FCSTD DOCUMENT  (FreeCAD 0.21R33771 (Git))
Label: pillarAssy3
License: All rights reserved
objects: Sketcher::SketchObject×109, Part::FeaturePython×100, Part::Extrusion×84, App::Part×44, Part::Cut×39, Part::Compound×35, Part::Mirroring×34, App::FeaturePython×19, Part::Revolution×18, Part::Feature×15, Spreadsheet::Sheet×13, Part::MultiFuse×12, Part::Cylinder×9, Part::Sweep×8, PartDesign::Pad×2, PartDesign::Body×1, Part::Chamfer×1, Part::Loft×1, Part::Thickness×1
note: 442 computed .brp shape members not serialized (recipe doc carries the construction recipe); baked Part::Feature solids carry a one-line shape summary decoded from their .brp

FEATURE [Sketcher::SketchObject] Sketch
  FullyConstrained = false
  Placement = pos=(0,0,0) rot=(1,0,0;1.5708rad)
  sketch-geometry (12):
    g0: LineSegment StartX=0 StartY=4910 StartZ=0 EndX=0 EndY=850 EndZ=0
    g1: LineSegment StartX=0 StartY=850 StartZ=0 EndX=550 EndY=850 EndZ=0
    g2: LineSegment StartX=950 StartY=0 StartZ=0 EndX=1450 EndY=0 EndZ=0
    g3: LineSegment StartX=1450 StartY=0 StartZ=0 EndX=1650 EndY=800 EndZ=0
    g4: LineSegment StartX=1650 StartY=800 StartZ=0 EndX=7750 EndY=1410 EndZ=0
    g5: LineSegment StartX=7750 StartY=1410 StartZ=0 EndX=7750 EndY=4260 EndZ=0
    g6: LineSegment StartX=7750 StartY=4260 StartZ=0 EndX=7300 EndY=4260 EndZ=0
    g7: LineSegment StartX=7300 StartY=4260 StartZ=0 EndX=7300 EndY=4910 EndZ=0
    g8: LineSegment StartX=7300 StartY=4910 StartZ=0 EndX=0 EndY=4910 EndZ=0
    g9: LineSegment StartX=550 StartY=850 StartZ=0 EndX=550 EndY=800 EndZ=0
    g10: LineSegment StartX=550 StartY=800 StartZ=0 EndX=750 EndY=800 EndZ=0
    g11: LineSegment StartX=750 StartY=800 StartZ=0 EndX=950 EndY=0 EndZ=0
  constraints (21):
    c: Vertical(g0)
    c: Coincident(g0,g1)
    c: Horizontal(g1)
    c: Coincident(g2,g3)
    c: Coincident(g3,g4)
    c: Coincident(g4,g5)
    c: Coincident(g5,g6)
    c: Coincident(g6,g7)
    c: Vertical(g7)
    c: Coincident(g7,g8)
    c: Coincident(g8,g0)
    c: Horizontal(g8)
    c: PointOnObject(g0,g-2)
    c: DistanceX(g1,g1) = 550
    c: Coincident(g1,g9)
    c: Vertical(g9)
    c: Coincident(g9,g10)
    c: Horizontal(g10)
    c: DistanceY(g9,g9) = 50
    c: Coincident(g10,g11)
    c: Coincident(g2,g11)
FEATURE [Part::Revolution] Revolve  label="water_level"
  Angle = 180
  Axis = (0,0,1)
  Base = (0,0,0)
  FaceMakerClass = Part::FaceMakerBullseye
  Solid = true
  Source = -> Sketch
  Symmetric = false
FEATURE [Sketcher::SketchObject] Sketch001
  FullyConstrained = true
  Placement = pos=(0,0,0) rot=(1,0,0;1.5708rad)
  expr: Constraints[22] = Spreadsheet.l2
  sketch-geometry (8):
    g0: LineSegment StartX=550 StartY=0 StartZ=0 EndX=550 EndY=30 EndZ=0
    g1: LineSegment StartX=550 StartY=30 StartZ=0 EndX=406 EndY=30 EndZ=0
    g2: LineSegment StartX=396 StartY=0 StartZ=0 EndX=396 EndY=2995 EndZ=0
    g3: LineSegment StartX=396 StartY=2995 StartZ=0 EndX=550 EndY=2995 EndZ=0
    g4: LineSegment StartX=550 StartY=2995 StartZ=0 EndX=550 EndY=2965 EndZ=0
    g5: LineSegment StartX=550 StartY=2965 StartZ=0 EndX=406 EndY=2965 EndZ=0
    g6: LineSegment StartX=406 StartY=2965 StartZ=0 EndX=406 EndY=30 EndZ=0
    g7: LineSegment StartX=550 StartY=0 StartZ=0 EndX=396 EndY=0 EndZ=0
  constraints (24):
    c: Vertical(g0)
    c: Coincident(g0,g1)
    c: Horizontal(g1)
    c: Vertical(g2)
    c: Coincident(g2,g3)
    c: Horizontal(g3)
    c: Coincident(g3,g4)
    c: Vertical(g4)
    c: Coincident(g4,g5)
    c: Horizontal(g5)
    c: Coincident(g5,g6)
    c: Vertical(g6)
    c: Coincident(g0,g7)
    c: Horizontal(g7)
    c: Coincident(g1,g6)
    c: DistanceX(g-1,g0) = 550
    c: DistanceY(g0,g0) = 30
    c: PointOnObject(g0,g-1)
    c: Coincident(g2,g7)
    c: DistanceX(g2,g1) = 10
    c: DistanceX(g-1,g1) = 406
    c: DistanceX(g-2,g3) = 550
    c: DistanceY(g-1,g3) = 2995
    c: DistanceY(g4,g4) = 30
FEATURE [Part::Revolution] Revolve001  label="bottom"
  Angle = 360
  Axis = (0,0,1)
  Base = (0,0,0)
  FaceMakerClass = Part::FaceMakerBullseye
  Solid = true
  Source = -> Sketch001
  Symmetric = false
FEATURE [Sketcher::SketchObject] Sketch002
  ExternalGeometry = -> [Revolve001]
  FullyConstrained = true
  Placement = pos=(0,0,0) rot=(1,0,0;1.5708rad)
  sketch-geometry (4):
    g0: LineSegment StartX=296 StartY=0 StartZ=0 EndX=396 EndY=0 EndZ=0
    g1: LineSegment StartX=396 StartY=0 StartZ=0 EndX=396 EndY=2995 EndZ=0
    g2: LineSegment StartX=396 StartY=2995 StartZ=0 EndX=296 EndY=2995 EndZ=0
    g3: LineSegment StartX=296 StartY=2995 StartZ=0 EndX=296 EndY=0 EndZ=0
  constraints (11):
    c: Coincident(g0,g1)
    c: Coincident(g1,g2)
    c: Coincident(g2,g3)
    c: Coincident(g3,g0)
    c: Horizontal(g0)
    c: Horizontal(g2)
    c: Vertical(g1)
    c: Vertical(g3)
    c: Distance(g0) = 100
    c: Coincident(g0,g-3)
    c: PointOnObject(g2,g-4)
FEATURE [Part::Revolution] Revolve002  label="covering"
  Angle = 360
  Axis = (0,0,1)
  Base = (0,0,0)
  FaceMakerClass = Part::FaceMakerBullseye
  Placement = pos=(0,0,850) rot=(0,0,1;0rad)
  Solid = true
  Source = -> Sketch002
  Symmetric = false
FEATURE [Sketcher::SketchObject] Sketch003
  ExternalGeometry = -> [Revolve001]
  FullyConstrained = true
  Placement = pos=(0,0,0) rot=(1,0,0;1.5708rad)
  expr: Constraints[8] = Spreadsheet.t0
  sketch-geometry (4):
    g0: LineSegment StartX=396 StartY=2995 StartZ=0 EndX=550 EndY=2995 EndZ=0
    g1: LineSegment StartX=550 StartY=2995 StartZ=0 EndX=550 EndY=3000 EndZ=0
    g2: LineSegment StartX=550 StartY=3000 StartZ=0 EndX=396 EndY=3000 EndZ=0
    g3: LineSegment StartX=396 StartY=3000 StartZ=0 EndX=396 EndY=2995 EndZ=0
  constraints (12):
    c: Coincident(g0,g1)
    c: Coincident(g1,g2)
    c: Coincident(g2,g3)
    c: Coincident(g3,g0)
    c: Horizontal(g0)
    c: Horizontal(g2)
    c: Vertical(g1)
    c: Vertical(g3)
    c: DistanceY(g1,g1) = 5
    c: DistanceY(g-1,g0) = 2995
    c: PointOnObject(g0,g-3)
    c: PointOnObject(g-4,g1)
FEATURE [Part::Revolution] Revolve003  label="gasket"
  Angle = 360
  Axis = (0,0,1)
  Base = (0,0,0)
  FaceMakerClass = Part::FaceMakerBullseye
  Placement = pos=(0,0,850) rot=(0,0,1;0rad)
  Solid = true
  Source = -> Sketch003
  Symmetric = false
FEATURE [Sketcher::SketchObject] Sketch004
  ExternalGeometry = -> [Revolve003]
  FullyConstrained = true
  Placement = pos=(0,0,0) rot=(1,0,0;1.5708rad)
  expr: Constraints[13] = Spreadsheet.l1
  sketch-geometry (6):
    g0: LineSegment StartX=550 StartY=3880 StartZ=0 EndX=406 EndY=3880 EndZ=0
    g1: LineSegment StartX=406 StartY=3880 StartZ=0 EndX=406 EndY=5150 EndZ=0
    g2: LineSegment StartX=396 StartY=5150 StartZ=0 EndX=396 EndY=3850 EndZ=0
    g3: LineSegment StartX=396 StartY=3850 StartZ=0 EndX=550 EndY=3850 EndZ=0
    g4: LineSegment StartX=550 StartY=3850 StartZ=0 EndX=550 EndY=3880 EndZ=0
    g5: LineSegment StartX=406 StartY=5150 StartZ=0 EndX=396 EndY=5150 EndZ=0
  constraints (17):
    c: Horizontal(g0)
    c: Coincident(g0,g1)
    c: Vertical(g1)
    c: Vertical(g2)
    c: Coincident(g2,g3)
    c: Horizontal(g3)
    c: Coincident(g3,g4)
    c: Coincident(g4,g0)
    c: Vertical(g4)
    c: DistanceY(g4,g4) = 30
    c: Coincident(g3,g-3)
    c: DistanceX(g2,g0) = 10
    c: PointOnObject(g2,g-4)
    c: DistanceY(g3,g1) = 1300
    c: Coincident(g5,g1)
    c: Horizontal(g5)
    c: Coincident(g2,g5)
FEATURE [Part::Revolution] Revolve004  label="top"
  Angle = 360
  Axis = (0,0,1)
  Base = (0,0,0)
  FaceMakerClass = Part::FaceMakerBullseye
  Solid = true
  Source = -> Sketch004
  Symmetric = false
FEATURE [Sketcher::SketchObject] Sketch005
  FullyConstrained = true
  Placement = pos=(0,0,0) rot=(1,0,0;1.5708rad)
  sketch-geometry (12):
    g0: LineSegment StartX=200 StartY=-1.8e-15 StartZ=0 EndX=406 EndY=-1.8e-15 EndZ=0
    g1: LineSegment StartX=406 StartY=-1.8e-15 StartZ=0 EndX=406 EndY=25 EndZ=0
    g2: LineSegment StartX=406 StartY=25 StartZ=0 EndX=200 EndY=25 EndZ=0
    g3: LineSegment StartX=0 StartY=175 StartZ=0 EndX=350 EndY=175 EndZ=0
    g4: LineSegment StartX=350 StartY=175 StartZ=0 EndX=350 EndY=200 EndZ=0
    g5: LineSegment StartX=350 StartY=200 StartZ=0 EndX=0 EndY=200 EndZ=0
    g6: LineSegment StartX=0 StartY=200 StartZ=0 EndX=0 EndY=175 EndZ=0
    g7: LineSegment StartX=242 StartY=25 StartZ=0 EndX=254 EndY=25 EndZ=0
    g8: LineSegment StartX=254 StartY=25 StartZ=0 EndX=254 EndY=175 EndZ=0
    g9: LineSegment StartX=254 StartY=175 StartZ=0 EndX=242 EndY=175 EndZ=0
    g10: LineSegment StartX=242 StartY=175 StartZ=0 EndX=242 EndY=25 EndZ=0
    g11: LineSegment StartX=200 StartY=25 StartZ=0 EndX=200 EndY=0 EndZ=0
  constraints (36):
    c: Coincident(g0,g1)
    c: Coincident(g1,g2)
    c: Horizontal(g0)
    c: Horizontal(g2)
    c: Vertical(g1)
    c: DistanceY(g1,g1) = 25
    c: DistanceX(g-1,g0) = 406
    c: Coincident(g3,g4)
    c: Coincident(g4,g5)
    c: Coincident(g5,g6)
    c: Coincident(g6,g3)
    c: Horizontal(g3)
    c: Horizontal(g5)
    c: Vertical(g4)
    c: Vertical(g6)
    c: PointOnObject(g3,g-2)
    c: DistanceY(g4,g4) = 25
    c: DistanceX(g5,g5) = 350
    c: DistanceY(g0,g4) = 200
    c: Coincident(g7,g8)
    c: Coincident(g8,g9)
    c: Coincident(g9,g10)
    c: Coincident(g10,g7)
    c: Horizontal(g7)
    c: Horizontal(g9)
    c: Vertical(g8)
    c: Vertical(g10)
    c: PointOnObject(g7,g2)
    c: PointOnObject(g8,g3)
    c: DistanceX(g9,g8) = 12
    c: Vertical(g11)
    c: Coincident(g2,g11)
    c: Coincident(g0,g11)
    c: DistanceX(g-1,g0) = 200
    c: DistanceX(g-2,g7) = 254
    c: PointOnObject(g0,g-1)
FEATURE [Part::Revolution] Revolve005  label="Revolve004"
  Angle = 360
  Axis = (0,0,1)
  Base = (0,0,0)
  FaceMakerClass = Part::FaceMakerBullseye
  Solid = true
  Source = -> Sketch005
  Symmetric = false
FEATURE [Sketcher::SketchObject] Sketch006
  ExternalGeometry = -> [Revolve005]
  FullyConstrained = true
  Placement = pos=(0,0,0) rot=(1,0,0;1.5708rad)
  sketch-geometry (6):
    g0: LineSegment StartX=406 StartY=25 StartZ=0 EndX=284 EndY=25 EndZ=0
    g1: LineSegment StartX=254 StartY=55 StartZ=0 EndX=254 EndY=175 EndZ=0
    g2: LineSegment StartX=254 StartY=175 StartZ=0 EndX=350 EndY=175 EndZ=0
    g3: LineSegment StartX=350 StartY=175 StartZ=0 EndX=406 EndY=75 EndZ=0
    g4: LineSegment StartX=406 StartY=75 StartZ=0 EndX=406 EndY=25 EndZ=0
    g5: LineSegment StartX=284 StartY=25 StartZ=0 EndX=254 EndY=55 EndZ=0
  constraints (15):
    c: Coincident(g1,g2)
    c: Coincident(g2,g3)
    c: Coincident(g3,g4)
    c: Coincident(g4,g0)
    c: Vertical(g4)
    c: Coincident(g-3,g1)
    c: Coincident(g2,g-4)
    c: DistanceY(g4,g4) = 50
    c: Coincident(g0,g-5)
    c: Coincident(g0,g5)
    c: Coincident(g1,g5)
    c: DistanceX(g-3,g0) = 30
    c: DistanceY(g-3,g1) = 30
    c: PointOnObject(g1,g-3)
    c: PointOnObject(g0,g-6)
FEATURE [Part::Extrusion] Extrude001
  Base = -> Sketch006
  Dir = (0,-1,-3e-16)
  DirMode = 2
  FaceMakerClass = Part::FaceMakerBullseye
  LengthFwd = 12
  LengthRev = 0
  Solid = true
  Symmetric = true
FEATURE [Part::FeaturePython] Array001  # Draft array (typed FeaturePython)
  AlwaysSyncPlacement = false
  Angle = 360
  ArrayType = 1
  Axis = (0,0,1)
  Base = -> Extrude001
  Center = (0,0,0)
  Count = 8
  ExpandArray = false
  Fuse = false
  IntervalAxis = (0,0,0)
  IntervalX = (50,0,0)
  IntervalY = (0,50,0)
  IntervalZ = (0,0,50)
  NumberCircles = 3
  NumberPolar = 8
  NumberX = 2
  NumberY = 2
  NumberZ = 1
  PlacementList = 8 placements: [(0,0,0),(0,0,0),(0,0,0),(0,0,0),(0,0,0),(0,0,0),(0,0,0),(0,0,0)]
  RadialDistance = 50
  ScaleList = (8) [(1,1,1),(1,1,1),(1,1,1),(1,1,1),(1,1,1),(1,1,1),(1,1,1),(1,1,1)]
  Symmetry = 1
  TangentialDistance = 25
FEATURE [Sketcher::SketchObject] Sketch007
  FullyConstrained = true
  MapMode = 5
  Placement = pos=(0,0,200) rot=(0,0,1;0rad)
  Support = -> [Revolve005]
  sketch-geometry (1):
    g0: Circle CenterX=0 CenterY=0 CenterZ=0 NormalX=0 NormalY=0 NormalZ=1 AngleXU=0 Radius=25
  constraints (2):
    c: Coincident(g0,g-1)
    c: Radius(g0) = 25
FEATURE [Part::Extrusion] Extrude002
  Base = -> Sketch007
  Dir = (0,0,1)
  DirMode = 2
  FaceMakerClass = Part::FaceMakerBullseye
  LengthFwd = 25
  LengthRev = 0
  Reversed = true
  Solid = true
  Symmetric = false
FEATURE [Part::Cut] Cut001
  Base = -> Revolve005
  Tool = -> Extrude002
FEATURE [Sketcher::SketchObject] Sketch008
  FullyConstrained = true
  MapMode = 5
  Placement = pos=(0,0,200) rot=(0,0,1;0rad)
  Support = -> [Cut001]
  sketch-geometry (2):
    g0: Circle CenterX=277.164 CenterY=114.805 CenterZ=0 NormalX=0 NormalY=0 NormalZ=1 AngleXU=0 Radius=14
    g1: LineSegment StartX=0 StartY=0 StartZ=0 EndX=277.164 EndY=114.805 EndZ=0
  constraints (5):
    c: Coincident(g1,g-1)
    c: Coincident(g1,g0)
    c: Angle(g-1,g1) = 0.392699
    c: Distance(g1) = 300
    c: Radius(g0) = 14
FEATURE [Part::Extrusion] Extrude003
  Base = -> Sketch008
  Dir = (0,0,1)
  DirMode = 2
  FaceMakerClass = Part::FaceMakerBullseye
  LengthFwd = 25
  LengthRev = 0
  Reversed = true
  Solid = true
  Symmetric = false
FEATURE [Part::FeaturePython] Array002  # Draft array (typed FeaturePython)
  AlwaysSyncPlacement = false
  Angle = 360
  ArrayType = 1
  Axis = (0,0,1)
  Base = -> Extrude003
  Center = (0,0,0)
  Count = 8
  ExpandArray = false
  Fuse = false
  IntervalAxis = (0,0,0)
  IntervalX = (50,0,0)
  IntervalY = (0,50,0)
  IntervalZ = (0,0,50)
  NumberCircles = 3
  NumberPolar = 8
  NumberX = 2
  NumberY = 2
  NumberZ = 1
  PlacementList = 8 placements: [(0,0,0),(0,0,0),(0,0,0),(0,0,0),(0,0,0),(0,0,0),(0,0,0),(0,0,0)]
  RadialDistance = 50
  ScaleList = (8) [(1,1,1),(1,1,1),(1,1,1),(1,1,1),(1,1,1),(1,1,1),(1,1,1),(1,1,1)]
  Symmetry = 1
  TangentialDistance = 25
FEATURE [Part::Cut] Cut002  label="base"
  Base = -> Cut001
  Tool = -> Array002
FEATURE [Part::MultiFuse] Fusion  label="base001"
  Placement = pos=(0,0,5150) rot=(0,0,1;0rad)
  Shapes = -> [Cut002,Array001]
FEATURE [Sketcher::SketchObject] Sketch009
  FullyConstrained = true
  MapMode = 5
  Placement = pos=(0,0,0) rot=(1,0,0;3.14159rad)
  Support = -> [Revolve001]
  sketch-geometry (2):
    g0: LineSegment StartX=0 StartY=0 StartZ=0 EndX=461.94 EndY=191.342 EndZ=0
    g1: Circle CenterX=461.94 CenterY=191.342 CenterZ=0 NormalX=0 NormalY=0 NormalZ=1 AngleXU=0 Radius=17.5
  constraints (5):
    c: Coincident(g0,g-1)
    c: Coincident(g1,g0)
    c: Radius(g1) = 17.5
    c: Distance(g0) = 500
    c: Angle(g-1,g0) = 0.392699
FEATURE [Part::Extrusion] Extrude004
  Base = -> Sketch009
  Dir = (0,0,-1)
  DirMode = 2
  FaceMakerClass = Part::FaceMakerBullseye
  LengthFwd = 3000
  LengthRev = 0
  Reversed = true
  Solid = true
  Symmetric = false
FEATURE [Part::FeaturePython] Array003  # Draft array (typed FeaturePython)
  AlwaysSyncPlacement = false
  Angle = 360
  ArrayType = 1
  Axis = (0,0,1)
  Base = -> Extrude004
  Center = (0,0,0)
  Count = 8
  ExpandArray = false
  Fuse = false
  IntervalAxis = (0,0,0)
  IntervalX = (50,0,0)
  IntervalY = (0,50,0)
  IntervalZ = (0,0,50)
  NumberCircles = 3
  NumberPolar = 8
  NumberX = 2
  NumberY = 2
  NumberZ = 1
  PlacementList = 8 placements: [(0,0,0),(0,0,0),(0,0,0),(0,0,0),(0,0,0),(0,0,0),(0,0,0),(0,0,0)]
  RadialDistance = 50
  ScaleList = (8) [(1,1,1),(1,1,1),(1,1,1),(1,1,1),(1,1,1),(1,1,1),(1,1,1),(1,1,1)]
  Symmetry = 1
  TangentialDistance = 25
FEATURE [Part::Cut] Cut003  label="bottom001"
  Base = -> Revolve001
  Placement = pos=(0,0,850) rot=(0,0,1;0rad)
  Tool = -> Array003
FEATURE [Sketcher::SketchObject] Sketch010
  ExternalGeometry = -> [Revolve004]
  FullyConstrained = true
  Placement = pos=(0,0,0) rot=(1,0,0;1.5708rad)
  sketch-geometry (8):
    g0: LineSegment StartX=-45 StartY=4775 StartZ=0 EndX=45 EndY=4775 EndZ=0
    g1: LineSegment StartX=75 StartY=4805 StartZ=0 EndX=75 EndY=5045 EndZ=0
    g2: LineSegment StartX=45 StartY=5075 StartZ=0 EndX=-45 EndY=5075 EndZ=0
    g3: LineSegment StartX=-75 StartY=5045 StartZ=0 EndX=-75 EndY=4805 EndZ=0
    g4: ArcOfCircle CenterX=45 CenterY=5045 CenterZ=0 NormalX=0 NormalY=0 NormalZ=1 AngleXU=0 Radius=30 StartAngle=-3.6e-15 EndAngle=1.5708
    g5: ArcOfCircle CenterX=-45 CenterY=5045 CenterZ=0 NormalX=0 NormalY=0 NormalZ=1 AngleXU=0 Radius=30 StartAngle=1.5708 EndAngle=3.14159
    g6: ArcOfCircle CenterX=-45 CenterY=4805 CenterZ=0 NormalX=0 NormalY=0 NormalZ=1 AngleXU=0 Radius=30 StartAngle=3.14159 EndAngle=4.71239
    g7: ArcOfCircle CenterX=45 CenterY=4805 CenterZ=0 NormalX=0 NormalY=0 NormalZ=1 AngleXU=0 Radius=30 StartAngle=4.71239 EndAngle=6.28319
  constraints (20):
    c: Horizontal(g0)
    c: Horizontal(g2)
    c: Vertical(g1)
    c: Vertical(g3)
    c: Tangent(g1,g4) = -1.5708
    c: Tangent(g2,g4) = -1.5708
    c: Tangent(g2,g5) = -1.5708
    c: Tangent(g3,g5) = -1.5708
    c: Tangent(g0,g6) = -1.5708
    c: Tangent(g3,g6) = -1.5708
    c: Tangent(g0,g7) = -1.5708
    c: Tangent(g1,g7) = -1.5708
    c: DistanceY(g0,g2) = 300
    c: DistanceX(g3,g1) = 150
    c: DistanceX(g-1,g1) = 75
    c: Radius(g4) = 30
    c: Equal(g4,g5)
    c: Equal(g5,g6)
    c: Equal(g6,g7)
    c: DistanceY(g2,g-3) = 75
FEATURE [Part::Extrusion] Extrude
  Base = -> Sketch010
  Dir = (0,-1,2e-16)
  DirMode = 2
  FaceMakerClass = Part::FaceMakerBullseye
  LengthFwd = 500
  LengthRev = 0
  Solid = true
  Symmetric = false
FEATURE [Part::FeaturePython] Array  # Draft array (typed FeaturePython)
  AlwaysSyncPlacement = false
  Angle = 360
  ArrayType = 1
  Axis = (0,0,1)
  Base = -> Extrude
  Center = (0,0,0)
  Count = 4
  ExpandArray = false
  Fuse = false
  IntervalAxis = (0,0,0)
  IntervalX = (50,0,0)
  IntervalY = (0,50,0)
  IntervalZ = (0,0,50)
  NumberCircles = 3
  NumberPolar = 4
  NumberX = 2
  NumberY = 2
  NumberZ = 1
  PlacementList = 4 placements: [(0,0,0),(0,0,0),(0,0,0),(0,0,0)]
  RadialDistance = 50
  ScaleList = (4) [(1,1,1),(1,1,1),(1,1,1),(1,1,1)]
  Symmetry = 1
  TangentialDistance = 25
FEATURE [Part::Cut] Cut
  Base = -> Revolve004
  Tool = -> Array
FEATURE [Sketcher::SketchObject] Sketch011
  FullyConstrained = true
  MapMode = 5
  Placement = pos=(0,0,3850) rot=(1,0,0;3.14159rad)
  Support = -> [Cut]
  sketch-geometry (2):
    g0: LineSegment StartX=0 StartY=0 StartZ=0 EndX=461.94 EndY=191.342 EndZ=0
    g1: Circle CenterX=461.94 CenterY=191.342 CenterZ=0 NormalX=0 NormalY=0 NormalZ=1 AngleXU=0 Radius=17.5
  constraints (5):
    c: Coincident(g0,g-1)
    c: Distance(g0) = 500
    c: Coincident(g1,g0)
    c: Radius(g1) = 17.5
    c: Angle(g-1,g0) = 0.392699
FEATURE [Part::Extrusion] Extrude005
  Base = -> Sketch011
  Dir = (0,0,-1)
  DirMode = 2
  FaceMakerClass = Part::FaceMakerBullseye
  LengthFwd = 30
  LengthRev = 0
  Reversed = true
  Solid = true
  Symmetric = false
FEATURE [Part::Cut] Cut004
  Base = -> Cut
  Tool = -> Extrude005
FEATURE [Part::FeaturePython] Array004  # Draft array (typed FeaturePython)
  AlwaysSyncPlacement = false
  Angle = 360
  ArrayType = 1
  Axis = (0,0,1)
  Base = -> Extrude005
  Center = (0,0,0)
  Count = 8
  ExpandArray = false
  Fuse = false
  IntervalAxis = (0,0,0)
  IntervalX = (50,0,0)
  IntervalY = (0,50,0)
  IntervalZ = (0,0,50)
  NumberCircles = 3
  NumberPolar = 8
  NumberX = 2
  NumberY = 2
  NumberZ = 1
  PlacementList = 8 placements: [(0,0,0),(0,0,0),(0,0,0),(0,0,0),(0,0,0),(0,0,0),(0,0,0),(0,0,0)]
  RadialDistance = 50
  ScaleList = (8) [(1,1,1),(1,1,1),(1,1,1),(1,1,1),(1,1,1),(1,1,1),(1,1,1),(1,1,1)]
  Symmetry = 1
  TangentialDistance = 25
FEATURE [Part::Cut] Cut005  label="top001"
  Base = -> Cut004
  Placement = pos=(0,0,1.98468e-08) rot=(0,0,1;0rad)
  Tool = -> Array004
FEATURE [Spreadsheet::Sheet] Spreadsheet
  cells = A2='top  l1; B2(l1)=1300; A3='bottom  l2; B3(l2)=2995; A4='base l3; B4(l3)=200; A5='gasket  t0; B5(t0)=5
FEATURE [Sketcher::SketchObject] Sketch012
  FullyConstrained = true
  MapMode = 5
  Placement = pos=(0,0,800) rot=(0,0,1;0rad)
  sketch-geometry (1):
    g0: Circle CenterX=0 CenterY=0 CenterZ=0 NormalX=0 NormalY=0 NormalZ=1 AngleXU=0 Radius=550
  constraints (2):
    c: Coincident(g0,g-1)
    c: Radius(g0) = 550
FEATURE [Part::Extrusion] Extrude006  label="sinder001"
  Base = -> Sketch012
  Dir = (0,0,1)
  DirMode = 2
  FaceMakerClass = Part::FaceMakerBullseye
  LengthFwd = 50
  LengthRev = 0
  Solid = true
  Symmetric = false
FEATURE [App::FeaturePython] circularEdge_002  label="circularEdge_002__bottom001"  # a2plus constraint (typed FeaturePython)
  Object1 = Revolve003
  Object2 = Cut003
  SubElement1 = Edge3
  SubElement2 = Edge16
  Suppressed = false
  Type = circularEdge
  directionConstraint = 0
  lockRotation = false
  offset = 0
FEATURE [App::FeaturePython] circularEdge_002_mirror  label="circularEdge_002__gasket"  # a2plus constraint (typed FeaturePython)
  Object1 = Revolve003
  Object2 = Cut003
  SubElement1 = Edge3
  SubElement2 = Edge16
  Suppressed = false
  Type = circularEdge
  directionConstraint = 1
  lockRotation = false
  offset = 0
FEATURE [App::FeaturePython] circularEdge_003  label="circularEdge_003__gasket"  # a2plus constraint (typed FeaturePython)
  Object1 = Cut005
  Object2 = Revolve003
  ParentTreeObject = -> Cut005
  SubElement1 = Edge29
  SubElement2 = Edge2
  Suppressed = false
  Type = circularEdge
  directionConstraint = 0
  lockRotation = false
  offset = 0
FEATURE [App::FeaturePython] circularEdge_003_mirror  label="circularEdge_003__top001"  # a2plus constraint (typed FeaturePython)
  Object1 = Cut005
  Object2 = Revolve003
  ParentTreeObject = -> Revolve003
  SubElement1 = Edge29
  SubElement2 = Edge2
  Suppressed = false
  Type = circularEdge
  directionConstraint = 1
  lockRotation = false
  offset = 0
FEATURE [App::FeaturePython] circularEdge_004  label="circularEdge_004__top001"  # a2plus constraint (typed FeaturePython)
  Object1 = Fusion
  Object2 = Cut005
  ParentTreeObject = -> Fusion
  SubElement1 = Edge18
  SubElement2 = Edge56
  Suppressed = false
  Type = circularEdge
  directionConstraint = 0
  lockRotation = false
  offset = 0
FEATURE [App::FeaturePython] circularEdge_004_mirror  label="circularEdge_004__base001"  # a2plus constraint (typed FeaturePython)
  Object1 = Fusion
  Object2 = Cut005
  ParentTreeObject = -> Cut005
  SubElement1 = Edge18
  SubElement2 = Edge56
  Suppressed = false
  Type = circularEdge
  directionConstraint = 0
  lockRotation = false
  offset = 0
FEATURE [Part::Feature] Part__Feature006  label="COMPOUND"
  shape: bbox 1200 x 1200 x 187 mm, 60 faces (baked)
FEATURE [Part::Feature] Part__Feature007  label="reducer_cage"
  Placement = pos=(0,0,5542.95) rot=(0,0,1;0rad)
  shape: bbox 1029 x 1029 x 150 mm, 111 faces (baked)
FEATURE [Part::Feature] Part__Feature008  label="COMPOUND002"
  shape: bbox 432.6 x 812.4 x 587.8 mm, 44 faces (baked)
FEATURE [Part::Feature] Part__Feature009  label="COMPOUND003"
  shape: bbox 260 x 238.8 x 86.61 mm, 28 faces (baked)
FEATURE [App::Part] COMPOUND  label="COMPOUND004"
  Group = -> [Part__Feature006,Part__Feature008,Part__Feature009]
  Origin = -> Origin003
FEATURE [Part::Feature] Part__Feature002  label="50A30_() v1"
  Placement = pos=(162.912,-280.358,517.02) rot=(0,0,1;1.57038rad)
  shape: bbox 162.2 x 50.03 x 161.7 mm, 187 faces (baked)
FEATURE [Part::Feature] Part__Feature003  label="CNHM05-609-A10 v2"
  Placement = pos=(272.819,-129.883,800) rot=(0,0,1;1.5708rad)
  shape: bbox 203.5 x 337.5 x 183 mm, 1357 faces (baked)
FEATURE [Part::Feature] Part__Feature004  label="K50B21_() v1"
  Placement = pos=(322.235,-280.393,797.172) rot=(0,0,1;1.5708rad)
  shape: bbox 116.2 x 45.19 x 116.5 mm, 132 faces (baked)
FEATURE [Part::Feature] Part__Feature005  label="チェンカバー v2"
  Placement = pos=(162.903,-331.008,517.02) rot=(0,0,1;0rad)
  shape: bbox 430 x 100 x 545 mm, 11 faces (baked)
FEATURE [App::Part] __________NSD0_5_v20  label="駆動部_NSD0
5 v20"
  Group = -> [Part__Feature002,Part__Feature003,Part__Feature004,Part__Feature005,COMPOUND]
  Origin = -> Origin004
FEATURE [App::Part] Part  label="reducer"
  Group = -> [__________NSD0_5_v20]
  Origin = -> Origin001
  Placement = pos=(0,0,5756.7) rot=(0,0,1;0rad)
FEATURE [Part::Compound] Compound001  label="reducer001"
  Links = -> [Part]
  Placement = pos=(-3.11034,0,-406.72) rot=(0,0,1;0rad)
FEATURE [Spreadsheet::Sheet] Spreadsheet001
  cells = A2='cage width W0; B2(W0)=1800; A3='cageLength L0; B3(L0)=4500; A4='mainShape mShp; B4(mShp)='100x100x10; A5='mShp gage mg0; B5(mg0)=55; A6='mShp width mb0; B6(mb0)=100; A7='horizontalBeam hShp; B7(hShp)='150x75x9; A8='hShp gage hg; B8(hg)=75; A9='hb0; B9(hb0)=75; A10='lutticeBeam LShp; B10(LShp)='75x75x6; A11='luttice_widht Lb0; B11(Lb0)=75; A12='lutitice length ll; B12(ll)=2234.39029715043; A13='luttice angle sita; B13(sita)=40.6; A14='gusset Gta; B14(Gta)=300; A15='gussetThickness gt; B15(gt)=6; A16='lx; B16(lx)=-760.518050346879; A17='lz; B17(lz)=201.097312797114; A18='Divishon no; B18(n0)=3; A19='DivishonPitch p0; B19(p0)=1450; A20='rakeWidth  rw; B20(rw)=952; A22='Angle; D22='Channel; A23='40x40x5; B23=40; C23=17; D23='75x40x5; E23=75; F23=40; G23=17; A24='50x50x5; B24=50; C24=30; D24='100x50x5; E24=100; F24=50; G24=30; A25='65x65x6; B25=65; C25=35; D25='125x65x6; E25=125; F25=65; G25=35; A26='75x75x6; B26=75; C26=40; D26='150x75x9; E26=150; F26=75; G26=40; A27='90x90x7; B27=90; C27=50; D27='180x75x7; E27=180; F27=75; G27=40; A28='100x100x10; B28=100; C28=55; F28=75; G28=40; A29='130x130x12; B29=130
FEATURE [Part::FeaturePython] AngleSteel  label="mShp"  # WARN: FeaturePython — macro-defined, semantics opaque (R4)
  A = 100
  B = 100
  L = 4500
  Placement = pos=(-850,-850,0) rot=(0,0,1;1.5708rad)
  Solid = true
  g0 = 7.85
  mass = 67.1327
  size = 17
  standard = SS_Equal
  t = 7
  expr: .Placement.Base.x = -Spreadsheet001.W0 / 2 + Spreadsheet001.mb0 / 2
  expr: .Placement.Base.y = -Spreadsheet001.W0 / 2 + Spreadsheet001.mb0 / 2
  expr: L = Spreadsheet001.L0
FEATURE [Part::FeaturePython] Array005  # Draft array (typed FeaturePython)
  AlwaysSyncPlacement = false
  Angle = 360
  ArrayType = 1
  Axis = (0,0,1)
  Base = -> AngleSteel
  Center = (0,0,0)
  Count = 4
  ExpandArray = false
  Fuse = false
  IntervalAxis = (0,0,0)
  IntervalX = (50,0,0)
  IntervalY = (0,50,0)
  IntervalZ = (0,0,50)
  NumberCircles = 3
  NumberPolar = 4
  NumberX = 2
  NumberY = 2
  NumberZ = 1
  PlacementList = 4 placements: [(-850,-850,0),(850,-850,0),(850,850,0),(-850,850,0)]
  RadialDistance = 50
  ScaleList = (4) [(1,1,1),(1,1,1),(1,1,1),(1,1,1)]
  Symmetry = 1
  TangentialDistance = 25
FEATURE [Part::FeaturePython] ChannelSteel  label="hShp"  # WARN: FeaturePython — macro-defined, semantics opaque (R4)
  B = 75
  H = 150
  L = 1600
  Placement = pos=(-800,-862.5,75) rot=(0.57735,0.57735,0.57735;2.0944rad)
  Solid = true
  g0 = 7.85
  mass = 35.6065
  size = 4
  standard = SS
  t1 = 6
  t2 = 8
  expr: .Placement.Base.x = -Spreadsheet001.W0 / 2 + Spreadsheet001.mb0
  expr: .Placement.Base.y = -Spreadsheet001.W0 / 2 + Spreadsheet001.hb0 / 2
  expr: .Placement.Base.z = Spreadsheet001.hg
  expr: L = Spreadsheet001.W0 - Spreadsheet001.mb0 * 2
FEATURE [Part::FeaturePython] Array006  label="hBeam"  # Draft array (typed FeaturePython)
  AlwaysSyncPlacement = false
  Angle = 360
  ArrayType = 0
  Axis = (0,0,1)
  Base = -> ChannelSteel
  Center = (0,0,0)
  Count = 4
  ExpandArray = false
  Fuse = false
  IntervalAxis = (0,0,0)
  IntervalX = (100,0,0)
  IntervalY = (0,100,0)
  IntervalZ = (0,0,1450)
  NumberCircles = 3
  NumberPolar = 5
  NumberX = 1
  NumberY = 1
  NumberZ = 4
  PlacementList = 4 placements: arithmetic series from (-800,-862.5,75) step (0,0,1450) to (-800,-862.5,4425)
  RadialDistance = 50
  ScaleList = (4) [(1,1,1),(1,1,1),(1,1,1),(1,1,1)]
  Symmetry = 1
  TangentialDistance = 25
  expr: .IntervalZ.z = Spreadsheet001.p0
  expr: NumberZ = Spreadsheet001.n0 + 1
FEATURE [Sketcher::SketchObject] Sketch013
  ExternalGeometry = -> [AngleSteel]
  FullyConstrained = true
  MapMode = 5
  Placement = pos=(-850,-900,0) rot=(1,0,0;1.5708rad)
  Support = -> [AngleSteel]
  expr: Constraints[10] = Spreadsheet001.hg
  expr: Constraints[11] = Spreadsheet001.L0 - 2 * Spreadsheet001.hg
  expr: Constraints[12] = Spreadsheet001.W0 - Spreadsheet001.mb0
  expr: Constraints[16] = Spreadsheet001.p0
  expr: Constraints[24] = Spreadsheet001.p0
  sketch-geometry (9):
    g0: LineSegment StartX=-9e-16 StartY=75 StartZ=0 EndX=1700 EndY=75 EndZ=0
    g1: LineSegment StartX=1700 StartY=75 StartZ=0 EndX=1700 EndY=4425 EndZ=0
    g2: LineSegment StartX=1700 StartY=4425 StartZ=0 EndX=0 EndY=4425 EndZ=0
    g3: LineSegment StartX=-9e-16 StartY=4425 StartZ=0 EndX=-9e-16 EndY=75 EndZ=0
    g4: LineSegment StartX=-1.8e-15 StartY=1525 StartZ=0 EndX=1700 EndY=1525 EndZ=0
    g5: LineSegment StartX=-9e-16 StartY=75 StartZ=0 EndX=1700 EndY=1525 EndZ=0
    g6: LineSegment StartX=-1.8e-15 StartY=1525 StartZ=0 EndX=1700 EndY=2975 EndZ=0
    g7: LineSegment StartX=-1.8e-15 StartY=2975 StartZ=0 EndX=1700 EndY=2975 EndZ=0
    g8: LineSegment StartX=-1.8e-15 StartY=1525 StartZ=0 EndX=1700 EndY=75 EndZ=0
  constraints (27):
    c: DistanceX(g-3,g-1) = 50
    c: Coincident(g0,g1)
    c: Coincident(g1,g2)
    c: Coincident(g2,g3)
    c: Coincident(g3,g0)
    c: Horizontal(g0)
    c: Horizontal(g2)
    c: Vertical(g1)
    c: Vertical(g3)
    c: PointOnObject(g0,g-2)
    c: DistanceY(g-1,g0) = 75
    c: Distance(g3) = 4350
    c: Distance(g0) = 1700
    c: PointOnObject(g4,g3)
    c: PointOnObject(g4,g1)
    c: Horizontal(g4)
    c: DistanceY(g0,g4) = 1450
    c: Coincident(g5,g0)
    c: Coincident(g5,g4)
    c: Coincident(g6,g4)
    c: PointOnObject(g6,g1)
    c: PointOnObject(g7,g3)
    c: Coincident(g7,g6)
    c: Horizontal(g7)
    c: DistanceY(g4,g7) = 1450
    c: Coincident(g8,g4)
    c: Coincident(g8,g0)
FEATURE [Part::FeaturePython] AngleSteel001  label="LShp"  # WARN: FeaturePython — macro-defined, semantics opaque (R4)
  A = 75
  B = 75
  L = 1000
  Placement = pos=(0,0,0) rot=(-1,0,0;1.5708rad)
  Solid = false
  g0 = 7.85
  mass = 0
  size = 10
  standard = SS_Equal
  t = 6
FEATURE [Sketcher::SketchObject] Sketch014
  ExternalGeometry = -> [Sketch013,AngleSteel]
  FullyConstrained = false
  MapMode = 5
  Placement = pos=(-850,-900,0) rot=(1,0,0;1.5708rad)
  Support = -> [AngleSteel]
  expr: Constraints[12] = Spreadsheet001.Gta
  expr: Constraints[13] = Spreadsheet001.Lb0
  sketch-geometry (5):
    g0: LineSegment StartX=-30 StartY=20 StartZ=0 EndX=-30 EndY=170 EndZ=0
    g1: LineSegment StartX=-30 StartY=170 StartZ=0 EndX=65.9277 EndY=431.025 EndZ=0
    g2: LineSegment StartX=65.9277 StartY=431.025 StartZ=0 EndX=110.353 EndY=383.576 EndZ=0
    g3: LineSegment StartX=110.353 StartY=383.576 StartZ=0 EndX=120 EndY=20 EndZ=0
    g4: LineSegment StartX=120 StartY=20 StartZ=0 EndX=-30 EndY=20 EndZ=0
  constraints (15):
    c: Vertical(g0)
    c: Coincident(g0,g1)
    c: Coincident(g1,g2)
    c: Coincident(g2,g3)
    c: Coincident(g3,g4)
    c: Coincident(g4,g0)
    c: Horizontal(g4)
    c: DistanceX(g-4,g0) = 20
    c: DistanceY(g-4,g0) = 20
    c: DistanceY(g0,g0) = 150
    c: DistanceX(g4,g4) = 150
    c: Perpendicular(g2,g-3)
    c: Distance(g-3,g2) = 300
    c: Distance(g2) = 75
    c: PointOnObject(g1,g-5)
FEATURE [Sketcher::SketchObject] Sketch015
  ExternalGeometry = -> [AngleSteel,Sketch013]
  FullyConstrained = false
  MapMode = 5
  Placement = pos=(-850,-900,0) rot=(1,0,0;1.5708rad)
  Support = -> [AngleSteel]
  expr: Constraints[11] = Spreadsheet001.Lb0
  expr: Constraints[15] = Spreadsheet001.Gta
  expr: Constraints[16] = Spreadsheet001.Gta
  sketch-geometry (6):
    g0: LineSegment StartX=2061.36 StartY=3416.88 StartZ=0 EndX=2105.78 EndY=3464.33 EndZ=0
    g1: LineSegment StartX=2105.78 StartY=3464.33 StartZ=0 EndX=2105.78 EndY=-155.999 EndZ=0
    g2: LineSegment StartX=2105.78 StartY=-155.999 StartZ=0 EndX=2061.36 EndY=-108.55 EndZ=0
    g3: LineSegment StartX=2061.36 StartY=-108.55 StartZ=0 EndX=-30 EndY=1804.17 EndZ=0
    g4: LineSegment StartX=-30 StartY=1804.17 StartZ=0 EndX=-30 EndY=1504.17 EndZ=0
    g5: LineSegment StartX=-30 StartY=1504.17 StartZ=0 EndX=2061.36 EndY=3416.88 EndZ=0
  constraints (18):
    c: Coincident(g0,g1)
    c: Vertical(g1)
    c: Coincident(g1,g2)
    c: Coincident(g2,g3)
    c: Coincident(g3,g4)
    c: Vertical(g4)
    c: Coincident(g4,g5)
    c: Coincident(g5,g0)
    c: Distance(g3,g-3) = 20
    c: Distance(g4) = 300
    c: DistanceY(g-4,g3) = 150
    c: Distance(g0) = 75
    c: Perpendicular(g0,g-5)
    c: PointOnObject(g0,g-6)
    c: Equal(g0,g2)
    c: Distance(g-7,g2) = 300
    c: Distance(g-7,g0) = 300
    c: Perpendicular(g2,g-7)
FEATURE [Sketcher::SketchObject] Sketch016
  ExternalGeometry = -> [Sketch013]
  FullyConstrained = false
  MapMode = 5
  Placement = pos=(-850,-900,0) rot=(1,0,0;1.5708rad)
  Support = -> [AngleSteel]
  expr: Constraints[6] = Spreadsheet001.Gta / 4
  sketch-geometry (7):
    g0: LineSegment StartX=958.326 StartY=905.1 StartZ=0 EndX=1023.98 EndY=740.266 EndZ=0
    g1: LineSegment StartX=980.855 StartY=691.632 StartZ=0 EndX=831.978 EndY=772.465 EndZ=0
    g2: LineSegment StartX=831.978 StartY=772.465 StartZ=0 EndX=21.625 EndY=715.913 EndZ=0
    g3: LineSegment StartX=21.625 StartY=715.913 StartZ=0 EndX=710.292 EndY=941.092 EndZ=0
    g4: LineSegment StartX=710.292 StartY=941.092 StartZ=0 EndX=768.169 EndY=998.508 EndZ=0
    g5: LineSegment StartX=768.169 StartY=998.508 StartZ=0 EndX=-1.53536 EndY=864.845 EndZ=0
    g6: LineSegment StartX=-1.53536 StartY=864.845 StartZ=0 EndX=958.326 EndY=905.1 EndZ=0
  constraints (8):
    c: Coincident(g1,g2)
    c: Coincident(g2,g3)
    c: Coincident(g3,g4)
    c: Coincident(g4,g5)
    c: PointOnObject(g2,g-5)
    c: PointOnObject(g5,g-5)
    c: Distance(g1,g-3) = 75
    c: Coincident(g6,g5)
FEATURE [Sketcher::SketchObject] Sketch017
  ExternalGeometry = -> [Sketch013]
  FullyConstrained = false
  MapMode = 5
  Placement = pos=(-850,-900,0) rot=(1,0,0;1.5708rad)
  Support = -> [AngleSteel]
  expr: Constraints[19] = Spreadsheet001.Lb0
  expr: Constraints[21] = Spreadsheet001.Gta / 2
  expr: Constraints[22] = Spreadsheet001.Lb0 + 60
  expr: Constraints[23] = Spreadsheet001.Lb0 + 30
  expr: Constraints[4] = Spreadsheet001.Gta
  sketch-geometry (8):
    g0: LineSegment StartX=1835.41 StartY=1986.43 StartZ=0 EndX=1882.86 EndY=2030.86 EndZ=0
    g1: LineSegment StartX=1882.86 StartY=2030.86 StartZ=0 EndX=770.762 EndY=-4101.4 EndZ=0
    g2: LineSegment StartX=770.762 StartY=-4101.4 StartZ=0 EndX=818.211 EndY=-4145.82 EndZ=0
    g3: LineSegment StartX=818.211 StartY=-4145.82 StartZ=0 EndX=1808.06 EndY=1549.86 EndZ=0
    g4: LineSegment StartX=1808.06 StartY=1549.86 StartZ=0 EndX=1760.61 EndY=1505.43 EndZ=0
    g5: LineSegment StartX=1760.61 StartY=1505.43 StartZ=0 EndX=849.378 EndY=-4346.24 EndZ=0
    g6: LineSegment StartX=849.378 StartY=-4346.24 StartZ=0 EndX=801.929 EndY=-4301.81 EndZ=0
    g7: LineSegment StartX=801.929 StartY=-4301.81 StartZ=0 EndX=1835.41 EndY=1986.43 EndZ=0
  constraints (24):
    c: Coincident(g0,g1)
    c: Coincident(g1,g2)
    c: Coincident(g2,g3)
    c: PointOnObject(g1,g-4)
    c: Distance(g3,g0) = 300
    c: PointOnObject(g0,g-5)
    c: Equal(g2,g0)
    c: PointOnObject(g3,g-5)
    c: Coincident(g3,g4)
    c: Coincident(g4,g5)
    c: Coincident(g5,g6)
    c: Coincident(g6,g7)
    c: Coincident(g7,g0)
    c: Parallel(g0,g-7)
    c: Parallel(g4,g-7)
    c: Parallel(g2,g-8)
    c: Parallel(g6,g-8)
    c: PointOnObject(g6,g-4)
    c: Equal(g2,g4)
    c: Distance(g4) = 75
    c: Equal(g0,g6)
    c: Distance(g3,g-7) = 150
    c: Distance(g6,g2) = 135
    c: Distance(g6,g-5) = 105
FEATURE [Sketcher::SketchObject] Sketch018
  ExternalGeometry = -> [Sketch013,AngleSteel]
  FullyConstrained = true
  MapMode = 5
  Placement = pos=(-850,-900,0) rot=(1,0,0;1.5708rad)
  Support = -> [AngleSteel]
  expr: Constraints[13] = Spreadsheet001.Gta
  expr: Constraints[14] = Spreadsheet001.Lb0
  expr: Constraints[17] = Spreadsheet001.Lb0 / 2
  expr: Constraints[2] = Spreadsheet001.p0
  sketch-geometry (6):
    g0: LineSegment StartX=0 StartY=4425 StartZ=0 EndX=1700 EndY=2975 EndZ=0
    g1: LineSegment StartX=-30 StartY=4480 StartZ=0 EndX=120 EndY=4480 EndZ=0
    g2: LineSegment StartX=120 StartY=4480 StartZ=0 EndX=-252.586 EndY=4591.15 EndZ=0
    g3: LineSegment StartX=-252.586 StartY=4591.15 StartZ=0 EndX=-203.915 EndY=4648.22 EndZ=0
    g4: LineSegment StartX=-203.915 StartY=4648.22 StartZ=0 EndX=-30 EndY=4630 EndZ=0
    g5: LineSegment StartX=-30 StartY=4630 StartZ=0 EndX=-30 EndY=4480 EndZ=0
  constraints (18):
    c: Coincident(g0,g-3)
    c: PointOnObject(g0,g-4)
    c: DistanceY(g0,g0) = 1450
    c: Horizontal(g1)
    c: Coincident(g1,g2)
    c: Coincident(g2,g3)
    c: Coincident(g3,g4)
    c: Coincident(g4,g5)
    c: Coincident(g5,g1)
    c: Vertical(g5)
    c: DistanceY(g1,g-5) = 20
    c: DistanceX(g-5,g1) = 20
    c: Perpendicular(g3,g0)
    c: Distance(g0,g3) = 300
    c: Distance(g3) = 75
    c: Distance(g5) = 150
    c: Distance(g1) = 150
    c: Distance(g2,g0) = 37.5
FEATURE [Part::FeaturePython] ChannelSteel001  # WARN: FeaturePython — macro-defined, semantics opaque (R4)
  B = 75
  H = 150
  L = 680
  Placement = pos=(0,0,6e-15) rot=(0.57735,-0.57735,-0.57735;2.0944rad)
  Solid = true
  g0 = 7.85
  mass = 15.1328
  size = 4
  standard = SS
  t1 = 6
  t2 = 8
FEATURE [Sketcher::SketchObject] Sketch019
  ExternalGeometry = -> [ChannelSteel001]
  FullyConstrained = false
  MapMode = 5
  Placement = pos=(7.49e-14,-8.3e-15,75) rot=(0,0,1;1.5708rad)
  Support = -> [ChannelSteel001]
  sketch-geometry (3):
    g0: LineSegment StartX=37.5 StartY=0 StartZ=0 EndX=-38.6181 EndY=76.1181 EndZ=0
    g1: LineSegment StartX=-38.6181 StartY=0 StartZ=0 EndX=37.5 EndY=0 EndZ=0
    g2: LineSegment StartX=-38.6181 StartY=0 StartZ=0 EndX=-38.6181 EndY=76.1181 EndZ=0
  constraints (7):
    c: Coincident(g-3,g0)
    c: Coincident(g1,g0)
    c: Coincident(g2,g1)
    c: Coincident(g2,g0)
    c: Vertical(g2)
    c: Horizontal(g1)
    c: Angle(g0,g1) = 0.785398
FEATURE [Part::Extrusion] Extrude007  label="Extrude006"
  Base = -> Sketch019
  Dir = (1e-15,-1e-16,1)
  DirMode = 2
  FaceMakerClass = Part::FaceMakerBullseye
  LengthFwd = 150
  LengthRev = 0
  Reversed = true
  Solid = true
  Symmetric = false
FEATURE [Part::Mirroring] Mirror005  label="Extrude006 (mirrored)"
  Base = (-500,32.5,62.5)
  Normal = (-1,9e-16,0)
  Placement = pos=(299.54,0,0) rot=(0,0,1;0rad)
  Source = -> Extrude007
FEATURE [Part::Compound] Compound003
  Links = -> [Mirror005,Extrude007]
FEATURE [Part::Cut] Cut006
  Base = -> ChannelSteel001
  Placement = pos=(-363,-857,75) rot=(0,0,-1;0.785398rad)
  Tool = -> Compound003
  expr: .Placement.Base.x = -Spreadsheet001.W0 / 2 + 537
  expr: .Placement.Base.y = -Spreadsheet001.W0 / 2 + 43
FEATURE [PartDesign::Body] Body
  Origin = -> Origin006
  Placement = pos=(0,-400,0) rot=(0,0,1;0rad)
FEATURE [Sketcher::SketchObject] Sketch020
  FullyConstrained = true
  MapMode = 5
  Placement = pos=(0,0,0) rot=(1,0,0;1.5708rad)
  Support = -> [XZ_Plane006]
  expr: Constraints[10] = Spreadsheet001.W0 / 2
  expr: Constraints[15] = Spreadsheet001.hg
  expr: Constraints[9] = Spreadsheet001.hg * 2
  sketch-geometry (7):
    g0: LineSegment StartX=900 StartY=0 StartZ=0 EndX=900 EndY=150 EndZ=0
    g1: LineSegment StartX=900 StartY=150 StartZ=0 EndX=930 EndY=150 EndZ=0
    g2: LineSegment StartX=930 StartY=150 StartZ=0 EndX=999.298 EndY=104.199 EndZ=0
    g3: ArcOfCircle CenterX=980 CenterY=75 CenterZ=0 NormalX=0 NormalY=0 NormalZ=1 AngleXU=0 Radius=35 StartAngle=5.29641 EndAngle=7.26996
    g4: LineSegment StartX=999.298 StartY=45.8011 StartZ=0 EndX=930 EndY=0 EndZ=0
    g5: LineSegment StartX=930 StartY=0 StartZ=0 EndX=900 EndY=0 EndZ=0
    g6: Circle CenterX=980 CenterY=75 CenterZ=0 NormalX=0 NormalY=0 NormalZ=1 AngleXU=0 Radius=15
  constraints (19):
    c: Vertical(g0)
    c: Coincident(g0,g1)
    c: Horizontal(g1)
    c: Coincident(g1,g2)
    c: Tangent(g2,g3) = 1.5708
    c: Coincident(g4,g5)
    c: Coincident(g5,g0)
    c: Horizontal(g5)
    c: Coincident(g6,g3)
    c: DistanceY(g0,g0) = 150
    c: DistanceX(g-1,g0) = 900
    c: PointOnObject(g0,g-1)
    c: Vertical(g4,g1)
    c: DistanceX(g0,g3) = 80
    c: Tangent(g3,g4) = 1.5708
    c: DistanceY(g3,g1) = 75
    c: Radius(g6) = 15
    c: Radius(g3) = 35
    c: DistanceX(g0,g4) = 30
FEATURE [PartDesign::Pad] Pad
  Direction = (0,-1,-2e-16)
  Length = 48
  Length2 = 10
  Midplane = true
  Placement = pos=(0,0,0) rot=(1,0,0;1.5708rad)
  Profile = -> Sketch020
  ReferenceAxis = -> Sketch020 [N_Axis]
  Type = 0
FEATURE [Sketcher::SketchObject] Sketch021
  ExternalGeometry = -> [Pad]
  FullyConstrained = true
  MapMode = 5
  Placement = pos=(0,0,8.9e-14) rot=(1,0,0;3.14159rad)
  sketch-geometry (4):
    g0: LineSegment StartX=900 StartY=-8 StartZ=0 EndX=1050 EndY=-8 EndZ=0
    g1: LineSegment StartX=1050 StartY=-8 StartZ=0 EndX=1050 EndY=8 EndZ=0
    g2: LineSegment StartX=1050 StartY=8 StartZ=0 EndX=900 EndY=8 EndZ=0
    g3: LineSegment StartX=900 StartY=8 StartZ=0 EndX=900 EndY=-8 EndZ=0
  constraints (12):
    c: Coincident(g0,g1)
    c: Coincident(g1,g2)
    c: Coincident(g2,g3)
    c: Coincident(g3,g0)
    c: Horizontal(g0)
    c: Horizontal(g2)
    c: Vertical(g1)
    c: Vertical(g3)
    c: Distance(g1) = 16
    c: PointOnObject(g2,g-4)
    c: DistanceY(g2,g-4) = 16
    c: DistanceX(g2,g2) = 150
FEATURE [Part::Extrusion] Extrude008  label="Extrude007"
  Base = -> Sketch021
  Dir = (0,0,-1)
  DirMode = 2
  FaceMakerClass = Part::FaceMakerBullseye
  LengthFwd = 150
  LengthRev = 0
  Reversed = true
  Solid = true
  Symmetric = false
FEATURE [Part::Cut] Cut007
  Base = -> Pad
  Placement = pos=(0,-492,0) rot=(0,0,1;0rad)
  Tool = -> Extrude008
  expr: .Placement.Base.y = -Spreadsheet001.rw / 2 - 16
FEATURE [Part::Mirroring] Mirror006  label="Cut001 (mirrored)"
  Base = (0,0,400)
  Normal = (0,-1,0)
  Source = -> Cut007
FEATURE [Part::Compound] Compound004
  Links = -> [Mirror006,Cut007]
FEATURE [Part::FeaturePython] AngleSteel002  label="LShp001"  # WARN: FeaturePython — macro-defined, semantics opaque (R4)
  A = 75
  B = 75
  L = 2234.39
  Placement = pos=(-850,-932.5,1525) rot=(0,1,0;2.2794rad)
  Solid = true
  g0 = 7.85
  mass = 15.306
  size = 10
  standard = SS_Equal
  t = 6
  expr: .Placement.Base.x = -Spreadsheet001.W0 / 2 + Spreadsheet001.mb0 / 2
  expr: .Placement.Base.y = -Spreadsheet001.W0 / 2 - 32.5
  expr: .Placement.Base.z = Spreadsheet001.p0 + Spreadsheet001.hg
  expr: .Placement.Rotation.Angle = Spreadsheet001.sita + 90
  expr: L = Spreadsheet001.ll
FEATURE [Part::FeaturePython] Array008  # Draft array (typed FeaturePython)
  AlwaysSyncPlacement = false
  Angle = 360
  ArrayType = 0
  Axis = (0,0,1)
  Base = -> AngleSteel002
  Center = (0,0,0)
  Count = 3
  ExpandArray = false
  Fuse = false
  IntervalAxis = (0,0,0)
  IntervalX = (100,0,0)
  IntervalY = (0,100,0)
  IntervalZ = (0,0,1450)
  NumberCircles = 3
  NumberPolar = 5
  NumberX = 1
  NumberY = 1
  NumberZ = 3
  PlacementList = 3 placements: arithmetic series from (-850,-932.5,1525) step (0,0,1450) to (-850,-932.5,4425)
  RadialDistance = 50
  ScaleList = (3) [(1,1,1),(1,1,1),(1,1,1)]
  Symmetry = 1
  TangentialDistance = 25
  expr: .IntervalZ.z = Spreadsheet001.p0
  expr: NumberZ = Spreadsheet001.n0
FEATURE [Part::Compound] Compound005  label="Compound"
  Links = -> [Array006,Array008]
FEATURE [Part::FeaturePython] Array009  # Draft array (typed FeaturePython)
  AlwaysSyncPlacement = false
  Angle = 360
  ArrayType = 1
  Axis = (0,0,1)
  Base = -> Compound005
  Center = (0,0,2.67593e+15)
  Count = 4
  ExpandArray = false
  Fuse = false
  IntervalAxis = (0,0,0)
  IntervalX = (50,0,0)
  IntervalY = (0,50,0)
  IntervalZ = (0,0,50)
  NumberCircles = 3
  NumberPolar = 4
  NumberX = 2
  NumberY = 2
  NumberZ = 1
  PlacementList = 4 placements: [(0,0,0),(0,0,-0.5),(0,0,0),(0,0,0)]
  RadialDistance = 50
  ScaleList = (4) [(1,1,1),(1,1,1),(1,1,1),(1,1,1)]
  Symmetry = 1
  TangentialDistance = 25
FEATURE [Sketcher::SketchObject] Sketch022
  ExternalGeometry = -> [Compound004]
  FullyConstrained = true
  Placement = pos=(0,0,0) rot=(1,0,0;1.5708rad)
  expr: Constraints[17] = Spreadsheet001.p0
  sketch-geometry (7):
    g0: LineSegment StartX=900 StartY=1462.5 StartZ=0 EndX=900 EndY=1587.5 EndZ=0
    g1: LineSegment StartX=900 StartY=1587.5 StartZ=0 EndX=930 EndY=1587.5 EndZ=0
    g2: LineSegment StartX=930 StartY=1587.5 StartZ=0 EndX=995.018 EndY=1556.61 EndZ=0
    g3: ArcOfCircle CenterX=980 CenterY=1525 CenterZ=0 NormalX=0 NormalY=0 NormalZ=1 AngleXU=0 Radius=35 StartAngle=5.15587 EndAngle=7.41051
    g4: LineSegment StartX=995.018 StartY=1493.39 StartZ=0 EndX=930 EndY=1462.5 EndZ=0
    g5: LineSegment StartX=930 StartY=1462.5 StartZ=0 EndX=900 EndY=1462.5 EndZ=0
    g6: Circle CenterX=980 CenterY=1525 CenterZ=0 NormalX=0 NormalY=0 NormalZ=1 AngleXU=0 Radius=15
  constraints (19):
    c: Vertical(g0)
    c: Coincident(g0,g1)
    c: Horizontal(g1)
    c: Coincident(g1,g2)
    c: Tangent(g2,g3) = 1.5708
    c: Coincident(g4,g5)
    c: Coincident(g5,g0)
    c: Horizontal(g5)
    c: Coincident(g6,g3)
    c: Radius(g6) = 15
    c: Radius(g3) = 35
    c: DistanceX(g1,g1) = 30
    c: Distance(g3,g0) = 80
    c: Tangent(g3,g4) = 1.5708
    c: Equal(g5,g1)
    c: Equal(g4,g2)
    c: Distance(g0) = 125
    c: DistanceY(g-3,g3) = 1450
    c: Vertical(g-3,g3)
FEATURE [Part::Extrusion] Extrude009
  Base = -> Sketch022
  Dir = (0,-1,2e-16)
  DirMode = 2
  FaceMakerClass = Part::FaceMakerBullseye
  LengthFwd = 16
  LengthRev = 0
  Placement = pos=(0,-492,0) rot=(0,0,1;0rad)
  Solid = true
  Symmetric = true
  expr: .Placement.Base.y = -Spreadsheet001.rw / 2 - 16
FEATURE [Part::Mirroring] Mirror  label="Extrude (mirrored)"
  Base = (0,0,1500)
  Normal = (0,1,0)
  Source = -> Extrude009
FEATURE [Part::Compound] Compound006  label="Compound005"
  Links = -> [Mirror,Extrude009]
FEATURE [Part::Compound] Compound007  label="Compound006"
  Links = -> [Compound006,Compound004]
FEATURE [Part::Mirroring] Mirror007  label="Compound006 (mirrored)"
  Base = (0,0,-1000)
  Normal = (1,0,0)
  Source = -> Compound007
FEATURE [Part::Compound] Compound008  label="Compound007"
  Links = -> [Mirror007,Compound007]
FEATURE [Part::FeaturePython] ChannelSteel002  # WARN: FeaturePython — macro-defined, semantics opaque (R4)
  B = 75
  H = 150
  L = 1200
  Placement = pos=(500,0,4350) rot=(0,0,1;0rad)
  Solid = false
  g0 = 7.85
  mass = 0
  size = 4
  standard = SS
  t1 = 9
  t2 = 12.5
  expr: .Placement.Base.z = Spreadsheet001.L0 - 150
FEATURE [Part::Extrusion] Extrude010  label="Extrude008"
  Base = -> ChannelSteel002
  Dir = (0,1,0)
  DirMode = 2
  FaceMakerClass = Part::FaceMakerBullseye
  LengthFwd = 1334
  LengthRev = 0
  Solid = false
  Symmetric = true
FEATURE [Sketcher::SketchObject] Sketch023
  ExternalGeometry = -> [Extrude010]
  FullyConstrained = true
  MapMode = 5
  Placement = pos=(0,0,4500) rot=(0,0,1;0rad)
  Support = -> [Extrude010]
  sketch-geometry (3):
    g0: LineSegment StartX=500 StartY=667 StartZ=0 EndX=575 EndY=592 EndZ=0
    g1: LineSegment StartX=575 StartY=592 StartZ=0 EndX=575 EndY=667 EndZ=0
    g2: LineSegment StartX=575 StartY=667 StartZ=0 EndX=500 EndY=667 EndZ=0
  constraints (7):
    c: Coincident(g0,g1)
    c: Coincident(g1,g2)
    c: Coincident(g2,g0)
    c: Coincident(g1,g-3)
    c: PointOnObject(g0,g-4)
    c: Coincident(g0,g-3)
    c: Angle(g1,g0) = 0.785398
FEATURE [Part::Extrusion] Extrude011
  Base = -> Sketch023
  Dir = (0,0,1)
  DirMode = 2
  FaceMakerClass = Part::FaceMakerBullseye
  LengthFwd = 150
  LengthRev = 0
  Reversed = true
  Solid = true
  Symmetric = false
FEATURE [Part::Mirroring] Mirror008  label="Extrude009 (mirrored)"
  Base = (300,0,0)
  Normal = (0,1,0)
  Source = -> Extrude011
FEATURE [Part::Compound] Compound009  label="Compound008"
  Links = -> [Mirror008,Extrude011]
FEATURE [Part::Cut] Cut008  label="Cut002"
  Base = -> Extrude010
  Tool = -> Compound009
FEATURE [Part::FeaturePython] Array010  # Draft array (typed FeaturePython)
  AlwaysSyncPlacement = false
  Angle = 360
  ArrayType = 1
  Axis = (0,0,1)
  Base = -> Cut006
  Center = (0,0,0)
  Count = 4
  ExpandArray = false
  Fuse = false
  IntervalAxis = (0,0,0)
  IntervalX = (50,0,0)
  IntervalY = (0,50,0)
  IntervalZ = (0,0,50)
  NumberCircles = 3
  NumberPolar = 4
  NumberX = 2
  NumberY = 2
  NumberZ = 1
  PlacementList = 4 placements: [(-363,-857,75),(857,-363,75),(363,857,75),(-857,363,75)]
  RadialDistance = 50
  ScaleList = (4) [(1,1,1),(1,1,1),(1,1,1),(1,1,1)]
  Symmetry = 1
  TangentialDistance = 25
FEATURE [Part::Mirroring] Mirror009  label="Cut002 (mirrored)"
  Base = (0,-600,0)
  Normal = (1,0,0)
  Source = -> Cut008
FEATURE [Part::FeaturePython] ChannelSteel003  # WARN: FeaturePython — macro-defined, semantics opaque (R4)
  B = 75
  H = 150
  L = 1000
  Placement = pos=(-500,538,4425) rot=(0.57735,0.57735,0.57735;2.0944rad)
  Solid = true
  g0 = 7.85
  mass = 22.2541
  size = 4
  standard = SS
  t1 = 9
  t2 = 12.5
FEATURE [Part::FeaturePython] Array011  # Draft array (typed FeaturePython)
  AlwaysSyncPlacement = false
  Angle = 360
  ArrayType = 0
  Axis = (0,0,1)
  Base = -> Array010
  Center = (0,0,0)
  Count = 4
  ExpandArray = false
  Fuse = false
  IntervalAxis = (0,0,0)
  IntervalX = (100,0,0)
  IntervalY = (0,100,0)
  IntervalZ = (0,0,1450)
  NumberCircles = 3
  NumberPolar = 5
  NumberX = 1
  NumberY = 1
  NumberZ = 4
  PlacementList = 4 placements: arithmetic series from (0,0,0) step (0,0,1450) to (0,0,4350)
  RadialDistance = 50
  ScaleList = (4) [(1,1,1),(1,1,1),(1,1,1),(1,1,1)]
  Symmetry = 1
  TangentialDistance = 25
  expr: .IntervalZ.z = Spreadsheet001.p0
FEATURE [Part::Mirroring] Mirror010  label="ChannelSteel003 (mirrored)"
  Base = (-300,0,0)
  Normal = (0,-1,0)
  Source = -> ChannelSteel003
FEATURE [App::Part] Part002  label="centerCage"
  Group = -> [Spreadsheet001,ChannelSteel,Array006,AngleSteel,Array005,Sketch013,AngleSteel001,Sketch014,Sketch015,Sketch016,Sketch017,Sketch018,ChannelSteel001,Compound003,Sketch019,Mirror005,Extrude007,Cut006,Body,Sketch020,Pad,Sketch021,Extrude008,Cut007,Mirror006,Compound004,AngleSteel002,Array008,Compound005,Array009,Sketch022,Extrude009,Mirror,Compound006,Compound007,Mirror007,Compound008,Compound009,+11 more]
  Origin = -> Origin005
  Placement = pos=(0,0,1184.31) rot=(0,0,1;0rad)
FEATURE [Part::Compound] Compound010  label="centerCage001"
  Links = -> [Part002]
FEATURE [Part::Compound] Compound  label="centerPost001"
  Links = -> [Fusion,Revolve002,Cut005,Cut003,Revolve003]
FEATURE [App::Part] Part003  label="centerPost"
  Group = -> [Revolve003,Revolve001,Revolve004,circularEdge_002_mirror,circularEdge_002,circularEdge_003_mirror,circularEdge_003,circularEdge_004_mirror,Cut003,Cut004,Cut,Cut005,Extrude,Extrude004,Extrude005,Sketch004,Sketch002,Sketch003,Sketch001,Sketch011,Sketch009,Sketch010,Array003,Array,Array004,Revolve002,Revolve005,circularEdge_004,Cut001,Cut002,Extrude003,Extrude001,Extrude002,Sketch008,Sketch005,+9 more]
  Origin = -> Origin007
FEATURE [Part::FeaturePython] AngleSteel003  # WARN: FeaturePython — macro-defined, semantics opaque (R4)
  A = 75
  B = 75
  L = 1000
  Placement = pos=(0,0,0) rot=(0,0,1;1.5708rad)
  Solid = false
  g0 = 7.85
  mass = 0
  size = 10
  standard = SS_Equal
  t = 6
FEATURE [Spreadsheet::Sheet] Spreadsheet002
  cells = A2='L0; B2(L0)=6500; A3='H0; B3(H0)=1000; A4='h1; B4(h1)=300; A5='W0; B5(W0)=1000; A6='div n0; B6(n0)=7; A7='p0; B7(p0)=837.5; A8='sita; B8(sita)=47.6230565176811; A9='l2; B9(l2)=1304.37964182212; A10='lx; B10(lx)=20.2215118241758; A11='lz; B11(lz)=22.1605609032064; A12='beta; B12(beta)=5.7; A13='picketFence  pl; B13(pk)=1000
FEATURE [Sketcher::SketchObject] Sketch024
  FullyConstrained = true
  MapMode = 5
  Placement = pos=(0,0,0) rot=(1,0,0;1.5708rad)
  Support = -> [XZ_Plane009]
  expr: Constraints[12] = Spreadsheet002.L0
  expr: Constraints[15] = Spreadsheet002.h1
  expr: Constraints[16] = Spreadsheet002.H0
  sketch-geometry (6):
    g0: LineSegment StartX=0 StartY=0 StartZ=0 EndX=0 EndY=300 EndZ=0
    g1: LineSegment StartX=0 StartY=300 StartZ=0 EndX=700 EndY=1000 EndZ=0
    g2: LineSegment StartX=700 StartY=1000 StartZ=0 EndX=5800 EndY=1000 EndZ=0
    g3: LineSegment StartX=5800 StartY=1000 StartZ=0 EndX=6500 EndY=300 EndZ=0
    g4: LineSegment StartX=6500 StartY=300 StartZ=0 EndX=6500 EndY=0 EndZ=0
    g5: LineSegment StartX=6500 StartY=0 StartZ=0 EndX=0 EndY=0 EndZ=0
  constraints (18):
    c: PointOnObject(g0,g-2)
    c: PointOnObject(g0,g-2)
    c: Coincident(g0,g1)
    c: Coincident(g1,g2)
    c: Horizontal(g2)
    c: Coincident(g2,g3)
    c: Coincident(g3,g4)
    c: PointOnObject(g4,g-1)
    c: Vertical(g4)
    c: Coincident(g4,g5)
    c: Coincident(g5,g0)
    c: Horizontal(g5)
    c: Distance(g5) = 6500
    c: Angle(g-2,g1) = 2.35619
    c: Angle(g2,g3) = 2.35619
    c: DistanceY(g0,g0) = 300
    c: Distance(g2,g5) = 1000
    c: Equal(g4,g0)
FEATURE [Part::Sweep] Sweep
  Frenet = false
  Sections = -> [AngleSteel003]
  Solid = true
  Spine = -> Sketch024 [Edge6,Edge5,Edge4,Edge3,Edge2,Edge1]
  Transition = 1
FEATURE [Part::FeaturePython] AngleSteel004  # WARN: FeaturePython — macro-defined, semantics opaque (R4)
  A = 75
  B = 75
  L = 970
  Placement = pos=(737.5,43.5,15) rot=(0,0,1;1.5708rad)
  Solid = true
  g0 = 7.85
  mass = 6.6447
  size = 10
  standard = SS_Equal
  t = 6
  expr: .Placement.Base.x = Spreadsheet002.H0 - Spreadsheet002.h1 + 37.5
  expr: L = Spreadsheet002.H0 - 30
FEATURE [Part::FeaturePython] Array012  # Draft array (typed FeaturePython)
  AlwaysSyncPlacement = false
  Angle = 360
  ArrayType = 0
  Axis = (0,0,1)
  Base = -> AngleSteel004
  Center = (0,0,0)
  Count = 7
  ExpandArray = false
  Fuse = false
  IntervalAxis = (0,0,0)
  IntervalX = (837.5,0,0)
  IntervalY = (0,100,0)
  IntervalZ = (0,0,100)
  NumberCircles = 3
  NumberPolar = 5
  NumberX = 7
  NumberY = 1
  NumberZ = 1
  PlacementList = 7 placements: arithmetic series from (737.5,43.5,15) step (837.5,0,0) to (5762.5,43.5,15)
  RadialDistance = 50
  ScaleList = (7) [(1,1,1),(1,1,1),(1,1,1),(1,1,1),(1,1,1),(1,1,1),(1,1,1)]
  Symmetry = 1
  TangentialDistance = 25
  expr: .IntervalX.x = Spreadsheet002.p0
  expr: NumberX = Spreadsheet002.n0
FEATURE [Part::FeaturePython] AngleSteel005  # WARN: FeaturePython — macro-defined, semantics opaque (R4)
  A = 75
  B = 75
  L = 1264.38
  Placement = pos=(720.222,-37.5,977.839) rot=(0,1,0;2.40198rad)
  Solid = true
  g0 = 7.85
  mass = 8.66126
  size = 10
  standard = SS_Equal
  t = 6
  expr: .Placement.Base.x = Spreadsheet002.H0 - Spreadsheet002.h1 + Spreadsheet002.lx
  expr: .Placement.Base.z = Spreadsheet002.H0 - Spreadsheet002.lz
  expr: .Placement.Rotation.Angle = Spreadsheet002.sita + 90
  expr: L = Spreadsheet002.l2 - 40
FEATURE [Part::FeaturePython] Array013  # Draft array (typed FeaturePython)
  AlwaysSyncPlacement = false
  Angle = 360
  ArrayType = 0
  Axis = (0,0,1)
  Base = -> AngleSteel005
  Center = (0,0,0)
  Count = 6
  ExpandArray = false
  Fuse = false
  IntervalAxis = (0,0,0)
  IntervalX = (837.5,0,0)
  IntervalY = (0,100,0)
  IntervalZ = (0,0,100)
  NumberCircles = 3
  NumberPolar = 5
  NumberX = 6
  NumberY = 1
  NumberZ = 1
  PlacementList = 6 placements: arithmetic series from (720.222,-37.5,977.839) step (837.5,0,0) to (4907.72,-37.5,977.839)
  RadialDistance = 50
  ScaleList = (6) [(1,1,1),(1,1,1),(1,1,1),(1,1,1),(1,1,1),(1,1,1)]
  Symmetry = 1
  TangentialDistance = 25
  expr: .IntervalX.x = Spreadsheet002.p0
  expr: NumberX = Spreadsheet002.n0 - 1
FEATURE [Sketcher::SketchObject] Sketch025
  FullyConstrained = false
  Placement = pos=(0,0,0) rot=(1,0,0;1.5708rad)
  sketch-geometry (7):
    g0: LineSegment StartX=0 StartY=36.614 StartZ=0 EndX=0 EndY=161.614 EndZ=0
    g1: LineSegment StartX=0 StartY=161.614 StartZ=0 EndX=-30 EndY=161.614 EndZ=0
    g2: LineSegment StartX=-30 StartY=161.614 StartZ=0 EndX=-95.0179 EndY=130.728 EndZ=0
    g3: ArcOfCircle CenterX=-80 CenterY=99.114 CenterZ=0 NormalX=0 NormalY=0 NormalZ=1 AngleXU=0 Radius=35 StartAngle=2.01427 EndAngle=4.26891
    g4: LineSegment StartX=-95.0179 StartY=67.4997 StartZ=0 EndX=-30 EndY=36.614 EndZ=0
    g5: LineSegment StartX=-30 StartY=36.614 StartZ=0 EndX=0 EndY=36.614 EndZ=0
    g6: Circle CenterX=-80 CenterY=99.114 CenterZ=0 NormalX=0 NormalY=0 NormalZ=1 AngleXU=0 Radius=15
  constraints (18):
    c: Vertical(g0)
    c: Coincident(g0,g1)
    c: Horizontal(g1)
    c: Coincident(g1,g2)
    c: Tangent(g2,g3) = -1.5708
    c: Coincident(g4,g5)
    c: Coincident(g5,g0)
    c: Coincident(g6,g3)
    c: Horizontal(g5)
    c: PointOnObject(g0,g-2)
    c: DistanceY(g0,g0) = 125
    c: Equal(g1,g5)
    c: DistanceX(g1,g1) = 30
    c: Tangent(g3,g4) = -1.5708
    c: Distance(g3,g0) = 80
    c: Radius(g6) = 15
    c: Radius(g3) = 35
    c: Equal(g2,g4)
FEATURE [Part::Extrusion] Extrude012
  Base = -> Sketch025
  Dir = (0,-1,2e-16)
  DirMode = 2
  FaceMakerClass = Part::FaceMakerBullseye
  LengthFwd = 16
  LengthRev = 0
  Reversed = true
  Solid = true
  Symmetric = false
FEATURE [Part::FeaturePython] AngleSteel006  # WARN: FeaturePython — macro-defined, semantics opaque (R4)
  A = 75
  B = 75
  L = 850
  Placement = pos=(737.5,-425,962.5) rot=(0.57735,-0.57735,-0.57735;4.18879rad)
  Solid = true
  g0 = 7.85
  mass = 5.82268
  size = 10
  standard = SS_Equal
  t = 6
  expr: .Placement.Base.x = Spreadsheet002.H0 - Spreadsheet002.h1 + 37.5
  expr: .Placement.Base.y = -Spreadsheet002.W0 / 2 + 75
  expr: .Placement.Base.z = Spreadsheet002.H0 - 37.5
  expr: L = Spreadsheet002.W0 - 150
FEATURE [Sketcher::SketchObject] Sketch026
  ExternalGeometry = -> [Sketch024,AngleSteel006]
  FullyConstrained = false
  Placement = pos=(0,0,0) rot=(1,0,0;1.5708rad)
  expr: Constraints[12] = (Spreadsheet002.L0 - (Spreadsheet002.H0 - Spreadsheet002.h1)) / (Spreadsheet002.n0 - 1) - 150
  sketch-geometry (6):
    g0: LineSegment StartX=1716.67 StartY=1000 StartZ=0 EndX=1716.67 EndY=1030 EndZ=0
    g1: LineSegment StartX=1716.67 StartY=1030 StartZ=0 EndX=1568.84 EndY=1113.23 EndZ=0
    g2: ArcOfCircle CenterX=1551.67 CenterY=1082.73 CenterZ=0 NormalX=0 NormalY=0 NormalZ=1 AngleXU=0 Radius=35 StartAngle=1.05803 EndAngle=3.14159
    g3: Circle CenterX=1551.67 CenterY=1082.73 CenterZ=0 NormalX=0 NormalY=0 NormalZ=1 AngleXU=0 Radius=15
    g4: LineSegment StartX=1516.67 StartY=1082.73 StartZ=0 EndX=1516.67 EndY=1000 EndZ=0
    g5: LineSegment StartX=1516.67 StartY=1000 StartZ=0 EndX=1716.67 EndY=1000 EndZ=0
  constraints (15):
    c: Coincident(g0,g1)
    c: Tangent(g1,g2) = -1.5708
    c: Coincident(g3,g2)
    c: Vertical(g0)
    c: DistanceY(g0,g0) = 30
    c: Radius(g3) = 15
    c: Radius(g2) = 35
    c: DistanceX(g2,g0) = 200
    c: PointOnObject(g4,g-3)
    c: PointOnObject(g0,g-3)
    c: Coincident(g5,g4)
    c: Coincident(g5,g0)
    c: DistanceX(g-4,g4) = 816.667
    c: Vertical(g4)
    c: Tangent(g4,g2) = -1.5708
FEATURE [Part::Extrusion] Extrude013
  Base = -> Sketch026
  Dir = (0,-1,2e-16)
  DirMode = 2
  FaceMakerClass = Part::FaceMakerBullseye
  LengthFwd = 16
  LengthRev = 0
  Reversed = true
  Solid = true
  Symmetric = false
FEATURE [Part::Compound] Compound013
  Links = -> [Sweep,Array012,Array013,Extrude012,Extrude013]
  Placement = pos=(0,-500,0) rot=(0,0,1;0rad)
  expr: .Placement.Base.y = -Spreadsheet002.W0 / 2
FEATURE [Part::Mirroring] Mirror011  label="Compound (mirrored)"
  Base = (0,-8.88e-14,400)
  Normal = (0,-1,0)
  Source = -> Compound013
FEATURE [Part::FeaturePython] Array014  # Draft array (typed FeaturePython)
  AlwaysSyncPlacement = false
  Angle = 360
  ArrayType = 0
  Axis = (0,0,1)
  Base = -> AngleSteel006
  Center = (0,0,0)
  Count = 6
  ExpandArray = false
  Fuse = false
  IntervalAxis = (0,0,0)
  IntervalX = (837.5,0,0)
  IntervalY = (0,100,0)
  IntervalZ = (0,0,100)
  NumberCircles = 3
  NumberPolar = 5
  NumberX = 6
  NumberY = 1
  NumberZ = 1
  PlacementList = 6 placements: arithmetic series from (737.5,-425,962.5) step (837.5,0,0) to (4925,-425,962.5)
  RadialDistance = 50
  ScaleList = (6) [(1,1,1),(1,1,1),(1,1,1),(1,1,1),(1,1,1),(1,1,1)]
  Symmetry = 1
  TangentialDistance = 25
  expr: .IntervalX.x = <<Spreadsheet002>>.p0
  expr: NumberX = Spreadsheet002.n0 - 1
FEATURE [Part::FeaturePython] Clone  label="AngleSteel007"  # Draft clone (typed FeaturePython)
  AttacherType = Attacher::AttachEngine3D
  Fuse = false
  Objects = -> [AngleSteel006]
  Placement = pos=(5762.5,-425,962.5) rot=(0,0.707107,0.707107;3.14159rad)
  Scale = (1,1,1)
  expr: .Placement.Base.x = Spreadsheet002.L0 - (Spreadsheet002.H0 - Spreadsheet002.h1) - 37.5
  expr: .Placement.Base.y = -Spreadsheet002.W0 / 2 + 75
  expr: .Placement.Base.z = Spreadsheet002.H0 - 37.5
FEATURE [Part::FeaturePython] Clone001  label="AngleSteel008"  # Draft clone (typed FeaturePython)
  AttacherType = Attacher::AttachEngine3D
  Fuse = false
  Objects = -> [AngleSteel006]
  Placement = pos=(737.5,-425,37.5) rot=(-1,0,0;1.5708rad)
  Scale = (1,1,1)
  expr: .Placement.Base.x = Spreadsheet002.H0 - Spreadsheet002.h1 + 37.5
  expr: .Placement.Base.y = -Spreadsheet002.W0 / 2 + 75
FEATURE [Part::FeaturePython] Array015  # Draft array (typed FeaturePython)
  AlwaysSyncPlacement = false
  Angle = 360
  ArrayType = 0
  Axis = (0,0,1)
  Base = -> Clone001
  Center = (0,0,0)
  Count = 7
  ExpandArray = false
  Fuse = false
  IntervalAxis = (0,0,0)
  IntervalX = (837.5,0,0)
  IntervalY = (0,100,0)
  IntervalZ = (0,0,100)
  NumberCircles = 3
  NumberPolar = 5
  NumberX = 7
  NumberY = 1
  NumberZ = 1
  PlacementList = 7 placements: arithmetic series from (737.5,-425,37.5) step (837.5,0,0) to (5762.5,-425,37.5)
  RadialDistance = 50
  ScaleList = (7) [(1,1,1),(1,1,1),(1,1,1),(1,1,1),(1,1,1),(1,1,1),(1,1,1)]
  Symmetry = 1
  TangentialDistance = 25
  expr: .IntervalX.x = Spreadsheet002.p0
  expr: NumberX = Spreadsheet002.n0
FEATURE [Part::FeaturePython] Clone002  label="AngleSteel009"  # Draft clone (typed FeaturePython)
  AttacherType = Attacher::AttachEngine3D
  Fuse = false
  Objects = -> [AngleSteel006]
  Placement = pos=(6462.5,-425,37.54) rot=(0.57735,0.57735,0.57735;4.18879rad)
  Scale = (1,1,1)
  expr: .Placement.Base.x = Spreadsheet002.L0 - 37.5
  expr: .Placement.Base.y = -Spreadsheet002.W0 / 2 + 75
FEATURE [Part::FeaturePython] Clone003  label="AngleSteel010"  # Draft clone (typed FeaturePython)
  AttacherType = Attacher::AttachEngine3D
  Fuse = false
  Objects = -> [AngleSteel006]
  Placement = pos=(37.5,-425,37.5) rot=(-1,0,0;1.5708rad)
  Scale = (1,1,1)
  expr: .Placement.Base.y = -Spreadsheet002.W0 / 2 + 75
FEATURE [Part::FeaturePython] Clone004  label="AngleSteel011"  # Draft clone (typed FeaturePython)
  AttacherType = Attacher::AttachEngine3D
  Fuse = false
  Objects = -> [AngleSteel006]
  Placement = pos=(37.5,-425,262.5) rot=(0.57735,-0.57735,-0.57735;4.18879rad)
  Scale = (1,1,1)
  expr: .Placement.Base.y = -Spreadsheet002.W0 / 2 + 75
  expr: .Placement.Base.z = Spreadsheet002.h1 - 37.5
FEATURE [Sketcher::SketchObject] Sketch027
  FullyConstrained = false
  Placement = pos=(0,0,0) rot=(1,0,0;1.5708rad)
  expr: Constraints[6] = Spreadsheet002.beta
  sketch-geometry (3):
    g0: LineSegment StartX=0 StartY=0 StartZ=0 EndX=64.1183 EndY=6.39986 EndZ=0
    g1: LineSegment StartX=64.1183 StartY=6.39986 StartZ=0 EndX=64.1183 EndY=0 EndZ=0
    g2: LineSegment StartX=64.1183 StartY=0 StartZ=0 EndX=0 EndY=0 EndZ=0
  constraints (7):
    c: Coincident(g-1,g0)
    c: Coincident(g0,g1)
    c: Vertical(g1)
    c: Coincident(g1,g2)
    c: Coincident(g2,g0)
    c: Horizontal(g2)
    c: Angle(g2,g0) = 0.0994838
FEATURE [Part::Extrusion] Extrude014
  Base = -> Sketch027
  Dir = (0,-1,-3e-16)
  DirMode = 2
  FaceMakerClass = Part::FaceMakerBullseye
  LengthFwd = 50
  LengthRev = 0
  Solid = true
  Symmetric = true
FEATURE [Part::FeaturePython] AngleSteel007  label="AngleSteel012"  # WARN: FeaturePython — macro-defined, semantics opaque (R4)
  A = 50
  B = 50
  L = 200
  Placement = pos=(25,0,0) rot=(0,0,1;0rad)
  Solid = true
  g0 = 7.85
  mass = 0.88607
  size = 7
  standard = SS_Equal
  t = 6
FEATURE [Part::Cut] Cut009
  Base = -> AngleSteel007
  Placement = pos=(700,0,1000) rot=(0,1,0;0.099484rad)
  Tool = -> Extrude014
  expr: .Placement.Base.x = Spreadsheet002.H0 - Spreadsheet002.h1
  expr: .Placement.Base.z = Spreadsheet002.H0
FEATURE [Part::FeaturePython] Array016  # Draft array (typed FeaturePython)
  AlwaysSyncPlacement = false
  Angle = 360
  ArrayType = 0
  Axis = (0,0,1)
  Base = -> Cut009
  Center = (0,0,0)
  Count = 7
  ExpandArray = false
  Fuse = false
  IntervalAxis = (0,0,0)
  IntervalX = (837.5,0,0)
  IntervalY = (0,100,0)
  IntervalZ = (0,0,100)
  NumberCircles = 3
  NumberPolar = 5
  NumberX = 7
  NumberY = 1
  NumberZ = 1
  PlacementList = 7 placements: arithmetic series from (700,0,1000) step (837.5,0,0) to (5725,0,1000)
  RadialDistance = 50
  ScaleList = (7) [(1,1,1),(1,1,1),(1,1,1),(1,1,1),(1,1,1),(1,1,1),(1,1,1)]
  Symmetry = 1
  TangentialDistance = 25
  expr: .IntervalX.x = Spreadsheet002.p0
  expr: NumberX = Spreadsheet002.n0
FEATURE [Part::FeaturePython] AngleSteel008  label="AngleSteel013"  # WARN: FeaturePython — macro-defined, semantics opaque (R4)
  A = 50
  B = 50
  L = 1000
  Placement = pos=(25,0,0) rot=(0,0,1;1.5708rad)
  Solid = true
  g0 = 7.85
  mass = 4.43035
  size = 7
  standard = SS_Equal
  t = 6
FEATURE [App::Part] Part005
  Group = -> [AngleSteel008]
  Origin = -> Origin010
  Placement = pos=(700.993,50,1010) rot=(0,1,0;0.099484rad)
  expr: .Placement.Base.x = Spreadsheet002.H0 - Spreadsheet002.h1 + 10 * sin(Spreadsheet002.beta)
FEATURE [Part::FeaturePython] Array017  # Draft array (typed FeaturePython)
  AlwaysSyncPlacement = false
  Angle = 360
  ArrayType = 0
  Axis = (0,0,1)
  Base = -> Part005
  Center = (0,0,0)
  Count = 7
  ExpandArray = false
  Fuse = false
  IntervalAxis = (0,0,0)
  IntervalX = (837.5,0,0)
  IntervalY = (0,100,0)
  IntervalZ = (0,0,100)
  NumberCircles = 3
  NumberPolar = 5
  NumberX = 7
  NumberY = 1
  NumberZ = 1
  PlacementList = 7 placements: arithmetic series from (700.993,50,1010) step (837.5,0,0) to (5725.99,50,1010)
  RadialDistance = 50
  ScaleList = (7) [(1,1,1),(1,1,1),(1,1,1),(1,1,1),(1,1,1),(1,1,1),(1,1,1)]
  Symmetry = 1
  TangentialDistance = 25
  expr: .IntervalX.x = Spreadsheet002.p0
FEATURE [Sketcher::SketchObject] Sketch028
  FullyConstrained = true
  Placement = pos=(0,0,0) rot=(1,0,0;1.5708rad)
  expr: Constraints[11] = Spreadsheet002.beta
  expr: Constraints[1] = Spreadsheet002.H0 + Spreadsheet002.pk / cos(Spreadsheet002.beta)
  expr: Constraints[2] = Spreadsheet002.H0 - Spreadsheet002.h1 + (Spreadsheet002.pk + 10) * sin(Spreadsheet002.beta)
  expr: Constraints[3] = Spreadsheet002.L0
  sketch-geometry (4):
    g0: LineSegment StartX=800.313 StartY=2004.97 StartZ=0 EndX=7300.31 EndY=1356.18 EndZ=0
    g1: LineSegment StartX=7300.31 StartY=1356.18 StartZ=0 EndX=7300.31 EndY=2014.97 EndZ=0
    g2: LineSegment StartX=800.313 StartY=2004.97 StartZ=0 EndX=800.313 EndY=2014.97 EndZ=0
    g3: LineSegment StartX=800.313 StartY=2014.97 StartZ=0 EndX=7300.31 EndY=2014.97 EndZ=0
  constraints (12):
    c: Coincident(g0,g1)
    c: DistanceY(g-1,g0) = 2004.97
    c: DistanceX(g-1,g0) = 800.313
    c: DistanceX(g0,g1) = 6500
    c: Vertical(g1)
    c: Coincident(g0,g2)
    c: Vertical(g2)
    c: Coincident(g2,g3)
    c: Horizontal(g3)
    c: Coincident(g1,g3)
    c: DistanceY(g2,g2) = 10
    c: Angle(g0,g3) = 0.0994838
FEATURE [Part::Extrusion] Extrude015
  Base = -> Sketch028
  Dir = (0,-1,-3e-16)
  DirMode = 2
  FaceMakerClass = Part::FaceMakerBullseye
  LengthFwd = 200
  LengthRev = 0
  Solid = true
  Symmetric = true
FEATURE [Part::Cut] Cut010
  Base = -> Array017
  Tool = -> Extrude015
FEATURE [Part::Compound] Compound014  label="rake"
  Links = -> [Mirror011,Array014,Clone,Array015,Clone002,Clone003,Clone004,Array016,Cut010,Compound013]
  Placement = pos=(1060,0,960.196) rot=(0,0,1;0rad)
FEATURE [Part::Feature] Part__Feature  label="終沈躯体右_1500 v16"
  shape: bbox 17720 x 9400 x 6410 mm, 67 faces (baked)
FEATURE [Part::Feature] Part__Feature001  label="終沈躯体右_1500 v017"
  shape: bbox 17720 x 8350 x 6410 mm, 38 faces (baked)
FEATURE [Part::FeaturePython] AngleSteel009  label="AngleSteel"  # WARN: FeaturePython — macro-defined, semantics opaque (R4)
  A = 75
  B = 75
  L = 1000
  Placement = pos=(0,0,0) rot=(0.707107,0.707107,0;3.14159rad)
  Solid = false
  g0 = 7.85
  mass = 0
  size = 10
  standard = SS_Equal
  t = 6
FEATURE [Part::Extrusion] Extrude016
  Base = -> AngleSteel009
  Dir = (1,4e-16,1e-16)
  DirMode = 2
  FaceMakerClass = Part::FaceMakerBullseye
  LengthFwd = 1600
  LengthRev = 0
  Solid = false
  Symmetric = true
FEATURE [Sketcher::SketchObject] Sketch029
  ExternalGeometry = -> [Extrude016]
  FullyConstrained = false
  MapMode = 5
  Placement = pos=(0,-3.3e-15,0) rot=(1,0,0;1.5708rad)
  Support = -> [Extrude016]
  sketch-geometry (8):
    g0: Circle CenterX=-700 CenterY=-40.4478 CenterZ=0 NormalX=0 NormalY=0 NormalZ=1 AngleXU=0 Radius=7
    g1: Circle CenterX=700 CenterY=-39.6228 CenterZ=0 NormalX=0 NormalY=0 NormalZ=1 AngleXU=0 Radius=7
    g2: Circle CenterX=-500 CenterY=-40.4478 CenterZ=0 NormalX=0 NormalY=0 NormalZ=1 AngleXU=0 Radius=7
    g3: Circle CenterX=-299.492 CenterY=-40.4478 CenterZ=0 NormalX=0 NormalY=0 NormalZ=1 AngleXU=0 Radius=7
    g4: Circle CenterX=-99.2385 CenterY=-40.4478 CenterZ=0 NormalX=0 NormalY=0 NormalZ=1 AngleXU=0 Radius=7
    g5: Circle CenterX=101.015 CenterY=-40.4478 CenterZ=0 NormalX=0 NormalY=0 NormalZ=1 AngleXU=0 Radius=7
    g6: Circle CenterX=301.269 CenterY=-40.4478 CenterZ=0 NormalX=0 NormalY=0 NormalZ=1 AngleXU=0 Radius=7
    g7: Circle CenterX=501.523 CenterY=-40.4478 CenterZ=0 NormalX=0 NormalY=0 NormalZ=1 AngleXU=0 Radius=7
  constraints (11):
    c: Diameter(g0) = 14
    c: Diameter(g1) = 14
    c: DistanceX(g-3,g0) = 100
    c: DistanceX(g1,g-4) = 100
    c: Equal(g0,g2) = 14
    c: Equal(g0,g3) = 14
    c: Equal(g0,g4) = 14
    c: Equal(g0,g5) = 14
    c: Equal(g0,g6) = 14
    c: Equal(g0,g7) = 14
    c: DistanceX(g0,g2) = 200
FEATURE [Part::Extrusion] Extrude017
  Base = -> Sketch029
  Dir = (4e-16,-1,2e-16)
  DirMode = 2
  FaceMakerClass = Part::FaceMakerBullseye
  LengthFwd = 10
  LengthRev = 0
  Reversed = true
  Solid = true
  Symmetric = false
FEATURE [Part::Cut] Cut011  label="angle"
  Base = -> Extrude016
  Tool = -> Extrude017
FEATURE [Sketcher::SketchObject] Sketch030
  FullyConstrained = false
  Placement = pos=(0,0,0) rot=(1,0,0;1.5708rad)
  sketch-geometry (67):
    g0: LineSegment StartX=-800 StartY=-70 StartZ=0 EndX=-800 EndY=70 EndZ=0
    g1: LineSegment StartX=-800 StartY=70 StartZ=0 EndX=800 EndY=70 EndZ=0
    g2: LineSegment StartX=800 StartY=70 StartZ=0 EndX=800 EndY=-70 EndZ=0
    g3: LineSegment StartX=800 StartY=-70 StartZ=0 EndX=-800 EndY=-70 EndZ=0
    g4: GeomPoint X=0 Y=0 Z=0
    g5: Circle CenterX=-700 CenterY=40 CenterZ=0 NormalX=0 NormalY=0 NormalZ=1 AngleXU=0 Radius=7
    g6: Circle CenterX=100 CenterY=40 CenterZ=0 NormalX=0 NormalY=0 NormalZ=1 AngleXU=0 Radius=7
    g7: Circle CenterX=-500 CenterY=40 CenterZ=0 NormalX=0 NormalY=0 NormalZ=1 AngleXU=0 Radius=7
    g8: Circle CenterX=-300 CenterY=40 CenterZ=0 NormalX=0 NormalY=0 NormalZ=1 AngleXU=0 Radius=7
    g9: Circle CenterX=-100 CenterY=40 CenterZ=0 NormalX=0 NormalY=0 NormalZ=1 AngleXU=0 Radius=7
    g10: Circle CenterX=300 CenterY=40 CenterZ=0 NormalX=0 NormalY=0 NormalZ=1 AngleXU=0 Radius=7
    g11: Circle CenterX=500 CenterY=40 CenterZ=0 NormalX=0 NormalY=0 NormalZ=1 AngleXU=0 Radius=7
    g12: Circle CenterX=700 CenterY=40 CenterZ=0 NormalX=0 NormalY=0 NormalZ=1 AngleXU=0 Radius=7
    g13: LineSegment StartX=-743 StartY=5 StartZ=0 EndX=-743 EndY=-45 EndZ=0
    g14: ArcOfCircle CenterX=-750 CenterY=-45 CenterZ=0 NormalX=0 NormalY=0 NormalZ=1 AngleXU=0 Radius=7 StartAngle=3.14159 EndAngle=6.28319
    g15: LineSegment StartX=-757 StartY=-45 StartZ=0 EndX=-757 EndY=5 EndZ=0
    g16: ArcOfCircle CenterX=-750 CenterY=5 CenterZ=0 NormalX=0 NormalY=0 NormalZ=1 AngleXU=0 Radius=7 StartAngle=2e-16 EndAngle=3.14159
    g17: LineSegment StartX=-593 StartY=5 StartZ=0 EndX=-593 EndY=-45 EndZ=0
    g18: ArcOfCircle CenterX=-600 CenterY=-45 CenterZ=0 NormalX=0 NormalY=0 NormalZ=1 AngleXU=0 Radius=7 StartAngle=3.14159 EndAngle=6.28319
    g19: LineSegment StartX=-607 StartY=-45 StartZ=0 EndX=-607 EndY=5 EndZ=0
    g20: ArcOfCircle CenterX=-600 CenterY=5 CenterZ=0 NormalX=0 NormalY=0 NormalZ=1 AngleXU=0 Radius=7 StartAngle=1e-16 EndAngle=3.14159
    g21: LineSegment StartX=-743 StartY=5 StartZ=0 EndX=-593 EndY=5 EndZ=0
    g22: LineSegment StartX=-443 StartY=5 StartZ=0 EndX=-443 EndY=-45 EndZ=0
    g23: ArcOfCircle CenterX=-450 CenterY=-45 CenterZ=0 NormalX=0 NormalY=0 NormalZ=1 AngleXU=0 Radius=7 StartAngle=3.14159 EndAngle=6.28319
    g24: LineSegment StartX=-457 StartY=-45 StartZ=0 EndX=-457 EndY=5 EndZ=0
    g25: ArcOfCircle CenterX=-450 CenterY=5 CenterZ=0 NormalX=0 NormalY=0 NormalZ=1 AngleXU=0 Radius=7 StartAngle=1e-16 EndAngle=3.14159
    g26: LineSegment StartX=-593 StartY=5 StartZ=0 EndX=-443 EndY=5 EndZ=0
    g27: LineSegment StartX=-293 StartY=5 StartZ=0 EndX=-293 EndY=-45 EndZ=0
    g28: ArcOfCircle CenterX=-300 CenterY=-45 CenterZ=0 NormalX=0 NormalY=0 NormalZ=1 AngleXU=0 Radius=7 StartAngle=3.14159 EndAngle=6.28319
    g29: LineSegment StartX=-307 StartY=-45 StartZ=0 EndX=-307 EndY=5 EndZ=0
    g30: ArcOfCircle CenterX=-300 CenterY=5 CenterZ=0 NormalX=0 NormalY=0 NormalZ=1 AngleXU=0 Radius=7 StartAngle=1e-16 EndAngle=3.14159
    g31: LineSegment StartX=-443 StartY=5 StartZ=0 EndX=-293 EndY=5 EndZ=0
    g32: LineSegment StartX=-143 StartY=5 StartZ=0 EndX=-143 EndY=-45 EndZ=0
    g33: ArcOfCircle CenterX=-150 CenterY=-45 CenterZ=0 NormalX=0 NormalY=0 NormalZ=1 AngleXU=0 Radius=7 StartAngle=3.14159 EndAngle=6.28319
    g34: LineSegment StartX=-157 StartY=-45 StartZ=0 EndX=-157 EndY=5 EndZ=0
    g35: ArcOfCircle CenterX=-150 CenterY=5 CenterZ=0 NormalX=0 NormalY=0 NormalZ=1 AngleXU=0 Radius=7 StartAngle=1e-16 EndAngle=3.14159
    g36: LineSegment StartX=-293 StartY=5 StartZ=0 EndX=-143 EndY=5 EndZ=0
    g37: LineSegment StartX=7 StartY=5 StartZ=0 EndX=7 EndY=-45 EndZ=0
    g38: ArcOfCircle CenterX=-3.42e-14 CenterY=-45 CenterZ=0 NormalX=0 NormalY=0 NormalZ=1 AngleXU=0 Radius=7 StartAngle=3.14159 EndAngle=6.28319
    g39: LineSegment StartX=-7 StartY=-45 StartZ=0 EndX=-7 EndY=5 EndZ=0
    g40: ArcOfCircle CenterX=-3.42e-14 CenterY=5 CenterZ=0 NormalX=0 NormalY=0 NormalZ=1 AngleXU=0 Radius=7 StartAngle=1e-16 EndAngle=3.14159
    g41: LineSegment StartX=-143 StartY=5 StartZ=0 EndX=7 EndY=5 EndZ=0
    g42: LineSegment StartX=157 StartY=5 StartZ=0 EndX=157 EndY=-45 EndZ=0
    g43: ArcOfCircle CenterX=150 CenterY=-45 CenterZ=0 NormalX=0 NormalY=0 NormalZ=1 AngleXU=0 Radius=7 StartAngle=3.14159 EndAngle=6.28319
    g44: LineSegment StartX=143 StartY=-45 StartZ=0 EndX=143 EndY=5 EndZ=0
    g45: ArcOfCircle CenterX=150 CenterY=5 CenterZ=0 NormalX=0 NormalY=0 NormalZ=1 AngleXU=0 Radius=7 StartAngle=1e-16 EndAngle=3.14159
    g46: LineSegment StartX=7 StartY=5 StartZ=0 EndX=157 EndY=5 EndZ=0
    g47: LineSegment StartX=307 StartY=5 StartZ=0 EndX=307 EndY=-45 EndZ=0
    g48: ArcOfCircle CenterX=300 CenterY=-45 CenterZ=0 NormalX=0 NormalY=0 NormalZ=1 AngleXU=0 Radius=7 StartAngle=3.14159 EndAngle=6.28319
    g49: LineSegment StartX=293 StartY=-45 StartZ=0 EndX=293 EndY=5 EndZ=0
    g50: ArcOfCircle CenterX=300 CenterY=5 CenterZ=0 NormalX=0 NormalY=0 NormalZ=1 AngleXU=0 Radius=7 StartAngle=1e-16 EndAngle=3.14159
    g51: LineSegment StartX=157 StartY=5 StartZ=0 EndX=307 EndY=5 EndZ=0
    g52: LineSegment StartX=457 StartY=5 StartZ=0 EndX=457 EndY=-45 EndZ=0
    g53: ArcOfCircle CenterX=450 CenterY=-45 CenterZ=0 NormalX=0 NormalY=0 NormalZ=1 AngleXU=0 Radius=7 StartAngle=3.14159 EndAngle=6.28319
    g54: LineSegment StartX=443 StartY=-45 StartZ=0 EndX=443 EndY=5 EndZ=0
    g55: ArcOfCircle CenterX=450 CenterY=5 CenterZ=0 NormalX=0 NormalY=0 NormalZ=1 AngleXU=0 Radius=7 StartAngle=2e-16 EndAngle=3.14159
    g56: LineSegment StartX=307 StartY=5 StartZ=0 EndX=457 EndY=5 EndZ=0
    g57: LineSegment StartX=607 StartY=5 StartZ=0 EndX=607 EndY=-45 EndZ=0
    g58: ArcOfCircle CenterX=600 CenterY=-45 CenterZ=0 NormalX=0 NormalY=0 NormalZ=1 AngleXU=0 Radius=7 StartAngle=3.14159 EndAngle=6.28319
    g59: LineSegment StartX=593 StartY=-45 StartZ=0 EndX=593 EndY=5 EndZ=0
    g60: ArcOfCircle CenterX=600 CenterY=5 CenterZ=0 NormalX=0 NormalY=0 NormalZ=1 AngleXU=0 Radius=7 StartAngle=1e-16 EndAngle=3.14159
    g61: LineSegment StartX=457 StartY=5 StartZ=0 EndX=607 EndY=5 EndZ=0
    g62: LineSegment StartX=757 StartY=5 StartZ=0 EndX=757 EndY=-45 EndZ=0
    g63: ArcOfCircle CenterX=750 CenterY=-45 CenterZ=0 NormalX=0 NormalY=0 NormalZ=1 AngleXU=0 Radius=7 StartAngle=3.14159 EndAngle=6.28319
    g64: LineSegment StartX=743 StartY=-45 StartZ=0 EndX=743 EndY=5 EndZ=0
    g65: ArcOfCircle CenterX=750 CenterY=5 CenterZ=0 NormalX=0 NormalY=0 NormalZ=1 AngleXU=0 Radius=7 StartAngle=1e-16 EndAngle=3.14159
    g66: LineSegment StartX=607 StartY=5 StartZ=0 EndX=757 EndY=5 EndZ=0
  constraints (160):
    c: Coincident(g0,g1)
    c: Coincident(g1,g2)
    c: Coincident(g2,g3)
    c: Coincident(g3,g0)
    c: Horizontal(g1)
    c: Horizontal(g3)
    c: Vertical(g0)
    c: Vertical(g2)
    c: Symmetric(g1,g0,g4)
    c: Coincident(g4,g-1)
    c: DistanceX(g1,g1) = 1600
    c: DistanceY(g2,g2) = 140
    c: Diameter(g5) = 14
    c: Diameter(g6) = 14
    c: DistanceX(g0,g5) = 100
    c: Distance(g5,g1) = 30
    c: Distance(g6,g1) = 30
    c: Equal(g5,g7) = 14
    c: Equal(g5,g8) = 14
    c: Equal(g5,g9) = 14
    c: Equal(g5,g10) = 14
    c: Equal(g5,g11) = 14
    c: Equal(g5,g12) = 14
    c: DistanceX(g5,g7) = 200
    c: DistanceX(g7,g8) = 200
    c: DistanceX(g8,g9) = 200
    c: DistanceX(g9,g6) = 200
    c: DistanceX(g6,g10) = 200
    c: DistanceX(g10,g11) = 200
    c: DistanceX(g11,g12) = 200
    c: Vertical(g13)
    c: Tangent(g13,g14) = 1.5708
    c: Vertical(g15)
    c: Tangent(g15,g16) = 1.5708
    c: DistanceY(g15,g15) = 50
    c: Tangent(g16,g13) = 1.5708
    c: Tangent(g14,g15) = 1.5708
    c: DistanceX(g15,g13) = 14
    c: Distance(g14,g3) = 25
    c: Distance(g14,g0) = 50
    c: Vertical(g17)
    c: Tangent(g17,g18) = 1.5708
    c: Vertical(g19)
    c: Tangent(g19,g20) = 1.5708
    c: Equal(g15,g19) = 50
    c: Tangent(g20,g17) = 1.5708
    c: Tangent(g18,g19) = 1.5708
    c: DistanceX(g19,g17) = 14
    c: Coincident(g13,g21)
    c: Coincident(g17,g21)
    c: Distance(g21) = 150
    c: Angle(g21) = 0
    c: Vertical(g22)
    c: Tangent(g22,g23) = 1.5708
    c: Vertical(g24)
    c: Tangent(g24,g25) = 1.5708
    c: Equal(g15,g24) = 50
    c: Tangent(g25,g22) = 1.5708
    c: Tangent(g23,g24) = 1.5708
    c: DistanceX(g24,g22) = 14
    c: Coincident(g17,g26)
    c: Coincident(g22,g26)
    c: Equal(g21,g26)
    c: Parallel(g26,g21)
    c: Vertical(g27)
    c: Tangent(g27,g28) = 1.5708
    c: Vertical(g29)
    c: Tangent(g29,g30) = 1.5708
    c: Equal(g15,g29) = 50
    c: Tangent(g30,g27) = 1.5708
    c: Tangent(g28,g29) = 1.5708
    c: DistanceX(g29,g27) = 14
    c: Coincident(g22,g31)
    c: Coincident(g27,g31)
    c: Equal(g21,g31)
    c: Parallel(g31,g21)
    c: Vertical(g32)
    c: Tangent(g32,g33) = 1.5708
    c: Vertical(g34)
    c: Tangent(g34,g35) = 1.5708
    c: Equal(g15,g34) = 50
    c: Tangent(g35,g32) = 1.5708
    c: Tangent(g33,g34) = 1.5708
    c: DistanceX(g34,g32) = 14
    c: Coincident(g27,g36)
    c: Coincident(g32,g36)
    c: Equal(g21,g36)
    c: Parallel(g36,g21)
    c: Vertical(g37)
    c: Tangent(g37,g38) = 1.5708
    c: Vertical(g39)
    c: Tangent(g39,g40) = 1.5708
    c: Equal(g15,g39) = 50
    c: Tangent(g40,g37) = 1.5708
    c: Tangent(g38,g39) = 1.5708
    c: DistanceX(g39,g37) = 14
    c: Coincident(g32,g41)
    c: Coincident(g37,g41)
    c: Equal(g21,g41)
    c: Parallel(g41,g21)
    c: Vertical(g42)
    c: Tangent(g42,g43) = 1.5708
    c: Vertical(g44)
    c: Tangent(g44,g45) = 1.5708
    c: Equal(g15,g44) = 50
    c: Tangent(g45,g42) = 1.5708
    c: Tangent(g43,g44) = 1.5708
    c: DistanceX(g44,g42) = 14
    c: Coincident(g37,g46)
    c: Coincident(g42,g46)
    c: Equal(g21,g46)
    c: Parallel(g46,g21)
    c: Vertical(g47)
    c: Tangent(g47,g48) = 1.5708
    c: Vertical(g49)
    c: Tangent(g49,g50) = 1.5708
    c: Equal(g15,g49) = 50
    c: Tangent(g50,g47) = 1.5708
    c: Tangent(g48,g49) = 1.5708
    c: DistanceX(g49,g47) = 14
    c: Coincident(g42,g51)
    c: Coincident(g47,g51)
    c: Equal(g21,g51)
    c: Parallel(g51,g21)
    c: Vertical(g52)
    c: Tangent(g52,g53) = 1.5708
    c: Vertical(g54)
    c: Tangent(g54,g55) = 1.5708
    c: Equal(g15,g54) = 50
    c: Tangent(g55,g52) = 1.5708
    c: Tangent(g53,g54) = 1.5708
    c: DistanceX(g54,g52) = 14
    c: Coincident(g47,g56)
    c: Coincident(g52,g56)
    c: Equal(g21,g56)
    c: Parallel(g56,g21)
    c: Vertical(g57)
    c: Tangent(g57,g58) = 1.5708
    c: Vertical(g59)
    c: Tangent(g59,g60) = 1.5708
    c: Equal(g15,g59) = 50
    c: Tangent(g60,g57) = 1.5708
    c: Tangent(g58,g59) = 1.5708
    c: DistanceX(g59,g57) = 14
    c: Coincident(g52,g61)
    c: Coincident(g57,g61)
    c: Equal(g21,g61)
    c: Parallel(g61,g21)
    c: Vertical(g62)
    c: Tangent(g62,g63) = 1.5708
    c: Vertical(g64)
    c: Tangent(g64,g65) = 1.5708
    c: Equal(g15,g64) = 50
    c: Tangent(g65,g62) = 1.5708
    c: Tangent(g63,g64) = 1.5708
    c: DistanceX(g64,g62) = 14
    c: Coincident(g57,g66)
    c: Coincident(g62,g66)
    c: Equal(g21,g66)
    c: Parallel(g66,g21)
FEATURE [Part::Extrusion] Extrude018  label="plate_1"
  Base = -> Sketch030
  Dir = (0,-1,-6e-16)
  DirMode = 2
  FaceMakerClass = Part::FaceMakerBullseye
  LengthFwd = 5
  LengthRev = 0
  Placement = pos=(1.14e-13,-2.99e-13,-80.4478) rot=(0,0,1;0rad)
  Solid = true
  Symmetric = false
FEATURE [Sketcher::SketchObject] Sketch031
  FullyConstrained = true
  Placement = pos=(0,0,0) rot=(1,0,0;1.5708rad)
  sketch-geometry (26):
    g0: LineSegment StartX=-800 StartY=-55 StartZ=0 EndX=-800 EndY=55 EndZ=0
    g1: LineSegment StartX=-800 StartY=55 StartZ=0 EndX=800 EndY=55 EndZ=0
    g2: LineSegment StartX=800 StartY=55 StartZ=0 EndX=800 EndY=-55 EndZ=0
    g3: LineSegment StartX=800 StartY=-55 StartZ=0 EndX=-800 EndY=-55 EndZ=0
    g4: GeomPoint X=0 Y=0 Z=0
    g5: Circle CenterX=-750 CenterY=25 CenterZ=0 NormalX=0 NormalY=0 NormalZ=1 AngleXU=0 Radius=7
    g6: Circle CenterX=-600 CenterY=25 CenterZ=0 NormalX=0 NormalY=0 NormalZ=1 AngleXU=0 Radius=7
    g7: LineSegment StartX=-750 StartY=25 StartZ=0 EndX=-600 EndY=25 EndZ=0
    g8: Circle CenterX=-450 CenterY=25 CenterZ=0 NormalX=0 NormalY=0 NormalZ=1 AngleXU=0 Radius=7
    g9: LineSegment StartX=-600 StartY=25 StartZ=0 EndX=-450 EndY=25 EndZ=0
    g10: Circle CenterX=-300 CenterY=25 CenterZ=0 NormalX=0 NormalY=0 NormalZ=1 AngleXU=0 Radius=7
    g11: LineSegment StartX=-450 StartY=25 StartZ=0 EndX=-300 EndY=25 EndZ=0
    g12: Circle CenterX=-150 CenterY=25 CenterZ=0 NormalX=0 NormalY=0 NormalZ=1 AngleXU=0 Radius=7
    g13: LineSegment StartX=-300 StartY=25 StartZ=0 EndX=-150 EndY=25 EndZ=0
    g14: Circle CenterX=1.11421e-10 CenterY=25 CenterZ=0 NormalX=0 NormalY=0 NormalZ=1 AngleXU=0 Radius=7
    g15: LineSegment StartX=-150 StartY=25 StartZ=0 EndX=1.11413e-10 EndY=25 EndZ=0
    g16: Circle CenterX=150 CenterY=25 CenterZ=0 NormalX=0 NormalY=0 NormalZ=1 AngleXU=0 Radius=7
    g17: LineSegment StartX=1.11421e-10 StartY=25 StartZ=0 EndX=150 EndY=25 EndZ=0
    g18: Circle CenterX=300 CenterY=25 CenterZ=0 NormalX=0 NormalY=0 NormalZ=1 AngleXU=0 Radius=7
    g19: LineSegment StartX=150 StartY=25 StartZ=0 EndX=300 EndY=25 EndZ=0
    g20: Circle CenterX=450 CenterY=25 CenterZ=0 NormalX=0 NormalY=0 NormalZ=1 AngleXU=0 Radius=7
    g21: LineSegment StartX=300 StartY=25 StartZ=0 EndX=450 EndY=25 EndZ=0
    g22: Circle CenterX=600 CenterY=25 CenterZ=0 NormalX=0 NormalY=0 NormalZ=1 AngleXU=0 Radius=7
    g23: LineSegment StartX=450 StartY=25 StartZ=0 EndX=600 EndY=25 EndZ=0
    g24: Circle CenterX=750 CenterY=25 CenterZ=0 NormalX=0 NormalY=0 NormalZ=1 AngleXU=0 Radius=7
    g25: LineSegment StartX=600 StartY=25 StartZ=0 EndX=750 EndY=25 EndZ=0
  constraints (65):
    c: Coincident(g0,g1)
    c: Coincident(g1,g2)
    c: Coincident(g2,g3)
    c: Coincident(g3,g0)
    c: Horizontal(g1)
    c: Horizontal(g3)
    c: Vertical(g0)
    c: Vertical(g2)
    c: Symmetric(g1,g0,g4)
    c: Coincident(g4,g-1)
    c: DistanceX(g1,g1) = 1600
    c: DistanceY(g2,g2) = 110
    c: Diameter(g5) = 14
    c: Distance(g5,g1) = 30
    c: Distance(g5,g0) = 50
    c: Equal(g5,g6) = 14
    c: Coincident(g5,g7)
    c: Coincident(g6,g7)
    c: Distance(g7) = 150
    c: Angle(g7) = 0
    c: Equal(g5,g8) = 14
    c: Coincident(g6,g9)
    c: Coincident(g8,g9)
    c: Equal(g7,g9)
    c: Parallel(g9,g7)
    c: Equal(g5,g10) = 14
    c: Coincident(g8,g11)
    c: Coincident(g10,g11)
    c: Equal(g7,g11)
    c: Parallel(g11,g7)
    c: Equal(g5,g12) = 14
    c: Coincident(g10,g13)
    c: Coincident(g12,g13)
    c: Equal(g7,g13)
    c: Parallel(g13,g7)
    c: Equal(g5,g14) = 14
    c: Coincident(g12,g15)
    c: Coincident(g14,g15)
    c: Equal(g7,g15)
    c: Parallel(g15,g7)
    c: Equal(g5,g16) = 14
    c: Coincident(g14,g17)
    c: Coincident(g16,g17)
    c: Equal(g7,g17)
    c: Parallel(g17,g7)
    c: Equal(g5,g18) = 14
    c: Coincident(g16,g19)
    c: Coincident(g18,g19)
    c: Equal(g7,g19)
    c: Parallel(g19,g7)
    c: Equal(g5,g20) = 14
    c: Coincident(g18,g21)
    c: Coincident(g20,g21)
    c: Equal(g7,g21)
    c: Parallel(g21,g7)
    c: Equal(g5,g22) = 14
    c: Coincident(g20,g23)
    c: Coincident(g22,g23)
    c: Equal(g7,g23)
    c: Parallel(g23,g7)
    c: Equal(g5,g24) = 14
    c: Coincident(g22,g25)
    c: Coincident(g24,g25)
    c: Equal(g7,g25)
    c: Parallel(g25,g7)
FEATURE [Part::Extrusion] Extrude019  label="rubberPlate"
  Base = -> Sketch031
  Dir = (0,-1,-3e-16)
  DirMode = 2
  FaceMakerClass = Part::FaceMakerBullseye
  LengthFwd = 10
  LengthRev = 0
  Placement = pos=(2.27e-13,-5,-125.45) rot=(0,0,1;0rad)
  Solid = true
  Symmetric = false
FEATURE [Sketcher::SketchObject] Sketch032
  FullyConstrained = true
  Placement = pos=(0,0,0) rot=(1,0,0;1.5708rad)
  sketch-geometry (26):
    g0: LineSegment StartX=-800 StartY=-25 StartZ=0 EndX=-800 EndY=25 EndZ=0
    g1: LineSegment StartX=-800 StartY=25 StartZ=0 EndX=800 EndY=25 EndZ=0
    g2: LineSegment StartX=800 StartY=25 StartZ=0 EndX=800 EndY=-25 EndZ=0
    g3: LineSegment StartX=800 StartY=-25 StartZ=0 EndX=-800 EndY=-25 EndZ=0
    g4: GeomPoint X=0 Y=0 Z=0
    g5: Circle CenterX=-750 CenterY=0 CenterZ=0 NormalX=0 NormalY=0 NormalZ=1 AngleXU=0 Radius=7
    g6: Circle CenterX=-600 CenterY=0 CenterZ=0 NormalX=0 NormalY=0 NormalZ=1 AngleXU=0 Radius=7
    g7: LineSegment StartX=-750 StartY=0 StartZ=0 EndX=-600 EndY=0 EndZ=0
    g8: Circle CenterX=-450 CenterY=0 CenterZ=0 NormalX=0 NormalY=0 NormalZ=1 AngleXU=0 Radius=7
    g9: LineSegment StartX=-600 StartY=0 StartZ=0 EndX=-450 EndY=0 EndZ=0
    g10: Circle CenterX=-300 CenterY=0 CenterZ=0 NormalX=0 NormalY=0 NormalZ=1 AngleXU=0 Radius=7
    g11: LineSegment StartX=-450 StartY=0 StartZ=0 EndX=-300 EndY=0 EndZ=0
    g12: Circle CenterX=-150 CenterY=0 CenterZ=0 NormalX=0 NormalY=0 NormalZ=1 AngleXU=0 Radius=7
    g13: LineSegment StartX=-300 StartY=0 StartZ=0 EndX=-150 EndY=0 EndZ=0
    g14: Circle CenterX=5.68e-14 CenterY=0 CenterZ=0 NormalX=0 NormalY=0 NormalZ=1 AngleXU=0 Radius=7
    g15: LineSegment StartX=-150 StartY=0 StartZ=0 EndX=5.68e-14 EndY=0 EndZ=0
    g16: Circle CenterX=150 CenterY=0 CenterZ=0 NormalX=0 NormalY=0 NormalZ=1 AngleXU=0 Radius=7
    g17: LineSegment StartX=5.68e-14 StartY=0 StartZ=0 EndX=150 EndY=0 EndZ=0
    g18: Circle CenterX=300 CenterY=0 CenterZ=0 NormalX=0 NormalY=0 NormalZ=1 AngleXU=0 Radius=7
    g19: LineSegment StartX=150 StartY=0 StartZ=0 EndX=300 EndY=0 EndZ=0
    g20: Circle CenterX=450 CenterY=0 CenterZ=0 NormalX=0 NormalY=0 NormalZ=1 AngleXU=0 Radius=7
    g21: LineSegment StartX=300 StartY=0 StartZ=0 EndX=450 EndY=0 EndZ=0
    g22: Circle CenterX=600 CenterY=0 CenterZ=0 NormalX=0 NormalY=0 NormalZ=1 AngleXU=0 Radius=7
    g23: LineSegment StartX=450 StartY=0 StartZ=0 EndX=600 EndY=0 EndZ=0
    g24: Circle CenterX=750 CenterY=0 CenterZ=0 NormalX=0 NormalY=0 NormalZ=1 AngleXU=0 Radius=7
    g25: LineSegment StartX=600 StartY=0 StartZ=0 EndX=750 EndY=0 EndZ=0
  constraints (65):
    c: Coincident(g0,g1)
    c: Coincident(g1,g2)
    c: Coincident(g2,g3)
    c: Coincident(g3,g0)
    c: Horizontal(g1)
    c: Horizontal(g3)
    c: Vertical(g0)
    c: Vertical(g2)
    c: Symmetric(g1,g0,g4)
    c: Coincident(g4,g-1)
    c: DistanceX(g1,g1) = 1600
    c: DistanceY(g2,g2) = 50
    c: PointOnObject(g5,g-1)
    c: Diameter(g5) = 14
    c: DistanceX(g0,g5) = 50
    c: Equal(g5,g6) = 14
    c: Coincident(g5,g7)
    c: Coincident(g6,g7)
    c: Distance(g7) = 150
    c: Angle(g7) = 0
    c: Equal(g5,g8) = 14
    c: Coincident(g6,g9)
    c: Coincident(g8,g9)
    c: Equal(g7,g9)
    c: Parallel(g9,g7)
    c: Equal(g5,g10) = 14
    c: Coincident(g8,g11)
    c: Coincident(g10,g11)
    c: Equal(g7,g11)
    c: Parallel(g11,g7)
    c: Equal(g5,g12) = 14
    c: Coincident(g10,g13)
    c: Coincident(g12,g13)
    c: Equal(g7,g13)
    c: Parallel(g13,g7)
    c: Equal(g5,g14) = 14
    c: Coincident(g12,g15)
    c: Coincident(g14,g15)
    c: Equal(g7,g15)
    c: Parallel(g15,g7)
    c: Equal(g5,g16) = 14
    c: Coincident(g14,g17)
    c: Coincident(g16,g17)
    c: Equal(g7,g17)
    c: Parallel(g17,g7)
    c: Equal(g5,g18) = 14
    c: Coincident(g16,g19)
    c: Coincident(g18,g19)
    c: Equal(g7,g19)
    c: Parallel(g19,g7)
    c: Equal(g5,g20) = 14
    c: Coincident(g18,g21)
    c: Coincident(g20,g21)
    c: Equal(g7,g21)
    c: Parallel(g21,g7)
    c: Equal(g5,g22) = 14
    c: Coincident(g20,g23)
    c: Coincident(g22,g23)
    c: Equal(g7,g23)
    c: Parallel(g23,g7)
    c: Equal(g5,g24) = 14
    c: Coincident(g22,g25)
    c: Coincident(g24,g25)
    c: Equal(g7,g25)
    c: Parallel(g25,g7)
FEATURE [Part::Extrusion] Extrude020  label="plate_2"
  Base = -> Sketch032
  Dir = (0,-1,-3e-16)
  DirMode = 2
  FaceMakerClass = Part::FaceMakerBullseye
  LengthFwd = 5
  LengthRev = 0
  Placement = pos=(0,-15,-100.45) rot=(0,0,1;0rad)
  Solid = true
  Symmetric = false
FEATURE [App::Part] Part007  label="blade"
  Group = -> [AngleSteel009,Extrude016,Extrude017,Sketch029,Cut011,Sketch030,Extrude018,Sketch031,Extrude019,Sketch032,Extrude020]
  Origin = -> Origin011
  Placement = pos=(1900,0,0) rot=(0,0,1;5.49779rad)
FEATURE [Part::FeaturePython] Array018  label="brade"  # Draft array (typed FeaturePython)
  AlwaysSyncPlacement = false
  Angle = 360
  ArrayType = 0
  Axis = (0,0,1)
  Base = -> Part007
  Center = (0,0,0)
  Count = 6
  ExpandArray = false
  Fuse = false
  IntervalAxis = (0,0,0)
  IntervalX = (1050,0,0)
  IntervalY = (0,100,0)
  IntervalZ = (0,0,100)
  NumberCircles = 3
  NumberPolar = 5
  NumberX = 6
  NumberY = 1
  NumberZ = 1
  Placement = pos=(0,0,960) rot=(0,0,1;0rad)
  PlacementList = 6 placements: arithmetic series from (1900,0,0) step (1050,0,0) to (7150,0,0)
  RadialDistance = 50
  ScaleList = (6) [(1,1,1),(1,1,1),(1,1,1),(1,1,1),(1,1,1),(1,1,1)]
  Symmetry = 1
  TangentialDistance = 25
FEATURE [App::Part] Part008  label="rake001"
  Group = -> [Part007,Array018,Part005,Extrude015,Sketch025,Sketch027,Sketch024,Sketch026,Sketch028,Array012,Array013,AngleSteel003,AngleSteel004,AngleSteel005,Clone,AngleSteel006,Compound013,Array014,Array015,Clone003,AngleSteel007,Clone002,Array016,Clone004,Array017,Clone001,Extrude012,Extrude013,Extrude014,Mirror011,Sweep,Cut009,Cut010,Compound014]
  Origin = -> Origin012
FEATURE [Part::Compound] Compound015  label="rake002"
  Links = -> [Part008]
  Placement = pos=(115.668,0.0843607,-96.3145) rot=(0,-1,0;0.104349rad)
FEATURE [Sketcher::SketchObject] Sketch033
  FullyConstrained = true
  MapMode = 5
  Placement = pos=(0,0,0) rot=(1,0,0;1.5708rad)
  expr: Constraints[10] = Spreadsheet003.L7 * 2
  expr: Constraints[9] = Spreadsheet003.B7
  sketch-geometry (4):
    g0: LineSegment StartX=90 StartY=23 StartZ=0 EndX=-8.967e-12 EndY=23 EndZ=0
    g1: ArcOfCircle CenterX=0 CenterY=0 CenterZ=0 NormalX=0 NormalY=0 NormalZ=1 AngleXU=0 Radius=23 StartAngle=1.5708 EndAngle=4.71239
    g2: LineSegment StartX=-9.439e-13 StartY=-23 StartZ=0 EndX=90 EndY=-23 EndZ=0
    g3: LineSegment StartX=90 StartY=-23 StartZ=0 EndX=90 EndY=23 EndZ=0
  constraints (11):
    c: Horizontal(g0)
    c: Tangent(g0,g1) = -1.5708
    c: PointOnObject(g1,g-2)
    c: Coincident(g1,g2)
    c: Horizontal(g2)
    c: Coincident(g2,g3)
    c: Coincident(g3,g0)
    c: Vertical(g3)
    c: Coincident(g-1,g1)
    c: DistanceX(g0,g0) = 90
    c: Distance(g3) = 46
FEATURE [PartDesign::Pad] Pad001
  Direction = (0,-1,2e-16)
  Length = 40
  Length2 = 10
  Midplane = true
  Placement = pos=(0,0,0) rot=(1,0,0;1.5708rad)
  Profile = -> Sketch033
  ReferenceAxis = -> Sketch033 [N_Axis]
  Type = 0
  expr: Length = Spreadsheet003.D7
FEATURE [Spreadsheet::Sheet] Spreadsheet003
  cells = A2='rodDia dia; B2(dia)=20; A3='length L0; B3(L0)=1550; B4='l; C4='l1; D4='a; E4='b; F4='c; G4='e; H4='f; I4='g; J4='h; K4='i; L4='r; A5='forkEndR; B5=120; D5=40; E5=16; F5=21; G5=24; H5=20; I5=60; J5=10; K5=20; L5=23; A6='turnBackle; B6=150; C6=28; D6=42; E6=23; F6=33; A7='forkEndL; B7=90; D7=40; E7=16; F7=20; G7=24; H7=20; I7=30; L7=23; A8=1; B8=2; C8=3; D8=4; E8=5; F8=6; G8=7; H8=8; I8=9; J8=10; K8=11; L8=12; A9='turnBackle; A10='d; B10='l; C10='l1; D10='a; E10='b; F10='c; A11=10; B11=75; C11=15; D11=24; E11=13; F11=17; A12=12; B12=100; C12=20; D12=30; E12=16; F12=22; A13=16; B13=125; C13=24; D13=36; E13=20; F13=27; A14=20; B14=150; C14=28; D14=42; E14=23; F14=33; A15=22; B15=175; C15=33; D15=48; E15=27; F15=37; A16=24; B16=200; C16=38; D16=54; E16=30; F16=42; A17=30; B17=250; C17=47; D17=66; E17=37; F17=52; A18='forkEnd_L; A19='d; B19='l; C19='a; D19='b; E19='c; F19='e; G19='f; H19='g; I19='r; A20=10; B20=50; C20=20; D20=7; E20=10; F20=12; G20=10; H20=15; I20=12; A21=12; B21=60; C21=25; D21=10; E21=13; F21=16; G21=13; H21=20; I21=15; A22=16; B22=75; C22=30; D22=13; E22=16; F22=20; G22=16; H22=25; I22=19; A23=20; B23=90; C23=40; D23=16; E23=20; F23=24; G23=20; H23=30; I23=23; A24=22; B24=100; C24=45; D24=20; E24=23; F24=28; G24=23; H24=35; I24=27; A25=24; B25=115; C25=50; D25=23; E25=26; F25=32; G25=26; H25=40; I25=30; A26=30; B26=140; C26=65; D26=30; E26=33; F26=40; G26=33; H26=50; I26=38; A27='forkEnd_R; A28='d; B28='l; C28='a; D28='b; E28='c; F28='r; G28='e; H28='f; I28='g; J28='h; K28='i; A29=10; B29=60; C29=20; D29=7; E29=11; F29=12; G29=12; H29=10; I29=30; J29=5; K29=10; A30=12; B30=80; +64 more cells
FEATURE [Sketcher::SketchObject] Sketch034
  FullyConstrained = true
  MapMode = 5
  Placement = pos=(0,-20,8.8e-15) rot=(1,0,0;1.5708rad)
  Support = -> [Pad001]
  expr: Constraints[1] = Spreadsheet003.F7 / 2
  sketch-geometry (1):
    g0: Circle CenterX=0 CenterY=0 CenterZ=0 NormalX=0 NormalY=0 NormalZ=1 AngleXU=0 Radius=10
  constraints (2):
    c: Coincident(g0,g-1)
    c: Radius(g0) = 10
FEATURE [Part::Extrusion] Extrude021
  Base = -> Sketch034
  Dir = (0,-1,4e-16)
  DirMode = 2
  FaceMakerClass = Part::FaceMakerBullseye
  LengthFwd = 65
  LengthRev = 0
  Reversed = true
  Solid = true
  Symmetric = false
FEATURE [Sketcher::SketchObject] Sketch035
  FullyConstrained = true
  Placement = pos=(0,0,0) rot=(1,0,0;1.5708rad)
  expr: Constraints[11] = Spreadsheet003.I5
  expr: Constraints[1] = Spreadsheet003.F5 / 2
  expr: Constraints[3] = Spreadsheet003.L5
  sketch-geometry (5):
    g0: Circle CenterX=0 CenterY=0 CenterZ=0 NormalX=0 NormalY=0 NormalZ=1 AngleXU=0 Radius=10.5
    g1: ArcOfCircle CenterX=0 CenterY=0 CenterZ=0 NormalX=0 NormalY=0 NormalZ=1 AngleXU=0 Radius=23 StartAngle=4.71239 EndAngle=7.85398
    g2: LineSegment StartX=-1.34e-14 StartY=23 StartZ=0 EndX=-60 EndY=23 EndZ=0
    g3: LineSegment StartX=-60 StartY=23 StartZ=0 EndX=-60 EndY=-23 EndZ=0
    g4: LineSegment StartX=-60 StartY=-23 StartZ=0 EndX=-7.1e-15 EndY=-23 EndZ=0
  constraints (12):
    c: Coincident(g0,g-1)
    c: Radius(g0) = 10.5
    c: Coincident(g1,g0)
    c: Radius(g1) = 23
    c: Horizontal(g2)
    c: Coincident(g2,g3)
    c: Vertical(g3)
    c: Coincident(g3,g4)
    c: Horizontal(g4)
    c: Tangent(g1,g2) = -1.5708
    c: Tangent(g1,g4) = -1.5708
    c: Distance(g2) = 60
FEATURE [Part::Extrusion] Extrude022
  Base = -> Sketch035
  Dir = (0,-1,2e-16)
  DirMode = 2
  FaceMakerClass = Part::FaceMakerBullseye
  LengthFwd = 40
  LengthRev = 0
  Solid = true
  Symmetric = true
  expr: LengthFwd = Spreadsheet003.D5
FEATURE [Sketcher::SketchObject] Sketch036
  ExternalGeometry = -> [Extrude022]
  FullyConstrained = true
  MapMode = 5
  Placement = pos=(0,5.1e-15,23) rot=(0,0,1;0rad)
  Support = -> [Extrude022]
  expr: Constraints[10] = Spreadsheet003.E5
  expr: Constraints[24] = Spreadsheet003.G5
  expr: Constraints[25] = Spreadsheet003.K5
  expr: Constraints[26] = Spreadsheet003.H5
  expr: Constraints[31] = Spreadsheet003.E5 / 2
  expr: Constraints[32] = Spreadsheet003.G5 / 2
  expr: Constraints[9] = Spreadsheet003.L5
  sketch-geometry (12):
    g0: LineSegment StartX=23 StartY=8 StartZ=0 EndX=-20 EndY=8 EndZ=0
    g1: LineSegment StartX=-21 StartY=12 StartZ=0 EndX=-39 EndY=12 EndZ=0
    g2: LineSegment StartX=-40 StartY=11 StartZ=0 EndX=-40 EndY=-11 EndZ=0
    g3: LineSegment StartX=-39 StartY=-12 StartZ=0 EndX=-21 EndY=-12 EndZ=0
    g4: LineSegment StartX=-20 StartY=-11 StartZ=0 EndX=-20 EndY=-8 EndZ=0
    g5: LineSegment StartX=-20 StartY=-8 StartZ=0 EndX=23 EndY=-8 EndZ=0
    g6: LineSegment StartX=23 StartY=-8 StartZ=0 EndX=23 EndY=8 EndZ=0
    g7: ArcOfCircle CenterX=-21 CenterY=11 CenterZ=0 NormalX=0 NormalY=0 NormalZ=1 AngleXU=0 Radius=1 StartAngle=6.28317 EndAngle=7.85398
    g8: ArcOfCircle CenterX=-21 CenterY=-11 CenterZ=0 NormalX=0 NormalY=0 NormalZ=1 AngleXU=0 Radius=1 StartAngle=4.71239 EndAngle=6.28319
    g9: ArcOfCircle CenterX=-39 CenterY=11 CenterZ=0 NormalX=0 NormalY=0 NormalZ=1 AngleXU=0 Radius=1 StartAngle=1.5708 EndAngle=3.14159
    g10: ArcOfCircle CenterX=-39 CenterY=-11 CenterZ=0 NormalX=0 NormalY=0 NormalZ=1 AngleXU=0 Radius=1 StartAngle=3.14159 EndAngle=4.71239
    g11: LineSegment StartX=-20 StartY=8 StartZ=0 EndX=-20 EndY=11 EndZ=0
  constraints (33):
    c: Horizontal(g0)
    c: Horizontal(g1)
    c: Vertical(g2)
    c: Horizontal(g3)
    c: Coincident(g4,g5)
    c: Horizontal(g5)
    c: Coincident(g5,g6)
    c: Coincident(g6,g0)
    c: Vertical(g6)
    c: DistanceX(g-1,g5) = 23
    c: Distance(g6) = 16
    c: Vertical(g4)
    c: Vertical(g4,g0)
    c: Tangent(g1,g7) = -1.5708
    c: Tangent(g4,g8) = -1.5708
    c: Tangent(g3,g8) = -1.5708
    c: Tangent(g2,g9) = -1.5708
    c: Tangent(g1,g9) = -1.5708
    c: Tangent(g3,g10) = -1.5708
    c: Tangent(g2,g10) = -1.5708
    c: Radius(g7) = 1
    c: Radius(g8) = 1
    c: Equal(g10,g9)
    c: Radius(g10) = 1
    c: DistanceY(g3,g1) = 24
    c: DistanceX(g-3,g2) = 20
    c: DistanceX(g4,g-1) = 20
    c: Equal(g3,g1)
    c: Coincident(g11,g0)
    c: Coincident(g11,g7)
    c: Vertical(g11)
    c: DistanceY(g-1,g0) = 8
    c: DistanceY(g-1,g1) = 12
FEATURE [Part::Extrusion] Extrude023
  Base = -> Sketch036
  Dir = (0,2e-16,1)
  DirMode = 2
  FaceMakerClass = Part::FaceMakerBullseye
  LengthFwd = 80
  LengthRev = 0
  Reversed = true
  Solid = true
  Symmetric = false
FEATURE [Part::Cut] Cut012  label="Cut003"
  Base = -> Extrude022
  Tool = -> Extrude023
FEATURE [Part::Cylinder] Cylinder  label="円柱"
  Angle = 360
  AttacherType = Attacher::AttachEngine3D
  FirstAngle = 0
  Height = 120
  Placement = pos=(-60,0,0) rot=(0,-1,0;1.5708rad)
  Radius = 10
  SecondAngle = 0
  expr: .Placement.Base.x = -Spreadsheet003.I5
  expr: Height = Spreadsheet003.B5
  expr: Radius = Spreadsheet003.dia / 2
FEATURE [Part::MultiFuse] Fusion001  label="forkEndR"
  Shapes = -> [Cut012,Cylinder]
FEATURE [Sketcher::SketchObject] Sketch037
  FullyConstrained = true
  Placement = pos=(0,0,0) rot=(1,0,0;1.5708rad)
  expr: Constraints[10] = Spreadsheet003.C6
  expr: Constraints[11] = Spreadsheet003.B6
  expr: Constraints[12] = Spreadsheet003.D6 / 2
  expr: Constraints[13] = Spreadsheet003.F6 / 2
  expr: Constraints[14] = Spreadsheet003.B6 / 2
  expr: Constraints[17] = Spreadsheet003.C6
  sketch-geometry (6):
    g0: LineSegment StartX=-75 StartY=0 StartZ=0 EndX=-75 EndY=16.5 EndZ=0
    g1: LineSegment StartX=-75 StartY=16.5 StartZ=0 EndX=-47 EndY=21 EndZ=0
    g2: LineSegment StartX=-47 StartY=21 StartZ=0 EndX=47 EndY=21 EndZ=0
    g3: LineSegment StartX=47 StartY=21 StartZ=0 EndX=75 EndY=16.5 EndZ=0
    g4: LineSegment StartX=75 StartY=16.5 StartZ=0 EndX=75 EndY=0 EndZ=0
    g5: LineSegment StartX=75 StartY=0 StartZ=0 EndX=-75 EndY=0 EndZ=0
  constraints (18):
    c: PointOnObject(g0,g-1)
    c: Vertical(g0)
    c: Coincident(g0,g1)
    c: Coincident(g1,g2)
    c: Horizontal(g2)
    c: Coincident(g2,g3)
    c: Coincident(g3,g4)
    c: PointOnObject(g4,g-1)
    c: Vertical(g4)
    c: Coincident(g4,g5)
    c: DistanceX(g2,g3) = 28
    c: DistanceX(g0,g3) = 150
    c: Distance(g1,g5) = 21
    c: Distance(g4) = 16.5
    c: DistanceX(g-1,g4) = 75
    c: Horizontal(g0,g3)
    c: Coincident(g5,g0)
    c: DistanceX(g0,g1) = 28
FEATURE [Part::Revolution] Revolve006  label="Revolve"
  Angle = 360
  Axis = (-1,0,0)
  AxisLink = -> Sketch037 [Edge6]
  Base = (-75,0,0)
  FaceMakerClass = Part::FaceMakerBullseye
  Solid = true
  Source = -> Sketch037
  Symmetric = false
FEATURE [Sketcher::SketchObject] Sketch038
  FullyConstrained = false
  Placement = pos=(0,0,0) rot=(0.57735,0.57735,0.57735;2.0944rad)
  expr: Constraints[16] = Spreadsheet003.F6
  expr: Constraints[17] = Spreadsheet003.F6 / 2
  sketch-geometry (8):
    g0: LineSegment StartX=-16.5 StartY=39.685 StartZ=0 EndX=-31.5 EndY=39.685 EndZ=0
    g1: LineSegment StartX=-31.5 StartY=39.685 StartZ=0 EndX=-31.5 EndY=-39.3666 EndZ=0
    g2: LineSegment StartX=-31.5 StartY=-39.3666 StartZ=0 EndX=-16.5 EndY=-39.3666 EndZ=0
    g3: LineSegment StartX=-16.5 StartY=-39.3666 StartZ=0 EndX=-16.5 EndY=39.685 EndZ=0
    g4: LineSegment StartX=16.5 StartY=39.685 StartZ=0 EndX=31.5 EndY=39.685 EndZ=0
    g5: LineSegment StartX=31.5 StartY=39.685 StartZ=0 EndX=31.5 EndY=-40.315 EndZ=0
    g6: LineSegment StartX=31.5 StartY=-40.315 StartZ=0 EndX=16.5 EndY=-40.315 EndZ=0
    g7: LineSegment StartX=16.5 StartY=-40.315 StartZ=0 EndX=16.5 EndY=39.685 EndZ=0
  constraints (22):
    c: Coincident(g0,g1)
    c: Coincident(g1,g2)
    c: Coincident(g2,g3)
    c: Coincident(g3,g0)
    c: Horizontal(g0)
    c: Horizontal(g2)
    c: Vertical(g1)
    c: Vertical(g3)
    c: Coincident(g4,g5)
    c: Coincident(g5,g6)
    c: Coincident(g6,g7)
    c: Coincident(g7,g4)
    c: Horizontal(g4)
    c: Horizontal(g6)
    c: Vertical(g5)
    c: Vertical(g7)
    c: DistanceX(g0,g4) = 33
    c: Distance(g-1,g7) = 16.5
    c: Distance(g5) = 80
    c: Distance(g4) = 15
    c: Distance(g0) = 15
    c: Horizontal(g0,g4)
FEATURE [Part::Extrusion] Extrude024
  Base = -> Sketch038
  Dir = (1,0,0)
  DirMode = 2
  FaceMakerClass = Part::FaceMakerBullseye
  LengthFwd = 300
  LengthRev = 0
  Solid = true
  Symmetric = true
FEATURE [Part::Cut] Cut013
  Base = -> Revolve006
  Tool = -> Extrude024
FEATURE [Sketcher::SketchObject] Sketch039
  FullyConstrained = true
  Placement = pos=(0,0,0) rot=(1,0,0;1.5708rad)
  expr: Constraints[17] = Spreadsheet003.E6
  expr: Constraints[18] = Spreadsheet003.B6 - 2 * Spreadsheet003.C6
  expr: Constraints[19] = (Spreadsheet003.B6 - 2 * Spreadsheet003.C6) / 2
  expr: Constraints[20] = Spreadsheet003.E6 / 2
  sketch-geometry (9):
    g0: LineSegment StartX=47 StartY=6.5 StartZ=0 EndX=47 EndY=-6.5 EndZ=0
    g1: LineSegment StartX=42 StartY=-11.5 StartZ=0 EndX=-42 EndY=-11.5 EndZ=0
    g2: LineSegment StartX=-47 StartY=-6.5 StartZ=0 EndX=-47 EndY=6.5 EndZ=0
    g3: LineSegment StartX=-42 StartY=11.5 StartZ=0 EndX=42 EndY=11.5 EndZ=0
    g4: GeomPoint X=0 Y=0 Z=0
    g5: ArcOfCircle CenterX=-42 CenterY=6.5 CenterZ=0 NormalX=0 NormalY=0 NormalZ=1 AngleXU=0 Radius=5 StartAngle=1.5708 EndAngle=3.14159
    g6: ArcOfCircle CenterX=-42 CenterY=-6.5 CenterZ=0 NormalX=0 NormalY=0 NormalZ=1 AngleXU=0 Radius=5 StartAngle=3.14159 EndAngle=4.71239
    g7: ArcOfCircle CenterX=42 CenterY=-6.5 CenterZ=0 NormalX=0 NormalY=0 NormalZ=1 AngleXU=0 Radius=5 StartAngle=4.71239 EndAngle=6.28319
    g8: ArcOfCircle CenterX=42 CenterY=6.5 CenterZ=0 NormalX=0 NormalY=0 NormalZ=1 AngleXU=0 Radius=5 StartAngle=0 EndAngle=1.5708
  constraints (21):
    c: Horizontal(g1)
    c: Horizontal(g3)
    c: Vertical(g0)
    c: Vertical(g2)
    c: Coincident(g4,g-1)
    c: Tangent(g3,g5) = 1.5708
    c: Tangent(g2,g5) = 1.5708
    c: Tangent(g1,g6) = 1.5708
    c: Tangent(g2,g6) = 1.5708
    c: Tangent(g1,g7) = 1.5708
    c: Tangent(g0,g7) = 1.5708
    c: Tangent(g0,g8) = 1.5708
    c: Tangent(g3,g8) = 1.5708
    c: Radius(g8) = 5
    c: Equal(g8,g7)
    c: Equal(g7,g6)
    c: Equal(g6,g5)
    c: DistanceY(g1,g3) = 23
    c: DistanceX(g2,g0) = 94
    c: Distance(g4,g2) = 47
    c: Distance(g4,g1) = 11.5
FEATURE [Part::Extrusion] Extrude025
  Base = -> Sketch039
  Dir = (0,-1,2e-16)
  DirMode = 2
  FaceMakerClass = Part::FaceMakerBullseye
  LengthFwd = 60
  LengthRev = 0
  Solid = true
  Symmetric = true
FEATURE [Part::Cut] Cut014  label="Cut005"
  Base = -> Cut013
  Tool = -> Extrude025
FEATURE [Sketcher::SketchObject] Sketch040
  FullyConstrained = true
  Placement = pos=(0,0,0) rot=(0.57735,0.57735,0.57735;2.0944rad)
  expr: Constraints[1] = Spreadsheet003.dia / 2
  sketch-geometry (1):
    g0: Circle CenterX=0 CenterY=0 CenterZ=0 NormalX=0 NormalY=0 NormalZ=1 AngleXU=0 Radius=10
  constraints (2):
    c: Coincident(g0,g-1)
    c: Radius(g0) = 10
FEATURE [Part::Extrusion] Extrude026
  Base = -> Sketch040
  Dir = (1,0,0)
  DirMode = 2
  FaceMakerClass = Part::FaceMakerBullseye
  LengthFwd = 300
  LengthRev = 0
  Solid = true
  Symmetric = true
FEATURE [Part::Cut] Cut015  label="turnBackle"
  Base = -> Cut014
  Placement = pos=(-200,0,0) rot=(0,0,1;0rad)
  Tool = -> Extrude026
  expr: .Placement.Base.x = -(Spreadsheet003.B5 + Spreadsheet003.I5 + Spreadsheet003.dia)
FEATURE [Part::Cylinder] Cylinder001  label="rod"
  Angle = 360
  AttacherType = Attacher::AttachEngine3D
  FirstAngle = 0
  Height = 1276
  Placement = pos=(-220,0,-8.8e-14) rot=(0,-1,0;1.5708rad)
  Radius = 10
  SecondAngle = 0
  expr: .Placement.Base.x = -(Spreadsheet003.B5 + Spreadsheet003.I5 + Spreadsheet003.dia * 2)
  expr: Height = Spreadsheet003.L0 - (Spreadsheet003.B5 + Spreadsheet003.I5 + Spreadsheet003.B6 - 4 * Spreadsheet003.dia - 2 * Spreadsheet003.C6) - Spreadsheet003.B7 + Spreadsheet003.I7 - Spreadsheet003.dia
  expr: Radius = Spreadsheet003.dia / 2
FEATURE [Sketcher::SketchObject] Sketch041
  FullyConstrained = true
  MapMode = 5
  Placement = pos=(90,0,0) rot=(0.57735,0.57735,0.57735;2.0944rad)
  expr: Constraints[1] = Spreadsheet003.dia
  sketch-geometry (1):
    g0: Circle CenterX=0 CenterY=0 CenterZ=0 NormalX=0 NormalY=0 NormalZ=1 AngleXU=0 Radius=10
  constraints (2):
    c: Coincident(g0,g-1)
    c: Diameter(g0) = 20
FEATURE [Part::Extrusion] Extrude027
  Base = -> Sketch041
  Dir = (1,0,0)
  DirMode = 2
  FaceMakerClass = Part::FaceMakerBullseye
  LengthFwd = 30
  LengthRev = 0
  Solid = true
  Symmetric = false
  expr: LengthFwd = Spreadsheet003.I7
FEATURE [Sketcher::SketchObject] Sketch042
  ExternalGeometry = -> [Pad001]
  FullyConstrained = true
  expr: Constraints[17] = Spreadsheet003.G7
  expr: Constraints[18] = Spreadsheet003.G7 / 2
  expr: Constraints[27] = Spreadsheet003.E7 / 2
  expr: Constraints[31] = Spreadsheet003.I7
  expr: Constraints[32] = Spreadsheet003.L7
  expr: Constraints[6] = Spreadsheet003.E7
  expr: Constraints[7] = Spreadsheet003.H7
  sketch-geometry (12):
    g0: LineSegment StartX=-23 StartY=8 StartZ=0 EndX=20 EndY=8 EndZ=0
    g1: LineSegment StartX=22 StartY=12 StartZ=0 EndX=58 EndY=12 EndZ=0
    g2: LineSegment StartX=60 StartY=10 StartZ=0 EndX=60 EndY=-10 EndZ=0
    g3: LineSegment StartX=58 StartY=-12 StartZ=0 EndX=22 EndY=-12 EndZ=0
    g4: LineSegment StartX=20 StartY=-10 StartZ=0 EndX=20 EndY=-8 EndZ=0
    g5: LineSegment StartX=20 StartY=-8 StartZ=0 EndX=-23 EndY=-8 EndZ=0
    g6: LineSegment StartX=-23 StartY=-8 StartZ=0 EndX=-23 EndY=8 EndZ=0
    g7: ArcOfCircle CenterX=22 CenterY=10 CenterZ=0 NormalX=0 NormalY=0 NormalZ=1 AngleXU=0 Radius=2 StartAngle=1.5708 EndAngle=3.14159
    g8: ArcOfCircle CenterX=22 CenterY=-10 CenterZ=0 NormalX=0 NormalY=0 NormalZ=1 AngleXU=0 Radius=2 StartAngle=3.14159 EndAngle=4.71239
    g9: ArcOfCircle CenterX=58 CenterY=-10 CenterZ=0 NormalX=0 NormalY=0 NormalZ=1 AngleXU=0 Radius=2 StartAngle=4.71239 EndAngle=6.28319
    g10: ArcOfCircle CenterX=58 CenterY=10 CenterZ=0 NormalX=0 NormalY=0 NormalZ=1 AngleXU=0 Radius=2 StartAngle=5e-16 EndAngle=1.5708
    g11: LineSegment StartX=20 StartY=8 StartZ=0 EndX=20 EndY=10 EndZ=0
  constraints (33):
    c: Horizontal(g0)
    c: Coincident(g4,g5)
    c: Horizontal(g5)
    c: Coincident(g5,g6)
    c: Coincident(g6,g0)
    c: Vertical(g6)
    c: DistanceY(g6,g6) = 16
    c: DistanceX(g-1,g0) = 20
    c: Horizontal(g1)
    c: Horizontal(g3)
    c: Coincident(g11,g0)
    c: Vertical(g11)
    c: Vertical(g2)
    c: Tangent(g9,g2) = 1.5708
    c: Tangent(g1,g10) = 1.5708
    c: Tangent(g10,g2) = 1.5708
    c: Tangent(g1,g7) = 1.5708
    c: DistanceY(g3,g1) = 24
    c: DistanceY(g-1,g1) = 12
    c: Radius(g10) = 2
    c: Equal(g10,g9)
    c: Equal(g9,g7)
    c: Radius(g8) = 2
    c: Vertical(g4)
    c: Vertical(g4,g0)
    c: Tangent(g8,g4) = 1.5708
    c: Vertical(g8,g8)
    c: DistanceY(g-1,g0) = 8
    c: Tangent(g9,g3) = 1.5708
    c: Tangent(g7,g11) = 1.5708
    c: Coincident(g8,g3)
    c: DistanceX(g2,g-3) = 30
    c: DistanceX(g0,g-1) = 23
FEATURE [Part::Extrusion] Extrude028
  Base = -> Sketch042
  Dir = (0,0,1)
  DirMode = 2
  FaceMakerClass = Part::FaceMakerBullseye
  LengthFwd = 150
  LengthRev = 0
  Solid = true
  Symmetric = true
FEATURE [Part::Cut] Cut016
  Base = -> Pad001
  Tool = -> Extrude028
FEATURE [Part::Cut] Cut017
  Base = -> Cut016
  Tool = -> Extrude027
FEATURE [Part::Cut] Cut018  label="forkEndL"
  Base = -> Cut017
  Placement = pos=(-1550,0,0) rot=(0,0,1;0rad)
  Tool = -> Extrude021
  expr: .Placement.Base.x = -Spreadsheet003.L0
FEATURE [App::Part] Part009  label="TurnBackle"
  Group = -> [Spreadsheet003,Sketch035,Cylinder,Cut012,Sketch036,Extrude022,Extrude023,Fusion001,Revolve006,Sketch038,Cut014,Cut013,Extrude024,Extrude025,Extrude026,Sketch039,Sketch037,Sketch040,Cut015,Cylinder001,Extrude021,Sketch034,Extrude027,Extrude028,Cut016,Cut017,Sketch041,Pad001,Sketch033,Sketch042,Cut018]
  Origin = -> Origin013
FEATURE [Part::Compound] Compound016  label="turnBackle001"
  Links = -> [Part009]
  Placement = pos=(2500.34,492,2207.53) rot=(0,1,0;0.195949rad)
FEATURE [App::FeaturePython] axisCoincident_003  label="axisCoincident_003__rake002"  # a2plus constraint (typed FeaturePython)
  Object1 = Compound016
  Object2 = Compound015
  ParentTreeObject = -> Compound016
  SubElement1 = Edge44
  SubElement2 = Edge3689
  Suppressed = false
  Type = axial
  directionConstraint = 0
  lockRotation = false
FEATURE [App::FeaturePython] axisCoincident_003_mirror  label="axisCoincident_003__turnBackle001"  # a2plus constraint (typed FeaturePython)
  Object1 = Compound016
  Object2 = Compound015
  ParentTreeObject = -> Compound015
  SubElement1 = Edge44
  SubElement2 = Edge3689
  Suppressed = false
  Type = axial
  directionConstraint = 0
  lockRotation = false
FEATURE [Part::Mirroring] Mirror012  label="turnBackle001 (mirrored)"
  Base = (1300,0,0)
  Normal = (0,-1,0)
  Source = -> Compound016
FEATURE [App::Part] Part006  label="RakeArm"
  Group = -> [Spreadsheet002,Part008,axisCoincident_003_mirror,Compound015,Part009,axisCoincident_003,Compound016,Mirror012]
  Origin = -> Origin009
FEATURE [Part::FeaturePython] Array019  # Draft array (typed FeaturePython)
  AlwaysSyncPlacement = false
  Angle = 360
  ArrayType = 1
  Axis = (0,0,1)
  Base = -> Part006
  Center = (0,0,5504.95)
  Count = 2
  ExpandArray = false
  Fuse = false
  IntervalAxis = (0,0,0)
  IntervalX = (50,0,0)
  IntervalY = (0,50,0)
  IntervalZ = (0,0,50)
  NumberCircles = 3
  NumberPolar = 2
  NumberX = 2
  NumberY = 2
  NumberZ = 1
  PlacementList = 2 placements: [(0,0,0),(0,0,0)]
  RadialDistance = 50
  ScaleList = (2) [(1,1,1),(1,1,1)]
  Symmetry = 1
  TangentialDistance = 25
FEATURE [Sketcher::SketchObject] Sketch043
  FullyConstrained = false
  Placement = pos=(0,0,0) rot=(1,0,0;1.5708rad)
  sketch-geometry (4):
    g0: LineSegment StartX=807.255 StartY=946.383 StartZ=0 EndX=1588.96 EndY=946.383 EndZ=0
    g1: LineSegment StartX=1588.96 StartY=946.383 StartZ=0 EndX=1417.36 EndY=239.952 EndZ=0
    g2: LineSegment StartX=1417.36 StartY=239.952 StartZ=0 EndX=987.78 EndY=239.952 EndZ=0
    g3: LineSegment StartX=987.78 StartY=239.952 StartZ=0 EndX=807.255 EndY=946.383 EndZ=0
  constraints (6):
    c: Horizontal(g0)
    c: Coincident(g0,g1)
    c: Coincident(g1,g2)
    c: Horizontal(g2)
    c: Coincident(g2,g3)
    c: Coincident(g3,g0)
FEATURE [Part::FeaturePython] AngleSteel010  label="AngleSteel014"  # WARN: FeaturePython — macro-defined, semantics opaque (R4)
  A = 75
  B = 75
  L = 1000
  Placement = pos=(1151.57,-0.033,238.583) rot=(0,0,1;1.5708rad)
  Solid = false
  g0 = 7.85
  mass = 0
  size = 10
  standard = SS_Equal
  t = 6
FEATURE [Part::Sweep] Sweep001
  Frenet = false
  Sections = -> [AngleSteel010]
  Solid = true
  Spine = -> Sketch043 [Edge3,Edge2,Edge1,Edge4]
  Transition = 1
FEATURE [Part::FeaturePython] AngleSteel011  label="AngleSteel015"  # WARN: FeaturePython — macro-defined, semantics opaque (R4)
  A = 75
  B = 75
  L = 380
  Placement = pos=(915.214,37.533,946.675) rot=(0,0,1;1.5708rad)
  Solid = true
  g0 = 7.85
  mass = 2.60308
  size = 10
  standard = SS_Equal
  t = 6
FEATURE [Part::Compound] Compound017
  Links = -> [Sweep001,AngleSteel011]
FEATURE [Part::FeaturePython] Array020  # Draft array (typed FeaturePython)
  AlwaysSyncPlacement = false
  Angle = 360
  ArrayType = 1
  Axis = (0,0,1)
  Base = -> Compound017
  Center = (0,0,5350)
  Count = 2
  ExpandArray = false
  Fuse = false
  IntervalAxis = (0,0,0)
  IntervalX = (50,0,0)
  IntervalY = (0,50,0)
  IntervalZ = (0,0,50)
  NumberCircles = 3
  NumberPolar = 2
  NumberX = 2
  NumberY = 2
  NumberZ = 1
  PlacementList = 2 placements: [(0,0,0),(0,0,0)]
  RadialDistance = 50
  ScaleList = (2) [(1,1,1),(1,1,1)]
  Symmetry = 1
  TangentialDistance = 25
FEATURE [App::Part] Part004  label="centerCage002"
  Group = -> [Part002,Compound010,Part__Feature007,Sweep001,Sketch043,AngleSteel011,AngleSteel010,Compound017,Array020]
  Origin = -> Origin008
  Placement = pos=(0,0,-200) rot=(0,0,1;0rad)
FEATURE [Part::FeaturePython] Flange_Reducer  # WARN: FeaturePython — macro-defined, semantics opaque (R4)
  Fittings = 04_Flange Reducer
  Placement = pos=(2.02e-13,0,908.896) rot=(0,1,0;1.5708rad)
  dia = 28
  mass = 158
FEATURE [Part::FeaturePython] F90Elbow  # WARN: FeaturePython — macro-defined, semantics opaque (R4)
  Fittings = 05_F90Elbow
  Placement = pos=(1.01e-13,0,-451.65) rot=(0.57735,-0.57735,0.57735;2.0944rad)
  dia = 7
  mass = 181
FEATURE [Part::FeaturePython] K_Short_tube_No_1th  # WARN: FeaturePython — macro-defined, semantics opaque (R4)
  Fittings = 16_K_Short tube No.1th
  Placement = pos=(940.02,0,-451.32) rot=(0,1,0;3.14159rad)
  dia = 7
  mass = 77.6
FEATURE [Part::FeaturePython] K_5Elbow  # WARN: FeaturePython — macro-defined, semantics opaque (R4)
  Fittings = 09_K_5_5/8Bent tube
  Placement = pos=(1521.01,2.86e-13,-446.797) rot=(-0.537067,0.596473,-0.596473;4.12735rad)
  dia = 2
  mass = 25
FEATURE [Part::FeaturePython] K_Straight_tube  # WARN: FeaturePython — macro-defined, semantics opaque (R4)
  Fittings = 00_K_Straight tube
  L = 6000
  Placement = pos=(8130.76,-0.0126395,301.515) rot=(0,1,0;3.02815rad)
  dia = 7
  mass = 512.34
FEATURE [Part::FeaturePython] Single_Flange_Length_Tube  # WARN: FeaturePython — macro-defined, semantics opaque (R4)
  Fittings = 01_Single Flange Length Tube
  L0 = 1000
  Placement = pos=(9014.01,-0.0126395,410.932) rot=(0,1,0;3.01942rad)
  dia = 7
  mass = 571.9
FEATURE [Sketcher::SketchObject] Sketch044
  FullyConstrained = false
  Placement = pos=(0,0,0) rot=(1,0,0;1.5708rad)
  sketch-geometry (2):
    g0: LineSegment StartX=1418.66 StartY=222.425 StartZ=0 EndX=7911.9 EndY=1066.48 EndZ=0
    g1: LineSegment StartX=7911.9 StartY=1066.48 StartZ=0 EndX=8784.27 EndY=1066.48 EndZ=0
  constraints (2):
    c: Coincident(g0,g1)
    c: Horizontal(g1)
FEATURE [Sketcher::SketchObject] Sketch046
  FullyConstrained = false
  Placement = pos=(0,0,0) rot=(1,0,0;1.5708rad)
  sketch-geometry (4):
    g0: LineSegment StartX=1200.83 StartY=498.314 StartZ=0 EndX=1571.13 EndY=498.314 EndZ=0
    g1: LineSegment StartX=1571.13 StartY=498.314 StartZ=0 EndX=1463.62 EndY=59.3294 EndZ=0
    g2: LineSegment StartX=1463.62 StartY=59.3294 StartZ=0 EndX=1200.83 EndY=59.3294 EndZ=0
    g3: LineSegment StartX=1200.83 StartY=59.3294 StartZ=0 EndX=1200.83 EndY=498.314 EndZ=0
  constraints (7):
    c: Horizontal(g0)
    c: Coincident(g0,g1)
    c: Coincident(g1,g2)
    c: Horizontal(g2)
    c: Coincident(g2,g3)
    c: Coincident(g3,g0)
    c: Vertical(g3)
FEATURE [Part::Revolution] Revolve007
  Angle = 360
  Axis = (0,0,1)
  Base = (0,0,0)
  FaceMakerClass = Part::FaceMakerBullseye
  Solid = true
  Source = -> Sketch046
  Symmetric = false
FEATURE [Sketcher::SketchObject] Sketch047
  FullyConstrained = true
  Placement = pos=(0,0,0) rot=(1,0,0;1.5708rad)
  expr: Constraints[11] = Spreadsheet004.dia / 2 - 460
  sketch-geometry (4):
    g0: LineSegment StartX=7285 StartY=0 StartZ=0 EndX=7290 EndY=0 EndZ=0
    g1: LineSegment StartX=7290 StartY=0 StartZ=0 EndX=7290 EndY=250 EndZ=0
    g2: LineSegment StartX=7290 StartY=250 StartZ=0 EndX=7285 EndY=250 EndZ=0
    g3: LineSegment StartX=7285 StartY=250 StartZ=0 EndX=7285 EndY=0 EndZ=0
  constraints (12):
    c: Coincident(g0,g1)
    c: Coincident(g1,g2)
    c: Coincident(g2,g3)
    c: Coincident(g3,g0)
    c: Horizontal(g0)
    c: Horizontal(g2)
    c: Vertical(g1)
    c: Vertical(g3)
    c: PointOnObject(g0,g-1)
    c: Distance(g2) = 5
    c: DistanceY(g1,g1) = 250
    c: DistanceX(g-1,g0) = 7290
FEATURE [Part::Revolution] Revolve008
  Angle = 360
  Axis = (0,0,1)
  Base = (0,0,0)
  FaceMakerClass = Part::FaceMakerBullseye
  Solid = true
  Source = -> Sketch047
  Symmetric = false
FEATURE [Sketcher::SketchObject] Sketch048
  ExternalGeometry = -> [Revolve008]
  FullyConstrained = true
  Placement = pos=(0,0,0) rot=(1,0,0;1.5708rad)
  sketch-geometry (3):
    g0: LineSegment StartX=-70 StartY=250 StartZ=0 EndX=70 EndY=250 EndZ=0
    g1: LineSegment StartX=70 StartY=250 StartZ=0 EndX=0 EndY=180 EndZ=0
    g2: LineSegment StartX=0 StartY=180 StartZ=0 EndX=-70 EndY=250 EndZ=0
  constraints (9):
    c: Horizontal(g0)
    c: Coincident(g0,g1)
    c: PointOnObject(g1,g-2)
    c: Coincident(g1,g2)
    c: Coincident(g2,g0)
    c: Angle(g1,g2) = 1.5708
    c: PointOnObject(g0,g-3)
    c: DistanceY(g1,g0) = 70
    c: Angle(g2,g-2) = 2.35619
FEATURE [Part::Extrusion] Extrude029
  Base = -> Sketch048
  Dir = (0,-1,-3e-16)
  DirMode = 2
  FaceMakerClass = Part::FaceMakerBullseye
  LengthFwd = 10000
  LengthRev = 0
  Solid = true
  Symmetric = false
FEATURE [Part::FeaturePython] Array021  # Draft array (typed FeaturePython)
  AlwaysSyncPlacement = false
  Angle = 360
  ArrayType = 1
  Axis = (0,0,1)
  Base = -> Extrude029
  Center = (0,0,0)
  Count = 280
  ExpandArray = false
  Fuse = false
  IntervalAxis = (0,0,0)
  IntervalX = (50,0,0)
  IntervalY = (0,50,0)
  IntervalZ = (0,0,50)
  NumberCircles = 3
  NumberPolar = 280
  NumberX = 2
  NumberY = 2
  NumberZ = 1
  PlacementList = 280 placements: [(0,0,0),(0,0,0),(0,0,0),(0,0,0),(0,0,0),(0,0,0),(0,0,0),(0,0,0),(0,0,0),(0,0,0),(0,0,0),(0,0,0),(0,0,0),(0,0,0),(0,0,0),(0,0,0),(0,0,0),(0,0,0),(0,0,0),(0,0,0),(0,0,0),(0,0,0),(0,0,0),(0,0,0),(0,0,0),(0,0,0),(0,0,0),(0,0,0),(0,0,0),(0,0,0),(0,0,0),(0,0,0),(0,0,0),(0,0,0),(0,0,0),(0,0,0),(0,0,0),(0,0,0),(0,0,0),(0,0,0),(0,0,0),(0,0,0),(0,0,0),(0,0,0),(0,0,0),(0,0,0),(0,0,0),(0,0,0),(0,0,0),(0,0,0),+230 more]
  RadialDistance = 50
  Symmetry = 1
  TangentialDistance = 25
FEATURE [Part::Cut] Cut020  label="weir"
  Base = -> Revolve008
  Tool = -> Array021
FEATURE [Sketcher::SketchObject] Sketch049
  ExternalGeometry = -> [Cut020]
  FullyConstrained = true
  Placement = pos=(0,0,0) rot=(1,0,0;1.5708rad)
  sketch-geometry (4):
    g0: LineSegment StartX=6985 StartY=40 StartZ=0 EndX=6990 EndY=40 EndZ=0
    g1: LineSegment StartX=6990 StartY=40 StartZ=0 EndX=6990 EndY=380 EndZ=0
    g2: LineSegment StartX=6990 StartY=380 StartZ=0 EndX=6985 EndY=380 EndZ=0
    g3: LineSegment StartX=6985 StartY=380 StartZ=0 EndX=6985 EndY=40 EndZ=0
  constraints (12):
    c: Coincident(g0,g1)
    c: Coincident(g1,g2)
    c: Coincident(g2,g3)
    c: Coincident(g3,g0)
    c: Horizontal(g0)
    c: Horizontal(g2)
    c: Vertical(g1)
    c: Vertical(g3)
    c: DistanceX(g2,g2) = 5
    c: DistanceY(g1,g1) = 340
    c: DistanceY(g-3,g1) = 130
    c: DistanceX(g0,g-4) = 300
FEATURE [Part::Revolution] Revolve009  label="Revolve001"
  Angle = 360
  Axis = (0,0,1)
  Base = (0,0,0)
  FaceMakerClass = Part::FaceMakerBullseye
  Solid = true
  Source = -> Sketch049
  Symmetric = false
FEATURE [Part::FeaturePython] AngleSteel012  label="AngleSteel016"  # WARN: FeaturePython — macro-defined, semantics opaque (R4)
  A = 50
  B = 50
  L = 1000
  Placement = pos=(7000,0,474) rot=(0,1,0;1.5708rad)
  Solid = false
  g0 = 7.85
  mass = 0
  size = 7
  standard = SS_Equal
  t = 6
  expr: .Placement.Base.x = Spreadsheet004.dia / 2 - 750
FEATURE [Part::Revolution] Revolve010  label="Revolve002"
  Angle = 360
  Axis = (0,0,1)
  Base = (0,0,0)
  FaceMakerClass = Part::FaceMakerBullseye
  Placement = pos=(0,0,-94) rot=(0,0,1;0rad)
  Solid = false
  Source = -> AngleSteel012
  Symmetric = false
FEATURE [Sketcher::SketchObject] Sketch050
  ExternalGeometry = -> [Revolve009,Cut020]
  FullyConstrained = true
  Placement = pos=(0,0,0) rot=(1,0,0;1.5708rad)
  sketch-geometry (4):
    g0: LineSegment StartX=6990 StartY=40 StartZ=0 EndX=7290 EndY=-152.602 EndZ=0
    g1: LineSegment StartX=7290 StartY=-152.602 StartZ=0 EndX=7290 EndY=-10 EndZ=0
    g2: LineSegment StartX=7290 StartY=-10 StartZ=0 EndX=6990 EndY=182.602 EndZ=0
    g3: LineSegment StartX=6990 StartY=182.602 StartZ=0 EndX=6990 EndY=40 EndZ=0
  constraints (11):
    c: Coincident(g0,g1)
    c: Vertical(g1)
    c: Coincident(g1,g2)
    c: Coincident(g2,g3)
    c: Coincident(g3,g0)
    c: Vertical(g3)
    c: Vertical(g1,g-4)
    c: Distance(g1,g0) = 120
    c: Coincident(g0,g-3)
    c: Parallel(g2,g0)
    c: DistanceY(g1,g-4) = 10
FEATURE [Part::Extrusion] Extrude030
  Base = -> Sketch050
  Dir = (0,-1,2e-16)
  DirMode = 2
  FaceMakerClass = Part::FaceMakerBullseye
  LengthFwd = 6
  LengthRev = 0
  Solid = true
  Symmetric = true
FEATURE [Spreadsheet::Sheet] Spreadsheet004
  cells = A3='tankDia dia; B3(dia)=15500; A4='n; B4(n)=12; A5='buffleHight  h0; B5(h0)=230
FEATURE [Part::FeaturePython] AngleSteel013  label="AngleSteel001"  # WARN: FeaturePython — macro-defined, semantics opaque (R4)
  A = 50
  B = 50
  L = 140
  Placement = pos=(7265.03,28,-150) rot=(0,0,1;3.14159rad)
  Solid = true
  g0 = 7.85
  mass = 0.620249
  size = 7
  standard = SS_Equal
  t = 6
FEATURE [Part::Mirroring] Mirror013  label="AngleSteel001 (mirrored)"
  Base = (4800,0,0)
  Normal = (0,-1,0)
  Source = -> AngleSteel013
FEATURE [Part::Compound] Compound018
  Links = -> [AngleSteel013,Mirror013,Extrude030]
FEATURE [Part::FeaturePython] Array022  # Draft array (typed FeaturePython)
  AlwaysSyncPlacement = false
  Angle = 360
  ArrayType = 1
  Axis = (0,0,1)
  Base = -> Compound018
  Center = (0,0,0)
  Count = 12
  ExpandArray = false
  Fuse = false
  IntervalAxis = (0,0,0)
  IntervalX = (50,0,0)
  IntervalY = (0,50,0)
  IntervalZ = (0,0,50)
  NumberCircles = 3
  NumberPolar = 12
  NumberX = 2
  NumberY = 2
  NumberZ = 1
  PlacementList = 12 placements: [(0,0,0),(0,0,0),(0,0,0),(0,0,0),(0,0,0),(0,0,0),(0,0,0),(0,0,0),(0,0,0),(0,0,0),(0,0,0),(0,0,0)]
  RadialDistance = 50
  ScaleList = (12) [(1,1,1),(1,1,1),(1,1,1),(1,1,1),(1,1,1),(1,1,1),(1,1,1),(1,1,1),(1,1,1),(1,1,1),(1,1,1),(1,1,1)]
  Symmetry = 1
  TangentialDistance = 25
  expr: NumberPolar = Spreadsheet004.n
FEATURE [Part::Compound] Compound025
  Links = -> [Revolve009,Cut020,Revolve010,Array022]
FEATURE [App::Part] Part013  label="buffle"
  Group = -> [Spreadsheet004,Revolve008,Revolve009,Array021,Sketch049,Sketch047,Sketch050,Sketch048,Cut020,Extrude030,Extrude029,AngleSteel012,Revolve010,AngleSteel013,Mirror013,Compound018,Array022,Compound025]
  Origin = -> Origin017
  Placement = pos=(0,0,4700) rot=(0,0,1;0.261799rad)
FEATURE [Part::FeaturePython] Flange  # WARN: FeaturePython — macro-defined, semantics opaque (R4)
  Placement = pos=(8795.27,0.11354,1066.4) rot=(0,-1,0;1.5708rad)
  dia = 4
  fittings = 00_Flange
  material = 0
  standard = 1
FEATURE [Sketcher::SketchObject] Sketch051
  FullyConstrained = true
  Placement = pos=(0,0,0) rot=(1,0,0;1.5708rad)
  expr: Constraints[11] = Spreadsheet005.dia / 2
  expr: Constraints[9] = Spreadsheet005.h0
  sketch-geometry (4):
    g0: LineSegment StartX=1545 StartY=0 StartZ=0 EndX=1550 EndY=0 EndZ=0
    g1: LineSegment StartX=1550 StartY=0 StartZ=0 EndX=1550 EndY=2100 EndZ=0
    g2: LineSegment StartX=1550 StartY=2100 StartZ=0 EndX=1545 EndY=2100 EndZ=0
    g3: LineSegment StartX=1545 StartY=2100 StartZ=0 EndX=1545 EndY=0 EndZ=0
  constraints (12):
    c: Coincident(g0,g1)
    c: Coincident(g1,g2)
    c: Coincident(g2,g3)
    c: Coincident(g3,g0)
    c: Horizontal(g0)
    c: Horizontal(g2)
    c: Vertical(g1)
    c: Vertical(g3)
    c: DistanceX(g2,g2) = 5
    c: DistanceY(g1,g1) = 2100
    c: PointOnObject(g0,g-1)
    c: DistanceX(g-1,g0) = 1550
FEATURE [Part::Revolution] Revolve011
  Angle = 360
  Axis = (0,0,1)
  Base = (0,0,0)
  FaceMakerClass = Part::FaceMakerBullseye
  Solid = true
  Source = -> Sketch051
  Symmetric = false
FEATURE [Part::FeaturePython] AngleSteel014  label="AngleSteel017"  # WARN: FeaturePython — macro-defined, semantics opaque (R4)
  A = 75
  B = 75
  L = 1000
  Placement = pos=(1550,0,0) rot=(0,0,1;0rad)
  Solid = false
  g0 = 7.85
  mass = 0
  size = 10
  standard = SS_Equal
  t = 6
  expr: .Placement.Base.x = Spreadsheet005.dia / 2
FEATURE [Part::Revolution] Revolve012
  Angle = 360
  Axis = (0,0,1)
  Base = (0,0,0)
  FaceMakerClass = Part::FaceMakerBullseye
  Solid = false
  Source = -> AngleSteel014
  Symmetric = false
FEATURE [Part::FeaturePython] AngleSteel015  label="AngleSteel018"  # WARN: FeaturePython — macro-defined, semantics opaque (R4)
  A = 75
  B = 75
  L = 1000
  Placement = pos=(1550,0,2100) rot=(0,1,0;1.5708rad)
  Solid = false
  g0 = 7.85
  mass = 0
  size = 10
  standard = SS_Equal
  t = 6
  expr: .Placement.Base.x = Spreadsheet005.dia / 2
  expr: .Placement.Base.z = Spreadsheet005.h0
FEATURE [Part::Revolution] Revolve013
  Angle = 360
  Axis = (0,0,1)
  Base = (0,0,0)
  FaceMakerClass = Part::FaceMakerBullseye
  Solid = false
  Source = -> AngleSteel015
  Symmetric = false
FEATURE [Sketcher::SketchObject] Sketch052
  ExternalGeometry = -> [Revolve013]
  FullyConstrained = true
  Placement = pos=(0,0,0) rot=(1,0,0;1.5708rad)
  sketch-geometry (4):
    g0: LineSegment StartX=-275 StartY=1580 StartZ=0 EndX=275 EndY=1580 EndZ=0
    g1: LineSegment StartX=275 StartY=1580 StartZ=0 EndX=275 EndY=2100 EndZ=0
    g2: LineSegment StartX=275 StartY=2100 StartZ=0 EndX=-275 EndY=2100 EndZ=0
    g3: LineSegment StartX=-275 StartY=2100 StartZ=0 EndX=-275 EndY=1580 EndZ=0
  constraints (12):
    c: Coincident(g0,g1)
    c: Coincident(g1,g2)
    c: Coincident(g2,g3)
    c: Coincident(g3,g0)
    c: Horizontal(g0)
    c: Horizontal(g2)
    c: Vertical(g1)
    c: Vertical(g3)
    c: DistanceX(g0,g0) = 550
    c: DistanceY(g1,g1) = 520
    c: PointOnObject(g1,g-3)
    c: DistanceX(g-1,g0) = 275
FEATURE [Part::Extrusion] Extrude031
  Base = -> Sketch052
  Dir = (0,-1,2e-16)
  DirMode = 2
  FaceMakerClass = Part::FaceMakerBullseye
  LengthFwd = 1700
  LengthRev = 0
  Solid = true
  Symmetric = false
FEATURE [Part::MultiFuse] Fusion002  label="Fusion"
  Shapes = -> [Revolve011,Revolve012,Revolve013]
FEATURE [Part::Cut] Cut021
  Base = -> Fusion002
  Tool = -> Extrude031
FEATURE [Sketcher::SketchObject] Sketch053
  ExternalGeometry = -> [Cut021]
  FullyConstrained = false
  MapMode = 5
  Placement = pos=(0,3.476e-13,1580) rot=(0,0,1;0rad)
  Support = -> [Cut021]
  sketch-geometry (4):
    g0: LineSegment StartX=-275 StartY=-1515.41 StartZ=0 EndX=-275 EndY=-1545.41 EndZ=0
    g1: LineSegment StartX=-275 StartY=-1515.41 StartZ=0 EndX=275 EndY=-1515.41 EndZ=0
    g2: LineSegment StartX=275 StartY=-1515.41 StartZ=0 EndX=275 EndY=-1545.41 EndZ=0
    g3: ArcOfCircle CenterX=3.103e-13 CenterY=-44.7314 CenterZ=0 NormalX=0 NormalY=0 NormalZ=1 AngleXU=0 Radius=1525.67 StartAngle=4.53115 EndAngle=4.89363
  constraints (12):
    c: Vertical(g0)
    c: Coincident(g0,g1)
    c: Horizontal(g1)
    c: Coincident(g1,g2)
    c: Vertical(g2)
    c: Coincident(g3,g0)
    c: Coincident(g3,g2)
    c: PointOnObject(g-3,g0)
    c: PointOnObject(g-4,g2)
    c: DistanceY(g-3,g0) = 10
    c: DistanceY(g0,g0) = 30
    c: Equal(g0,g2)
FEATURE [Part::Extrusion] Extrude032
  Base = -> Sketch053
  Dir = (0,2e-16,1)
  DirMode = 2
  FaceMakerClass = Part::FaceMakerBullseye
  LengthFwd = 5
  LengthRev = 0
  Solid = true
  Symmetric = false
FEATURE [Sketcher::SketchObject] Sketch054
  ExternalGeometry = -> [Extrude032]
  FullyConstrained = true
  MapMode = 5
  Placement = pos=(0,7.3227e-12,1585) rot=(0,0,1;0rad)
  Support = -> [Extrude032]
  sketch-geometry (4):
    g0: LineSegment StartX=-275 StartY=-1530.41 StartZ=0 EndX=275 EndY=-1530.41 EndZ=0
    g1: LineSegment StartX=275 StartY=-1530.41 StartZ=0 EndX=275 EndY=-1520.41 EndZ=0
    g2: LineSegment StartX=275 StartY=-1520.41 StartZ=0 EndX=-275 EndY=-1520.41 EndZ=0
    g3: LineSegment StartX=-275 StartY=-1520.41 StartZ=0 EndX=-275 EndY=-1530.41 EndZ=0
  constraints (12):
    c: Coincident(g0,g1)
    c: Coincident(g1,g2)
    c: Coincident(g2,g3)
    c: Coincident(g3,g0)
    c: Horizontal(g0)
    c: Horizontal(g2)
    c: Vertical(g1)
    c: Vertical(g3)
    c: DistanceY(g1,g-3) = 5
    c: DistanceY(g1,g1) = 10
    c: PointOnObject(g1,g-4)
    c: PointOnObject(g2,g-5)
FEATURE [Part::Extrusion] Extrude033
  Base = -> Sketch054
  Dir = (0,4.6e-15,1)
  DirMode = 2
  FaceMakerClass = Part::FaceMakerBullseye
  LengthFwd = 515
  LengthRev = 0
  Solid = true
  Symmetric = false
FEATURE [Sketcher::SketchObject] Sketch055
  ExternalGeometry = -> [Extrude033]
  FullyConstrained = true
  MapMode = 5
  Placement = pos=(0,-1530.41,7.0705e-12) rot=(1,0,0;1.5708rad)
  Support = -> [Extrude033]
  sketch-geometry (4):
    g0: LineSegment StartX=-170 StartY=2100 StartZ=0 EndX=-170 EndY=1860 EndZ=0
    g1: ArcOfCircle CenterX=0 CenterY=1860 CenterZ=0 NormalX=0 NormalY=0 NormalZ=1 AngleXU=0 Radius=170 StartAngle=3.14159 EndAngle=6.28319
    g2: LineSegment StartX=170 StartY=1860 StartZ=0 EndX=170 EndY=2100 EndZ=0
    g3: LineSegment StartX=170 StartY=2100 StartZ=0 EndX=-170 EndY=2100 EndZ=0
  constraints (12):
    c: Vertical(g0)
    c: Tangent(g0,g1) = -1.5708
    c: Coincident(g1,g2)
    c: Vertical(g2)
    c: Coincident(g2,g3)
    c: Coincident(g3,g0)
    c: Horizontal(g3)
    c: Radius(g1) = 170
    c: DistanceX(g-2,g1) = 170
    c: PointOnObject(g2,g-3)
    c: Distance(g1,g3) = 240
    c: PointOnObject(g1,g-2)
FEATURE [Part::Extrusion] Extrude034
  Base = -> Sketch055
  Dir = (0,-1,4.5e-15)
  DirMode = 2
  FaceMakerClass = Part::FaceMakerBullseye
  LengthFwd = 10
  LengthRev = 0
  Reversed = true
  Solid = true
  Symmetric = false
FEATURE [Part::Cut] Cut022
  Base = -> Extrude033
  Tool = -> Extrude034
FEATURE [Sketcher::SketchObject] Sketch056
  ExternalGeometry = -> [Cut022,Cut021]
  FullyConstrained = false
  MapMode = 5
  Placement = pos=(0,-1530.41,7.0705e-12) rot=(1,0,0;1.5708rad)
  Support = -> [Cut022]
  sketch-geometry (11):
    g0: Circle CenterX=-200 CenterY=1910 CenterZ=0 NormalX=0 NormalY=0 NormalZ=1 AngleXU=0 Radius=6
    g1: Circle CenterX=-200 CenterY=2050 CenterZ=0 NormalX=0 NormalY=0 NormalZ=1 AngleXU=0 Radius=6
    g2: Circle CenterX=200 CenterY=2050.06 CenterZ=0 NormalX=0 NormalY=0 NormalZ=1 AngleXU=0 Radius=6
    g3: Circle CenterX=200 CenterY=1910.17 CenterZ=0 NormalX=0 NormalY=0 NormalZ=1 AngleXU=0 Radius=6
    g4: LineSegment StartX=-200 StartY=2050 StartZ=0 EndX=200 EndY=2050.06 EndZ=0
    g5: Circle CenterX=-200 CenterY=1810 CenterZ=0 NormalX=0 NormalY=0 NormalZ=1 AngleXU=0 Radius=6
    g6: Circle CenterX=-200 CenterY=1640 CenterZ=0 NormalX=0 NormalY=0 NormalZ=1 AngleXU=0 Radius=6
    g7: Circle CenterX=200 CenterY=1809.81 CenterZ=0 NormalX=0 NormalY=0 NormalZ=1 AngleXU=0 Radius=6
    g8: Circle CenterX=200 CenterY=1639.81 CenterZ=0 NormalX=0 NormalY=0 NormalZ=1 AngleXU=0 Radius=6
    g9: LineSegment StartX=-200 StartY=1810 StartZ=0 EndX=200 EndY=1809.81 EndZ=0
    g10: Circle CenterX=0 CenterY=1640 CenterZ=0 NormalX=0 NormalY=0 NormalZ=1 AngleXU=0 Radius=6
  constraints (30):
    c: Radius(g0) = 6
    c: DistanceY(g-3,g0) = 50
    c: DistanceX(g0,g-3) = 200
    c: Radius(g1) = 6
    c: Vertical(g0,g1)
    c: Distance(g1,g-4) = 50
    c: Equal(g0,g3) = 6
    c: Equal(g1,g2) = 6
    c: Vertical(g3,g2)
    c: Coincident(g1,g4)
    c: Coincident(g2,g4)
    c: Distance(g4) = 400
    c: Angle(g4) = 0.000157168
    c: Radius(g5) = 6
    c: Equal(g5,g6) = 6
    c: DistanceY(g6,g5) = 170
    c: Vertical(g6,g5)
    c: Equal(g5,g7) = 6
    c: Equal(g7,g8) = 6
    c: DistanceY(g8,g7) = 170
    c: Vertical(g8,g7)
    c: Coincident(g5,g9)
    c: Coincident(g7,g9)
    c: Distance(g9) = 400
    c: Angle(g9) = -0.000466913
    c: DistanceX(g5,g-3) = 200
    c: PointOnObject(g10,g-2)
    c: Radius(g10) = 6
    c: Horizontal(g10,g6)
    c: DistanceY(g5,g-3) = 50
FEATURE [Part::Extrusion] Extrude035
  Base = -> Sketch056
  Dir = (0,-1,4.5e-15)
  DirMode = 2
  FaceMakerClass = Part::FaceMakerBullseye
  LengthFwd = 10
  LengthRev = 0
  Reversed = true
  Solid = true
  Symmetric = false
FEATURE [Part::Cut] Cut023
  Base = -> Cut022
  Tool = -> Extrude035
FEATURE [Spreadsheet::Sheet] Spreadsheet005  label="Spreadsheet_feedWell"
  cells = A2='tankDia   D0; B2(D0)=15500; A3='depth of water  hw; B3(hw)=3500; A4='feedWell dia  dia; B4(dia)==D0 * 0.2; A5='feedWell hight  h0; B5(h0)==hw * 0.6; A6='bracket hight h1; B6(h1)=1200
FEATURE [Sketcher::SketchObject] Sketch057
  FullyConstrained = false
  Placement = pos=(0,0,0) rot=(1,0,0;1.5708rad)
  sketch-geometry (23):
    g0: LineSegment StartX=-235 StartY=2.04e-14 StartZ=0 EndX=-166.5 EndY=2.04e-14 EndZ=0
    g1: LineSegment StartX=235 StartY=0 StartZ=0 EndX=235 EndY=240 EndZ=0
    g2: LineSegment StartX=235 StartY=240 StartZ=0 EndX=-235 EndY=240 EndZ=0
    g3: LineSegment StartX=-235 StartY=240 StartZ=0 EndX=-235 EndY=2.84e-14 EndZ=0
    g4: ArcOfCircle CenterX=0 CenterY=0 CenterZ=0 NormalX=0 NormalY=0 NormalZ=1 AngleXU=0 Radius=166.5 StartAngle=0 EndAngle=3.14159
    g5: ArcOfCircle CenterX=200 CenterY=200 CenterZ=0 NormalX=0 NormalY=0 NormalZ=1 AngleXU=0 Radius=7 StartAngle=-9e-16 EndAngle=3.14159
    g6: ArcOfCircle CenterX=200 CenterY=180 CenterZ=0 NormalX=0 NormalY=0 NormalZ=1 AngleXU=0 Radius=7 StartAngle=3.14159 EndAngle=6.28319
    g7: LineSegment StartX=193 StartY=200 StartZ=0 EndX=193 EndY=180 EndZ=0
    g8: LineSegment StartX=207 StartY=180 StartZ=0 EndX=207 EndY=200 EndZ=0
    g9: ArcOfCircle CenterX=200 CenterY=60 CenterZ=0 NormalX=0 NormalY=0 NormalZ=1 AngleXU=0 Radius=7 StartAngle=0 EndAngle=3.14159
    g10: ArcOfCircle CenterX=200 CenterY=40 CenterZ=0 NormalX=0 NormalY=0 NormalZ=1 AngleXU=0 Radius=7 StartAngle=3.14159 EndAngle=6.28319
    g11: LineSegment StartX=193 StartY=60 StartZ=0 EndX=193 EndY=40 EndZ=0
    g12: LineSegment StartX=207 StartY=40 StartZ=0 EndX=207 EndY=60 EndZ=0
    g13: ArcOfCircle CenterX=-200 CenterY=200.393 CenterZ=0 NormalX=0 NormalY=0 NormalZ=1 AngleXU=0 Radius=7 StartAngle=3e-16 EndAngle=3.14159
    g14: ArcOfCircle CenterX=-200 CenterY=180.393 CenterZ=0 NormalX=0 NormalY=0 NormalZ=1 AngleXU=0 Radius=7 StartAngle=3.14159 EndAngle=6.28319
    g15: LineSegment StartX=-207 StartY=200.393 StartZ=0 EndX=-207 EndY=180.393 EndZ=0
    g16: LineSegment StartX=-193 StartY=180.393 StartZ=0 EndX=-193 EndY=200.393 EndZ=0
    g17: ArcOfCircle CenterX=-200 CenterY=60.3929 CenterZ=0 NormalX=0 NormalY=0 NormalZ=1 AngleXU=0 Radius=7 StartAngle=0 EndAngle=3.14159
    g18: ArcOfCircle CenterX=-200 CenterY=40.3929 CenterZ=0 NormalX=0 NormalY=0 NormalZ=1 AngleXU=0 Radius=7 StartAngle=3.14159 EndAngle=6.28319
    g19: LineSegment StartX=-207 StartY=60.3929 StartZ=0 EndX=-207 EndY=40.3929 EndZ=0
    g20: LineSegment StartX=-193 StartY=40.3929 StartZ=0 EndX=-193 EndY=60.3929 EndZ=0
    g21: LineSegment StartX=207.004 StartY=200.734 StartZ=0 EndX=-193 EndY=200.393 EndZ=0
    g22: LineSegment StartX=166.5 StartY=0 StartZ=0 EndX=235 EndY=0 EndZ=0
  constraints (58):
    c: Coincident(g22,g1)
    c: Coincident(g1,g2)
    c: Coincident(g2,g3)
    c: Coincident(g3,g0)
    c: Horizontal(g0)
    c: Vertical(g1)
    c: Vertical(g3)
    c: PointOnObject(g0,g-1)
    c: Coincident(g4,g-1)
    c: Radius(g4) = 166.5
    c: DistanceX(g2,g2) = 470
    c: Symmetric(g1,g2,g-2)
    c: DistanceY(g1,g1) = 240
    c: DistanceX(g5,g5) = 14
    c: DistanceY(g7,g7) = 20
    c: DistanceY(g5,g1) = 40
    c: DistanceX(g4,g5) = 200
    c: Tangent(g9,g11) = -1.5708
    c: Tangent(g11,g10) = -1.5708
    c: Tangent(g10,g12) = -1.5708
    c: Tangent(g12,g9) = -1.5708
    c: Equal(g9,g10)
    c: Vertical(g11)
    c: Equal(g5,g9) = 14
    c: Equal(g7,g11) = 20
    c: Vertical(g9,g6)
    c: DistanceY(g9,g5) = 140
    c: Equal(g5,g13) = 14
    c: Equal(g7,g15) = 20
    c: Tangent(g17,g19) = -1.5708
    c: Tangent(g19,g18) = -1.5708
    c: Tangent(g18,g20) = -1.5708
    c: Tangent(g20,g17) = -1.5708
    c: Equal(g17,g18)
    c: Vertical(g19)
    c: Equal(g13,g17) = 14
    c: Equal(g15,g19) = 20
    c: Vertical(g17,g14)
    c: DistanceY(g17,g13) = 140
    c: Angle(g21) = -3.14074
    c: Coincident(g0,g4)
    c: Coincident(g22,g4)
    c: Horizontal(g22)
    c: PointOnObject(g1,g-1)
    c: Vertical(g16)
    c: Vertical(g15)
    c: Coincident(g13,g21)
    c: Tangent(g5,g8) = -1.5708
    c: Tangent(g16,g13) = -1.5708
    c: Tangent(g15,g14) = -1.5708
    c: Tangent(g16,g14) = -1.5708
    c: Tangent(g15,g13) = -1.5708
    c: DistanceX(g13,g4) = 200
    c: Vertical(g8)
    c: Vertical(g7)
    c: Tangent(g5,g7) = -1.5708
    c: Tangent(g7,g6) = -1.5708
    c: Tangent(g8,g6) = -1.5708
FEATURE [Part::Extrusion] Extrude036
  Base = -> Sketch057
  Dir = (0,-1,2e-16)
  DirMode = 2
  FaceMakerClass = Part::FaceMakerBullseye
  LengthFwd = 10
  LengthRev = 0
  Solid = true
  Symmetric = false
FEATURE [Sketcher::SketchObject] Sketch058
  ExternalGeometry = -> [Extrude036]
  FullyConstrained = false
  Placement = pos=(0,0,0) rot=(1,0,0;1.5708rad)
  sketch-geometry (26):
    g0: LineSegment StartX=-235 StartY=0 StartZ=0 EndX=-166.5 EndY=-4.08e-14 EndZ=0
    g1: LineSegment StartX=235 StartY=0 StartZ=0 EndX=235 EndY=-267.623 EndZ=0
    g2: LineSegment StartX=235 StartY=-267.623 StartZ=0 EndX=-235 EndY=-267.623 EndZ=0
    g3: LineSegment StartX=-235 StartY=-267.623 StartZ=0 EndX=-235 EndY=0 EndZ=0
    g4: ArcOfCircle CenterX=0 CenterY=-4.08e-14 CenterZ=0 NormalX=0 NormalY=0 NormalZ=1 AngleXU=0 Radius=166.5 StartAngle=3.14159 EndAngle=6.28319
    g5: ArcOfCircle CenterX=200 CenterY=-40 CenterZ=0 NormalX=0 NormalY=0 NormalZ=1 AngleXU=0 Radius=7 StartAngle=3e-16 EndAngle=3.14159
    g6: ArcOfCircle CenterX=200 CenterY=-60 CenterZ=0 NormalX=0 NormalY=0 NormalZ=1 AngleXU=0 Radius=7 StartAngle=3.14159 EndAngle=6.28319
    g7: LineSegment StartX=193 StartY=-40 StartZ=0 EndX=193 EndY=-60 EndZ=0
    g8: LineSegment StartX=207 StartY=-60 StartZ=0 EndX=207 EndY=-40 EndZ=0
    g9: ArcOfCircle CenterX=200 CenterY=-210 CenterZ=0 NormalX=0 NormalY=0 NormalZ=1 AngleXU=0 Radius=7 StartAngle=0 EndAngle=3.14159
    g10: ArcOfCircle CenterX=200 CenterY=-230 CenterZ=0 NormalX=0 NormalY=0 NormalZ=1 AngleXU=0 Radius=7 StartAngle=3.14159 EndAngle=6.28319
    g11: LineSegment StartX=193 StartY=-210 StartZ=0 EndX=193 EndY=-230 EndZ=0
    g12: LineSegment StartX=207 StartY=-230 StartZ=0 EndX=207 EndY=-210 EndZ=0
    g13: ArcOfCircle CenterX=-200 CenterY=-40 CenterZ=0 NormalX=0 NormalY=0 NormalZ=1 AngleXU=0 Radius=7 StartAngle=0 EndAngle=3.14159
    g14: ArcOfCircle CenterX=-200 CenterY=-60 CenterZ=0 NormalX=0 NormalY=0 NormalZ=1 AngleXU=0 Radius=7 StartAngle=3.14159 EndAngle=6.28319
    g15: LineSegment StartX=-207 StartY=-40 StartZ=0 EndX=-207 EndY=-60 EndZ=0
    g16: LineSegment StartX=-193 StartY=-60 StartZ=0 EndX=-193 EndY=-40 EndZ=0
    g17: ArcOfCircle CenterX=-200 CenterY=-210 CenterZ=0 NormalX=0 NormalY=0 NormalZ=1 AngleXU=0 Radius=7 StartAngle=1.4e-15 EndAngle=3.14159
    g18: ArcOfCircle CenterX=-200 CenterY=-230 CenterZ=0 NormalX=0 NormalY=0 NormalZ=1 AngleXU=0 Radius=7 StartAngle=3.14159 EndAngle=6.28319
    g19: LineSegment StartX=-207 StartY=-210 StartZ=0 EndX=-207 EndY=-230 EndZ=0
    g20: LineSegment StartX=-193 StartY=-230 StartZ=0 EndX=-193 EndY=-210 EndZ=0
    g21: LineSegment StartX=166.5 StartY=-4.08e-14 StartZ=0 EndX=235 EndY=0 EndZ=0
    g22: ArcOfCircle CenterX=0 CenterY=-210 CenterZ=0 NormalX=0 NormalY=0 NormalZ=1 AngleXU=0 Radius=7 StartAngle=-9e-16 EndAngle=3.14159
    g23: ArcOfCircle CenterX=0 CenterY=-230 CenterZ=0 NormalX=0 NormalY=0 NormalZ=1 AngleXU=0 Radius=7 StartAngle=3.14159 EndAngle=6.28319
    g24: LineSegment StartX=-7 StartY=-210 StartZ=0 EndX=-7 EndY=-230 EndZ=0
    g25: LineSegment StartX=7 StartY=-230 StartZ=0 EndX=7 EndY=-210 EndZ=0
  constraints (65):
    c: Coincident(g21,g1)
    c: Coincident(g1,g2)
    c: Coincident(g2,g3)
    c: Coincident(g3,g0)
    c: Horizontal(g2)
    c: Vertical(g1)
    c: Vertical(g3)
    c: Coincident(g21,g-3)
    c: Coincident(g0,g-4)
    c: Coincident(g4,g-1)
    c: Horizontal(g4,g4)
    c: Horizontal(g4,g4)
    c: Tangent(g5,g7) = -1.5708
    c: Tangent(g7,g6) = -1.5708
    c: Tangent(g6,g8) = -1.5708
    c: Tangent(g8,g5) = -1.5708
    c: Equal(g5,g6)
    c: Vertical(g7)
    c: DistanceY(g8,g8) = 20
    c: DistanceX(g5,g5) = 14
    c: Vertical(g5,g-5)
    c: DistanceY(g5,g4) = 40
    c: Tangent(g9,g11) = -1.5708
    c: Tangent(g11,g10) = -1.5708
    c: Tangent(g10,g12) = -1.5708
    c: Tangent(g12,g9) = -1.5708
    c: Equal(g9,g10)
    c: Vertical(g11)
    c: Equal(g8,g12) = 20
    c: Equal(g5,g9) = 14
    c: Vertical(g6,g9)
    c: Tangent(g13,g15) = -1.5708
    c: Tangent(g15,g14) = -1.5708
    c: Tangent(g14,g16) = -1.5708
    c: Tangent(g16,g13) = -1.5708
    c: Equal(g13,g14)
    c: Vertical(g15)
    c: Equal(g8,g16) = 20
    c: Equal(g5,g13) = 14
    c: Tangent(g17,g19) = -1.5708
    c: Tangent(g19,g18) = -1.5708
    c: Tangent(g18,g20) = -1.5708
    c: Tangent(g20,g17) = -1.5708
    c: Equal(g17,g18)
    c: Vertical(g19)
    c: Equal(g16,g20) = 20
    c: Equal(g13,g17) = 14
    c: Vertical(g14,g17)
    c: Tangent(g22,g24) = -1.5708
    c: Tangent(g24,g23) = -1.5708
    c: Tangent(g23,g25) = -1.5708
    c: Tangent(g25,g22) = -1.5708
    c: Equal(g22,g23)
    c: Vertical(g24)
    c: DistanceX(g22,g22) = 14
    c: DistanceY(g24,g24) = 20
    c: PointOnObject(g22,g-2)
    c: Horizontal(g9,g22)
    c: DistanceY(g9,g5) = 170
    c: DistanceY(g17,g13) = 170
    c: DistanceX(g14,g6) = 400
    c: DistanceY(g13,g0) = 40
    c: Coincident(g0,g4)
    c: Coincident(g4,g21)
    c: Radius(g4) = 166.5
FEATURE [Part::Extrusion] Extrude037
  Base = -> Sketch058
  Dir = (0,-1,2e-16)
  DirMode = 2
  FaceMakerClass = Part::FaceMakerBullseye
  LengthFwd = 10
  LengthRev = 0
  Solid = true
  Symmetric = false
FEATURE [App::Part] Part014  label="pipeBrg"
  Group = -> [Sketch057,Sketch058,Extrude036,Extrude037]
  Origin = -> Origin018
  Placement = pos=(0,-1538.75,1787.43) rot=(0,0,1;0rad)
FEATURE [Part::Compound] Compound026  label="Brg"
  Links = -> [Part014]
  Placement = pos=(-8.34222,5.69e-13,72.567) rot=(0,0,1;1.5708rad)
FEATURE [Part::Compound] Compound027  label="centerWell"
  Links = -> [Cut021,Extrude032,Cut023]
FEATURE [Sketcher::SketchObject] Sketch059
  ExternalGeometry = -> [Compound027]
  FullyConstrained = false
  sketch-geometry (4):
    g0: LineSegment StartX=1549.19 StartY=50 StartZ=0 EndX=1757.19 EndY=50 EndZ=0
    g1: LineSegment StartX=1757.19 StartY=50 StartZ=0 EndX=1757.19 EndY=-50 EndZ=0
    g2: LineSegment StartX=1757.19 StartY=-50 StartZ=0 EndX=1549.19 EndY=-50 EndZ=0
    g3: ArcOfCircle CenterX=-0.000694137 CenterY=-2.8392e-12 CenterZ=0 NormalX=0 NormalY=0 NormalZ=1 AngleXU=0 Radius=1550 StartAngle=6.25092 EndAngle=6.31545
  constraints (12):
    c: Horizontal(g0)
    c: Coincident(g0,g1)
    c: Vertical(g1)
    c: Coincident(g1,g2)
    c: Horizontal(g2)
    c: DistanceY(g-1,g0) = 50
    c: DistanceY(g1,g1) = 100
    c: Coincident(g3,g2)
    c: Coincident(g3,g0)
    c: PointOnObject(g0,g-5)
    c: PointOnObject(g2,g-6)
    c: DistanceX(g0,g0) = 208
FEATURE [Part::Extrusion] Extrude038
  Base = -> Sketch059
  Dir = (0,0,1)
  DirMode = 2
  FaceMakerClass = Part::FaceMakerBullseye
  LengthFwd = 10
  LengthRev = 0
  Solid = true
  Symmetric = false
FEATURE [Sketcher::SketchObject] Sketch060
  ExternalGeometry = -> [Extrude038,Compound027]
  FullyConstrained = true
  MapMode = 5
  Placement = pos=(0,0,10) rot=(0,0,1;0rad)
  Support = -> [Extrude038]
  sketch-geometry (8):
    g0: LineSegment StartX=1549.19 StartY=50 StartZ=0 EndX=1757.19 EndY=50 EndZ=0
    g1: LineSegment StartX=1757.19 StartY=50 StartZ=0 EndX=1757.19 EndY=45 EndZ=0
    g2: LineSegment StartX=1757.19 StartY=45 StartZ=0 EndX=1549.19 EndY=45 EndZ=0
    g3: LineSegment StartX=1549.19 StartY=45 StartZ=0 EndX=1549.19 EndY=50 EndZ=0
    g4: LineSegment StartX=1549.19 StartY=-50 StartZ=0 EndX=1757.19 EndY=-50 EndZ=0
    g5: LineSegment StartX=1757.19 StartY=-50 StartZ=0 EndX=1757.19 EndY=-45 EndZ=0
    g6: LineSegment StartX=1757.19 StartY=-45 StartZ=0 EndX=1549.19 EndY=-45 EndZ=0
    g7: LineSegment StartX=1549.19 StartY=-45 StartZ=0 EndX=1549.19 EndY=-50 EndZ=0
  constraints (22):
    c: Coincident(g0,g1)
    c: Coincident(g1,g2)
    c: Coincident(g2,g3)
    c: Coincident(g3,g0)
    c: Horizontal(g0)
    c: Horizontal(g2)
    c: Vertical(g1)
    c: Vertical(g3)
    c: Coincident(g4,g5)
    c: Coincident(g5,g6)
    c: Coincident(g6,g7)
    c: Coincident(g7,g4)
    c: Horizontal(g4)
    c: Horizontal(g6)
    c: Vertical(g5)
    c: Vertical(g7)
    c: Coincident(g0,g-3)
    c: DistanceY(g1,g1) = 5
    c: DistanceY(g5,g5) = 5
    c: Coincident(g4,g-3)
    c: Vertical(g2,g6)
    c: PointOnObject(g4,g-4)
FEATURE [Part::Extrusion] Extrude039
  Base = -> Sketch060
  Dir = (0,0,1)
  DirMode = 2
  FaceMakerClass = Part::FaceMakerBullseye
  LengthFwd = 200
  LengthRev = 0
  Solid = true
  Symmetric = false
FEATURE [Part::Chamfer] Chamfer
  Base = -> Extrude039
  Edges = 2 edges: [Edge7 r1=130 r2=70,Edge19 r1=130 r2=70]
FEATURE [Part::Compound] Compound002  label="gusset"
  Links = -> [Extrude038,Chamfer]
FEATURE [Sketcher::SketchObject] Sketch061
  ExternalGeometry = -> [Compound002]
  FullyConstrained = true
  MapMode = 5
  Placement = pos=(0,0,10) rot=(0,0,1;0rad)
  Support = -> [Compound002]
  sketch-geometry (1):
    g0: Circle CenterX=1732.19 CenterY=0 CenterZ=0 NormalX=0 NormalY=0 NormalZ=1 AngleXU=0 Radius=7
  constraints (3):
    c: Diameter(g0) = 14
    c: PointOnObject(g0,g-1)
    c: Distance(g0,g-3) = 25
FEATURE [Part::Extrusion] Extrude040
  Base = -> Sketch061
  Dir = (0,0,1)
  DirMode = 2
  FaceMakerClass = Part::FaceMakerBullseye
  LengthFwd = 10
  LengthRev = 0
  Reversed = true
  Solid = true
  Symmetric = false
FEATURE [Part::Cut] Cut024
  Base = -> Compound002
  Placement = pos=(0,0,1200) rot=(0,0,1;0rad)
  Tool = -> Extrude040
  expr: .Placement.Base.z = Spreadsheet005.h1
FEATURE [Spreadsheet::Sheet] Spreadsheet006  label="Spreadsheet_support"
  cells = A1='tankDia   D; B1(D0)=15500; A2='梁成H0; B2(H0)=600; A3='梁長L0; B3(L0)==D0 - 500; A4='玄材shp; B4(shp)='50x50x6; A5='玄材ゲージラインGL0; B5(GL0)=30; A6='ラチス材Lshp; B6(Lshp)='6x38; A7='ラチス材幅Lb0; B7(Lb0)=38; A8='ラチス材厚Lt0; B8(Gt0)=6; A9='ガセットプレート幅Gb0; B9(Gb0)=120; A10='ラチスピッチrp0; B10(rp0)==(L0 - 2 * Gb0) / rn0; A11='ラチス配列数rn0; B11(rn0)==D0 / H0; B16='t; C16='A; D16='GLine; A17='40x40x3; B17=3; C17=40; D17=22; A18='40x40x5; B18=5; C18=40; D18=22; A19='50x50x4; B19=4; C19=50; D19=30; A20='50x50x6; B20=6; C20=50; D20=30; A21='65x65x6; B21=6; C21=65; D21=35; A22='65x65x8; B22=8; C22=65; D22=35; A23='75x75x6; B23=6; C23=75; D23=40; A24='75x75x9; B24=9; C24=75; D24=40; A25='75x75x12; B25=12; C25=75; D25=40; A26='90x90x7; B26=7; C26=90; D26=50; A27='90x90x10; B27=10; C27=90; D27=50; A28='90x90x13; B28=13; C28=90; D28=50; A29='100x100x7; B29=7; C29=100; D29=55; A30='100x100x10; B30=10; C30=100; D30=55; A31='100x100x13; B31=13; C31=100; D31=55; A34='6x38; B34=6; C34=38; A35='9x38; B35=9; C35=38; A36='6x44; B36=6; C36=44; A37='9x44; B37=9; C37=44; A38='4.5x50; B38=4.5; C38=50; A39='6x50; B39=6; C39=50; A40='9x50; B40=9; C40=50; A41='6x65; B41=6; C41=65; A42='9x65; B42=9; C42=65; A43='6x75; B43=6; C43=75; A44='9x75; B44=9; C44=75; A45='6x90; B45=6; C45=90; A46='9x90; B46=9; C46=90
FEATURE [Part::FeaturePython] AngleSteel016  label="AngleSteel002"  # WARN: FeaturePython — macro-defined, semantics opaque (R4)
  A = 50
  B = 50
  L = 1000
  Placement = pos=(0,28.8,14.4) rot=(0,0,1;1.5708rad)
  Solid = false
  g0 = 7.85
  mass = 0
  size = 7
  standard = SS_Equal
  t = 8
FEATURE [Part::Mirroring] Mirror014  label="AngleSteel (mirrored)"
  Base = (-2.54e-14,114.396,14.3963)
  Normal = (0,0,-1)
  Placement = pos=(0,0,600) rot=(0,0,1;0rad)
  Source = -> AngleSteel016
  expr: .Placement.Base.z = Spreadsheet006.H0
FEATURE [Part::Extrusion] Extrude043
  Base = -> AngleSteel016
  Dir = (-1,2e-16,0)
  DirMode = 2
  FaceMakerClass = Part::FaceMakerBullseye
  LengthFwd = 15000
  LengthRev = 0
  Reversed = true
  Solid = false
  Symmetric = false
  expr: LengthFwd = Spreadsheet006.L0
FEATURE [Part::Extrusion] Extrude044
  Base = -> Mirror014
  Dir = (-1,2e-16,0)
  DirMode = 2
  FaceMakerClass = Part::FaceMakerBullseye
  LengthFwd = 15000
  LengthRev = 0
  Reversed = true
  Solid = false
  Symmetric = false
  expr: LengthFwd = Spreadsheet006.L0
FEATURE [Sketcher::SketchObject] Sketch062
  ExternalGeometry = -> [Extrude044,Extrude043]
  FullyConstrained = false
  Placement = pos=(0,0,0) rot=(1,0,0;1.5708rad)
  expr: Constraints[2] = Spreadsheet006.Gb0
  expr: Constraints[5] = Spreadsheet006.rp0
  expr: Constraints[8] = Spreadsheet006.H0 - 60
  sketch-geometry (3):
    g0: LineSegment StartX=120 StartY=44.4 StartZ=0 EndX=405.677 EndY=584.4 EndZ=0
    g1: LineSegment StartX=405.677 StartY=584.4 StartZ=0 EndX=691.355 EndY=44.4 EndZ=0
    g2: LineSegment StartX=405.677 StartY=584.4 StartZ=0 EndX=405.677 EndY=511.834 EndZ=0
  constraints (9):
    c: Coincident(g0,g1)
    c: Horizontal(g0,g1)
    c: DistanceX(g-1,g0) = 120
    c: Coincident(g2,g0)
    c: Symmetric(g1,g0,g2)
    c: DistanceX(g0,g1) = 571.355
    c: DistanceY(g-1,g-4) = 14.4
    c: DistanceY(g-4,g0) = 30
    c: DistanceY(g0,g0) = 540
FEATURE [Sketcher::SketchObject] Sketch063
  ExternalGeometry = -> [Sketch062,Extrude043]
  FullyConstrained = true
  Placement = pos=(0,0,14.4) rot=(1,0,0;1.5708rad)
  expr: Constraints[23] = Spreadsheet006.Lb0
  expr: Constraints[24] = Spreadsheet006.H0 - 20
  expr: Constraints[25] = Spreadsheet006.Lb0 / 2
  sketch-geometry (9):
    g0: LineSegment StartX=120 StartY=70.6308 StartZ=0 EndX=394.763 EndY=590 EndZ=0
    g1: LineSegment StartX=405.677 StartY=529.369 StartZ=0 EndX=130.914 EndY=10 EndZ=0
    g2: LineSegment StartX=405.677 StartY=529.369 StartZ=0 EndX=680.44 EndY=10 EndZ=0
    g3: LineSegment StartX=691.355 StartY=70.6308 StartZ=0 EndX=416.592 EndY=590 EndZ=0
    g4: LineSegment StartX=394.763 StartY=590 StartZ=0 EndX=416.592 EndY=590 EndZ=0
    g5: LineSegment StartX=680.44 StartY=10 StartZ=0 EndX=691.355 EndY=10 EndZ=0
    g6: LineSegment StartX=691.355 StartY=10 StartZ=0 EndX=691.355 EndY=70.6308 EndZ=0
    g7: LineSegment StartX=130.914 StartY=10 StartZ=0 EndX=120 EndY=10 EndZ=0
    g8: LineSegment StartX=120 StartY=10 StartZ=0 EndX=120 EndY=70.6308 EndZ=0
  constraints (27):
    c: Coincident(g7,g8)
    c: Coincident(g0,g8)
    c: Coincident(g1,g7)
    c: Coincident(g0,g4)
    c: Coincident(g1,g2)
    c: Coincident(g3,g4)
    c: Coincident(g2,g5)
    c: Coincident(g5,g6)
    c: Coincident(g3,g6)
    c: Horizontal(g7)
    c: Horizontal(g4)
    c: Vertical(g8)
    c: Vertical(g7,g-4)
    c: Horizontal(g0,g3)
    c: Horizontal(g5)
    c: Horizontal(g1,g2)
    c: Vertical(g6)
    c: PointOnObject(g-3,g6)
    c: Parallel(g1,g-4)
    c: Parallel(g1,g0)
    c: Parallel(g2,g-3)
    c: Parallel(g-3,g3)
    c: Vertical(g1,g-4)
    c: Distance(g1,g0) = 38
    c: DistanceY(g2,g3) = 580
    c: Distance(g1,g-4) = 19
    c: DistanceY(g-5,g7) = 10
FEATURE [Part::Extrusion] Extrude041  label="Extrude010"
  Base = -> Sketch063
  Dir = (0,-1,2e-16)
  DirMode = 2
  FaceMakerClass = Part::FaceMakerBullseye
  LengthFwd = 6
  LengthRev = 0
  Placement = pos=(0,28.8,0) rot=(0,0,1;0rad)
  Solid = true
  Symmetric = false
FEATURE [Part::FeaturePython] Array023  # Draft array (typed FeaturePython)
  AlwaysSyncPlacement = false
  Angle = 360
  ArrayType = 0
  Axis = (0,0,1)
  Base = -> Extrude041
  Center = (0,0,0)
  Count = 26
  ExpandArray = false
  Fuse = false
  IntervalAxis = (0,0,0)
  IntervalX = (571.355,0,0)
  IntervalY = (0,100,0)
  IntervalZ = (0,0,100)
  NumberCircles = 3
  NumberPolar = 5
  NumberX = 26
  NumberY = 1
  NumberZ = 1
  PlacementList = 26 placements: arithmetic series from (0,28.8,0) step (571.355,0,0) to (14283.9,28.8,0)
  RadialDistance = 50
  ScaleList = (26) [(1,1,1),(1,1,1),(1,1,1),(1,1,1),(1,1,1),(1,1,1),(1,1,1),(1,1,1),(1,1,1),(1,1,1),(1,1,1),(1,1,1),(1,1,1),(1,1,1),(1,1,1),(1,1,1),(1,1,1),(1,1,1),+8 more]
  Symmetry = 1
  TangentialDistance = 25
  expr: .IntervalX.x = Spreadsheet006.rp0
  expr: NumberX = Spreadsheet006.rn0
FEATURE [Sketcher::SketchObject] Sketch064
  ExternalGeometry = -> [Extrude041]
  FullyConstrained = true
  Placement = pos=(0,0,14.4) rot=(1,0,0;1.5708rad)
  expr: Constraints[22] = Spreadsheet006.L0
  sketch-geometry (8):
    g0: LineSegment StartX=0 StartY=10 StartZ=0 EndX=120 EndY=10 EndZ=0
    g1: LineSegment StartX=120 StartY=10 StartZ=0 EndX=120 EndY=590 EndZ=0
    g2: LineSegment StartX=120 StartY=590 StartZ=0 EndX=0 EndY=590 EndZ=0
    g3: LineSegment StartX=0 StartY=590 StartZ=0 EndX=0 EndY=10 EndZ=0
    g4: LineSegment StartX=15000 StartY=590 StartZ=0 EndX=14880 EndY=590 EndZ=0
    g5: LineSegment StartX=14880 StartY=590 StartZ=0 EndX=14880 EndY=10 EndZ=0
    g6: LineSegment StartX=14880 StartY=10 StartZ=0 EndX=15000 EndY=10 EndZ=0
    g7: LineSegment StartX=15000 StartY=10 StartZ=0 EndX=15000 EndY=590 EndZ=0
  constraints (23):
    c: Coincident(g0,g1)
    c: Coincident(g1,g2)
    c: Coincident(g2,g3)
    c: Coincident(g3,g0)
    c: Horizontal(g0)
    c: Horizontal(g2)
    c: Vertical(g1)
    c: Vertical(g3)
    c: Vertical(g-1,g0)
    c: Coincident(g0,g-3)
    c: Horizontal(g1,g-4)
    c: Coincident(g4,g5)
    c: Coincident(g5,g6)
    c: Coincident(g6,g7)
    c: Coincident(g7,g4)
    c: Horizontal(g4)
    c: Horizontal(g6)
    c: Vertical(g5)
    c: Vertical(g7)
    c: Equal(g0,g6)
    c: Horizontal(g6,g0)
    c: Horizontal(g1,g4)
    c: DistanceX(g0,g6) = 15000
FEATURE [Part::Extrusion] Extrude042
  Base = -> Sketch064
  Dir = (0,-1,2e-16)
  DirMode = 2
  FaceMakerClass = Part::FaceMakerBullseye
  LengthFwd = 6
  LengthRev = 0
  Placement = pos=(0,28.8,0) rot=(0,0,1;0rad)
  Solid = true
  Symmetric = false
  expr: LengthFwd = Spreadsheet006.Gt0
FEATURE [Part::MultiFuse] Fusion003  label="Fusion001"
  Shapes = -> [Extrude044,Extrude043]
FEATURE [Part::Mirroring] Mirror001  label="Fusion (mirrored)"
  Base = (-3.2e-15,28.7963,514.396)
  Normal = (0,-1,0)
  Placement = pos=(0,-6,0) rot=(0,0,1;0rad)
  Source = -> Fusion003
  expr: .Placement.Base.y = -Spreadsheet006.Gt0
FEATURE [Sketcher::SketchObject] Sketch065
  FullyConstrained = true
  Placement = pos=(0,0,0) rot=(1,0,0;1.5708rad)
  sketch-geometry (4):
    g0: LineSegment StartX=0 StartY=0 StartZ=0 EndX=150 EndY=0 EndZ=0
    g1: LineSegment StartX=150 StartY=0 StartZ=0 EndX=150 EndY=300 EndZ=0
    g2: LineSegment StartX=150 StartY=300 StartZ=0 EndX=0 EndY=300 EndZ=0
    g3: LineSegment StartX=0 StartY=300 StartZ=0 EndX=0 EndY=0 EndZ=0
  constraints (11):
    c: Coincident(g0,g1)
    c: Coincident(g1,g2)
    c: Coincident(g2,g3)
    c: Coincident(g3,g0)
    c: Horizontal(g0)
    c: Horizontal(g2)
    c: Vertical(g1)
    c: Vertical(g3)
    c: Coincident(g0,g-1)
    c: DistanceX(g2,g2) = 150
    c: DistanceY(g1,g1) = 300
FEATURE [Part::Extrusion] Extrude045
  Base = -> Sketch065
  Dir = (0,-1,-3e-16)
  DirMode = 2
  FaceMakerClass = Part::FaceMakerBullseye
  LengthFwd = 6
  LengthRev = 0
  Solid = true
  Symmetric = true
FEATURE [Part::FeaturePython] AngleSteel017  label="AngleSteel019"  # WARN: FeaturePython — macro-defined, semantics opaque (R4)
  A = 75
  B = 75
  L = 300
  Placement = pos=(117.5,40.5,0) rot=(0,0,1;3.14159rad)
  Solid = true
  g0 = 7.85
  mass = 2.05506
  size = 10
  standard = SS_Equal
  t = 6
FEATURE [Part::Mirroring] Mirror004  label="AngleSteel003 (mirrored)"
  Base = (200,0,0)
  Normal = (0,1,0)
  Source = -> AngleSteel017
FEATURE [Part::Compound] Compound028  label="gusset001"
  Links = -> [Extrude045,Mirror004,AngleSteel017]
  Placement = pos=(7450,-1710,750) rot=(0,0,1;0rad)
  expr: .Placement.Base.x = Spreadsheet005.D0 / 2 - 300
  expr: .Placement.Base.y = -<<Spreadsheet_feedWell>>.dia / 2 - 160
  expr: .Placement.Base.z = Spreadsheet005.h1 - 450
FEATURE [Part::Compound] Compound029
  Links = -> [Mirror001,Fusion003]
FEATURE [App::Part] Part017  label="latticeBeam"
  Group = -> [Sketch062,Sketch064,Sketch063,Fusion003,Mirror014,Mirror001,Extrude041,Extrude042,Extrude044,Extrude043,Array023,AngleSteel016,Compound029]
  Origin = -> Origin021
  Placement = pos=(-7500,-1730,785) rot=(0,0,1;0rad)
  expr: .Placement.Base.x = -Spreadsheet006.L0 / 2
  expr: .Placement.Base.y = -Spreadsheet005.dia / 2 - 180
  expr: .Placement.Base.z = Spreadsheet005.h1 - 415
FEATURE [Part::Mirroring] Mirror015  label="latticeBeam (mirrored)"
  Base = (-1000,0,0)
  Normal = (0,1,0)
  Source = -> Part017
FEATURE [App::Part] Part016  label="support"
  Group = -> [Part017,Mirror015]
  Origin = -> Origin020
  Placement = pos=(0,0,-200) rot=(0,0,1;0rad)
FEATURE [Part::FeaturePython] Array024  # Draft array (typed FeaturePython)
  AlwaysSyncPlacement = false
  Angle = 360
  ArrayType = 1
  Axis = (0,0,1)
  Base = -> Cut024
  Center = (0,0,0)
  Count = 4
  ExpandArray = false
  Fuse = false
  IntervalAxis = (0,0,0)
  IntervalX = (50,0,0)
  IntervalY = (0,50,0)
  IntervalZ = (0,0,50)
  NumberCircles = 3
  NumberPolar = 4
  NumberX = 2
  NumberY = 2
  NumberZ = 1
  PlacementList = 4 placements: [(0,0,1200),(0,0,1200),(0,0,1200),(0,0,1200)]
  RadialDistance = 50
  ScaleList = (4) [(1,1,1),(1,1,1),(1,1,1),(1,1,1)]
  Symmetry = 1
  TangentialDistance = 25
FEATURE [App::Part] Part015  label="centerWell001"
  Group = -> [Chamfer,Sketch056,Sketch061,Sketch060,Sketch059,Compound027,Compound002,Revolve011,Revolve012,Revolve013,Extrude032,Extrude039,Extrude035,Extrude034,Extrude031,Extrude033,Extrude038,Extrude040,Sketch052,Sketch054,Sketch051,Sketch053,Sketch055,AngleSteel014,AngleSteel015,Cut024,Fusion002,Cut022,Cut021,Cut023,Array024]
  Origin = -> Origin019
  Placement = pos=(0,0,0) rot=(0,0,1;1.5708rad)
FEATURE [Part::Mirroring] Mirror016  label="gusset001 (mirrored)"
  Base = (0,0,0)
  Normal = (1,0,0)
  Source = -> Compound028
FEATURE [Part::Mirroring] Mirror017  label="gusset001 (mirrored) (mirrored)"
  Base = (0,0,0)
  Normal = (0,1,0)
  Source = -> Mirror016
FEATURE [Part::Mirroring] Mirror018  label="gusset001 (mirrored)001"
  Base = (0,0,0)
  Normal = (0,1,0)
  Source = -> Compound028
FEATURE [Part::FeaturePython] ChannelSteel004  label="ChannelSteel"  # WARN: FeaturePython — macro-defined, semantics opaque (R4)
  B = 65
  H = 125
  L = 3400
  Placement = pos=(1720,-1701.5,3.61e-13) rot=(-1,0,0;1.5708rad)
  Solid = true
  g0 = 7.85
  mass = 41.0702
  size = 2
  standard = SS
  t1 = 6
  t2 = 8
  expr: .Placement.Base.x = Spreadsheet005.dia / 2 + 170
  expr: .Placement.Base.y = -Spreadsheet005.dia / 2 - 101.5 - 50
  expr: L = Spreadsheet005.dia + 300
FEATURE [Part::FeaturePython] Array025  # Draft array (typed FeaturePython)
  AlwaysSyncPlacement = false
  Angle = 360
  ArrayType = 0
  Axis = (0,0,1)
  Base = -> ChannelSteel004
  Center = (0,0,0)
  Count = 2
  ExpandArray = false
  Fuse = false
  IntervalAxis = (0,0,0)
  IntervalX = (2975,0,0)
  IntervalY = (0,100,0)
  IntervalZ = (0,0,100)
  NumberCircles = 3
  NumberPolar = 5
  NumberX = 2
  NumberY = 1
  NumberZ = 1
  Placement = pos=(0,-0.000129987,1135.41) rot=(0,0,1;0rad)
  PlacementList = 2 placements: [(1720,-1701.5,3.61e-13),(4695,-1701.5,3.61e-13)]
  RadialDistance = 50
  ScaleList = (2) [(1,1,1),(1,1,1)]
  Symmetry = 1
  TangentialDistance = 25
  expr: .IntervalX.x = (<<Spreadsheet_support>>.L0 / 2 - <<Spreadsheet_feedWell>>.dia / 2) / 2
FEATURE [Sketcher::SketchObject] Sketch066
  FullyConstrained = true
  expr: Constraints[10] = Spreadsheet007.l0
  expr: Constraints[9] = Spreadsheet007.w0
  sketch-geometry (5):
    g0: LineSegment StartX=0 StartY=0 StartZ=0 EndX=2870 EndY=0 EndZ=0
    g1: LineSegment StartX=2870 StartY=0 StartZ=0 EndX=2870 EndY=3350 EndZ=0
    g2: LineSegment StartX=2870 StartY=3350 StartZ=0 EndX=0 EndY=3350 EndZ=0
    g3: LineSegment StartX=0 StartY=3350 StartZ=0 EndX=0 EndY=0 EndZ=0
    g4: LineSegment StartX=0 StartY=0 StartZ=0 EndX=2870 EndY=3350 EndZ=0
  constraints (14):
    c: Coincident(g0,g1)
    c: Coincident(g1,g2)
    c: Coincident(g2,g3)
    c: Coincident(g3,g0)
    c: Horizontal(g0)
    c: Horizontal(g2)
    c: Vertical(g1)
    c: Vertical(g3)
    c: Coincident(g0,g-1)
    c: Distance(g2) = 2870
    c: Distance(g1) = 3350
    c: Coincident(g4,g0)
    c: Coincident(g4,g1)
    c: Angle(g0,g4) = 0.862416
FEATURE [Spreadsheet::Sheet] Spreadsheet007
  cells = A2='rodDia dia; B2(dia)=12; C2='thickness; D2(t0)=6; E2='w0; F2(w0)=2870; G2='sita; H2(sita)==atan(l0 / w0); A3='length L0; B3(L0)==(w0 ^ 2 + l0 ^ 2) ^ 0.5; C3='l1; D3(l1)==L0 - (dia * 5 + 500); E3='l0; F3(l0)=3350; B4='l; C4='l1; D4='a; E4='b; F4='c; G4='e; H4='f; I4='g; J4='h; K4='i; L4='r; A5='forkEndR; B5=80; D5=25; E5=10; F5=14; G5=16; H5=13; I5=40; J5=5; K5=13; L5=15; A6='turnBackle; B6=100; C6=20; D6=30; E6=16; F6=22; A7='forkEndL; B7=60; D7=25; E7=10; F7=13; G7=16; H7=13; I7=20; L7=15; A8=1; B8=2; C8=3; D8=4; E8=5; F8=6; G8=7; H8=8; I8=9; J8=10; K8=11; L8=12; A9='turnBackle; A10='d; B10='l; C10='l1; D10='a; E10='b; F10='c; G10='t0; A11=10; B11=75; C11=15; D11=24; E11=13; F11=17; G11=6; A12=12; B12=100; C12=20; D12=30; E12=16; F12=22; G12=6; A13=16; B13=125; C13=24; D13=36; E13=20; F13=27; G13=9; A14=20; B14=150; C14=28; D14=42; E14=23; F14=33; G14=9; A15=22; B15=175; C15=33; D15=48; E15=27; F15=37; G15=9; A16=24; B16=200; C16=38; D16=54; E16=30; F16=42; G16=12; A17=30; B17=250; C17=47; D17=66; E17=37; F17=52; G17=12; A18='forkEnd_L; A19='d; B19='l; C19='a; D19='b; E19='c; F19='e; G19='f; H19='g; I19='r; A20=10; B20=50; C20=20; D20=7; E20=10; F20=12; G20=10; H20=15; I20=12; A21=12; B21=60; C21=25; D21=10; E21=13; F21=16; G21=13; H21=20; I21=15; A22=16; B22=75; C22=30; D22=13; E22=16; F22=20; G22=16; H22=25; I22=19; A23=20; B23=90; C23=40; D23=16; E23=20; F23=24; G23=20; H23=30; I23=23; A24=22; B24=100; C24=45; D24=20; E24=23; F24=28; G24=23; H24=35; I24=27; A25=24; B25=115; C25=50; D25=23; E25=26; F25=32; G25=26; H25=40; I25=30; A26=30; B26=140; C26=65; D26=30; E26=33; F26=40; G26=33; H26=50; I26=38; A27='forkEnd_R; A28='d; B28='l; C28='a; D28='b; E28='c; F28='r; +82 more cells
FEATURE [Sketcher::SketchObject] Sketch067
  FullyConstrained = true
  Placement = pos=(0,0,0) rot=(1,0,0;1.5708rad)
  expr: Constraints[11] = Spreadsheet007.I5 + Spreadsheet007.dia * 2
  expr: Constraints[1] = Spreadsheet007.F5 / 2
  expr: Constraints[3] = Spreadsheet007.L5
  sketch-geometry (5):
    g0: Circle CenterX=0 CenterY=0 CenterZ=0 NormalX=0 NormalY=0 NormalZ=1 AngleXU=0 Radius=7
    g1: ArcOfCircle CenterX=0 CenterY=0 CenterZ=0 NormalX=0 NormalY=0 NormalZ=1 AngleXU=0 Radius=15 StartAngle=4.71239 EndAngle=7.85398
    g2: LineSegment StartX=-4.87e-14 StartY=15 StartZ=0 EndX=-64 EndY=15 EndZ=0
    g3: LineSegment StartX=-64 StartY=15 StartZ=0 EndX=-64 EndY=-15 EndZ=0
    g4: LineSegment StartX=-64 StartY=-15 StartZ=0 EndX=0 EndY=-15 EndZ=0
  constraints (12):
    c: Coincident(g0,g-1)
    c: Radius(g0) = 7
    c: Coincident(g1,g0)
    c: Radius(g1) = 15
    c: Horizontal(g2)
    c: Coincident(g2,g3)
    c: Vertical(g3)
    c: Coincident(g3,g4)
    c: Horizontal(g4)
    c: Tangent(g1,g2) = -1.5708
    c: Tangent(g1,g4) = -1.5708
    c: Distance(g2) = 64
FEATURE [Part::Cylinder] Cylinder002  label="円柱001"
  Angle = 360
  AttacherType = Attacher::AttachEngine3D
  FirstAngle = 0
  Height = 500
  Placement = pos=(-24,0,0) rot=(0,-1,0;1.5708rad)
  Radius = 6
  SecondAngle = 0
  expr: .Placement.Base.x = -Spreadsheet007.dia * 2
  expr: Radius = Spreadsheet007.dia / 2
FEATURE [Sketcher::SketchObject] Sketch068
  FullyConstrained = true
  Placement = pos=(0,0,0) rot=(1,0,0;1.5708rad)
  expr: Constraints[10] = Spreadsheet007.C6
  expr: Constraints[11] = Spreadsheet007.B6
  expr: Constraints[12] = Spreadsheet007.D6 / 2
  expr: Constraints[13] = Spreadsheet007.F6 / 2
  expr: Constraints[14] = Spreadsheet007.B6 / 2
  expr: Constraints[17] = Spreadsheet007.C6
  sketch-geometry (6):
    g0: LineSegment StartX=-50 StartY=0 StartZ=0 EndX=-50 EndY=11 EndZ=0
    g1: LineSegment StartX=-50 StartY=11 StartZ=0 EndX=-30 EndY=15 EndZ=0
    g2: LineSegment StartX=-30 StartY=15 StartZ=0 EndX=30 EndY=15 EndZ=0
    g3: LineSegment StartX=30 StartY=15 StartZ=0 EndX=50 EndY=11 EndZ=0
    g4: LineSegment StartX=50 StartY=11 StartZ=0 EndX=50 EndY=0 EndZ=0
    g5: LineSegment StartX=50 StartY=0 StartZ=0 EndX=-50 EndY=0 EndZ=0
  constraints (18):
    c: PointOnObject(g0,g-1)
    c: Vertical(g0)
    c: Coincident(g0,g1)
    c: Coincident(g1,g2)
    c: Horizontal(g2)
    c: Coincident(g2,g3)
    c: Coincident(g3,g4)
    c: PointOnObject(g4,g-1)
    c: Vertical(g4)
    c: Coincident(g4,g5)
    c: DistanceX(g2,g3) = 20
    c: DistanceX(g0,g3) = 100
    c: Distance(g1,g5) = 15
    c: Distance(g4) = 11
    c: DistanceX(g-1,g4) = 50
    c: Horizontal(g0,g3)
    c: Coincident(g5,g0)
    c: DistanceX(g0,g1) = 20
FEATURE [Part::Revolution] Revolve014  label="Revolve003"
  Angle = 360
  Axis = (-1,0,0)
  AxisLink = -> Sketch068 [Edge6]
  Base = (-50,0,0)
  FaceMakerClass = Part::FaceMakerBullseye
  Solid = true
  Source = -> Sketch068
  Symmetric = false
FEATURE [Sketcher::SketchObject] Sketch069
  FullyConstrained = false
  Placement = pos=(0,0,0) rot=(0.57735,0.57735,0.57735;2.0944rad)
  expr: Constraints[16] = Spreadsheet007.F6
  expr: Constraints[17] = Spreadsheet007.F6 / 2
  sketch-geometry (8):
    g0: LineSegment StartX=-11 StartY=39.685 StartZ=0 EndX=-26 EndY=39.685 EndZ=0
    g1: LineSegment StartX=-26 StartY=39.685 StartZ=0 EndX=-26 EndY=-39.3666 EndZ=0
    g2: LineSegment StartX=-26 StartY=-39.3666 StartZ=0 EndX=-11 EndY=-39.3666 EndZ=0
    g3: LineSegment StartX=-11 StartY=-39.3666 StartZ=0 EndX=-11 EndY=39.685 EndZ=0
    g4: LineSegment StartX=11 StartY=39.685 StartZ=0 EndX=26 EndY=39.685 EndZ=0
    g5: LineSegment StartX=26 StartY=39.685 StartZ=0 EndX=26 EndY=-40.315 EndZ=0
    g6: LineSegment StartX=26 StartY=-40.315 StartZ=0 EndX=11 EndY=-40.315 EndZ=0
    g7: LineSegment StartX=11 StartY=-40.315 StartZ=0 EndX=11 EndY=39.685 EndZ=0
  constraints (22):
    c: Coincident(g0,g1)
    c: Coincident(g1,g2)
    c: Coincident(g2,g3)
    c: Coincident(g3,g0)
    c: Horizontal(g0)
    c: Horizontal(g2)
    c: Vertical(g1)
    c: Vertical(g3)
    c: Coincident(g4,g5)
    c: Coincident(g5,g6)
    c: Coincident(g6,g7)
    c: Coincident(g7,g4)
    c: Horizontal(g4)
    c: Horizontal(g6)
    c: Vertical(g5)
    c: Vertical(g7)
    c: DistanceX(g0,g4) = 22
    c: Distance(g-1,g7) = 11
    c: Distance(g5) = 80
    c: Distance(g4) = 15
    c: Distance(g0) = 15
    c: Horizontal(g0,g4)
FEATURE [Part::Extrusion] Extrude046
  Base = -> Sketch069
  Dir = (1,0,0)
  DirMode = 2
  FaceMakerClass = Part::FaceMakerBullseye
  LengthFwd = 300
  LengthRev = 0
  Solid = true
  Symmetric = true
FEATURE [Part::Cut] Cut025
  Base = -> Revolve014
  Tool = -> Extrude046
FEATURE [Sketcher::SketchObject] Sketch070
  FullyConstrained = true
  Placement = pos=(0,0,0) rot=(1,0,0;1.5708rad)
  expr: Constraints[17] = Spreadsheet007.E6
  expr: Constraints[18] = Spreadsheet007.B6 - 2 * Spreadsheet007.C6
  expr: Constraints[19] = (Spreadsheet007.B6 - 2 * Spreadsheet007.C6) / 2
  expr: Constraints[20] = Spreadsheet007.E6 / 2
  sketch-geometry (9):
    g0: LineSegment StartX=30 StartY=3 StartZ=0 EndX=30 EndY=-3 EndZ=0
    g1: LineSegment StartX=25 StartY=-8 StartZ=0 EndX=-25 EndY=-8 EndZ=0
    g2: LineSegment StartX=-30 StartY=-3 StartZ=0 EndX=-30 EndY=3 EndZ=0
    g3: LineSegment StartX=-25 StartY=8 StartZ=0 EndX=25 EndY=8 EndZ=0
    g4: GeomPoint X=0 Y=0 Z=0
    g5: ArcOfCircle CenterX=-25 CenterY=3 CenterZ=0 NormalX=0 NormalY=0 NormalZ=1 AngleXU=0 Radius=5 StartAngle=1.5708 EndAngle=3.14159
    g6: ArcOfCircle CenterX=-25 CenterY=-3 CenterZ=0 NormalX=0 NormalY=0 NormalZ=1 AngleXU=0 Radius=5 StartAngle=3.14159 EndAngle=4.71239
    g7: ArcOfCircle CenterX=25 CenterY=-3 CenterZ=0 NormalX=0 NormalY=0 NormalZ=1 AngleXU=0 Radius=5 StartAngle=4.71239 EndAngle=6.28319
    g8: ArcOfCircle CenterX=25 CenterY=3 CenterZ=0 NormalX=0 NormalY=0 NormalZ=1 AngleXU=0 Radius=5 StartAngle=-4.09e-14 EndAngle=1.5708
  constraints (21):
    c: Horizontal(g1)
    c: Horizontal(g3)
    c: Vertical(g0)
    c: Vertical(g2)
    c: Coincident(g4,g-1)
    c: Tangent(g3,g5) = 1.5708
    c: Tangent(g2,g5) = 1.5708
    c: Tangent(g1,g6) = 1.5708
    c: Tangent(g2,g6) = 1.5708
    c: Tangent(g1,g7) = 1.5708
    c: Tangent(g0,g7) = 1.5708
    c: Tangent(g0,g8) = 1.5708
    c: Tangent(g3,g8) = 1.5708
    c: Radius(g8) = 5
    c: Equal(g8,g7)
    c: Equal(g7,g6)
    c: Equal(g6,g5)
    c: DistanceY(g1,g3) = 16
    c: DistanceX(g2,g0) = 60
    c: Distance(g4,g2) = 30
    c: Distance(g4,g1) = 8
FEATURE [Part::Extrusion] Extrude047
  Base = -> Sketch070
  Dir = (0,-1,2e-16)
  DirMode = 2
  FaceMakerClass = Part::FaceMakerBullseye
  LengthFwd = 60
  LengthRev = 0
  Solid = true
  Symmetric = true
FEATURE [Part::Cut] Cut026
  Base = -> Cut025
  Tool = -> Extrude047
FEATURE [Sketcher::SketchObject] Sketch071
  FullyConstrained = true
  Placement = pos=(0,0,0) rot=(0.57735,0.57735,0.57735;2.0944rad)
  expr: Constraints[1] = Spreadsheet007.dia / 2
  sketch-geometry (1):
    g0: Circle CenterX=0 CenterY=0 CenterZ=0 NormalX=0 NormalY=0 NormalZ=1 AngleXU=0 Radius=6
  constraints (2):
    c: Coincident(g0,g-1)
    c: Radius(g0) = 6
FEATURE [Part::Extrusion] Extrude048
  Base = -> Sketch071
  Dir = (1,0,0)
  DirMode = 2
  FaceMakerClass = Part::FaceMakerBullseye
  LengthFwd = 300
  LengthRev = 0
  Solid = true
  Symmetric = true
FEATURE [Part::Cut] Cut027  label="turnBackle002"
  Base = -> Cut026
  Placement = pos=(-530,0,0) rot=(0,0,1;0rad)
  Tool = -> Extrude048
  expr: .Placement.Base.x = -(Spreadsheet007.dia * 2.5 + 500)
FEATURE [Part::Cylinder] Cylinder003  label="rod001"
  Angle = 360
  AttacherType = Attacher::AttachEngine3D
  FirstAngle = 0
  Height = 3851.28
  Placement = pos=(-536,0,-1.37e-13) rot=(0,-1,0;1.5708rad)
  Radius = 6
  SecondAngle = 0
  expr: .Placement.Base.x = -(Spreadsheet007.dia * 3 + 500)
  expr: Height = Spreadsheet007.l1
  expr: Radius = Spreadsheet007.dia / 2
FEATURE [Part::Extrusion] Extrude049  label="Extrude018"
  Base = -> Sketch067
  Dir = (0,-1,2e-16)
  DirMode = 2
  FaceMakerClass = Part::FaceMakerBullseye
  LengthFwd = 6
  LengthRev = 0
  Placement = pos=(0,9,0) rot=(0,0,1;0rad)
  Solid = true
  Symmetric = true
  expr: .Placement.Base.y = Spreadsheet007.dia / 2 + Spreadsheet007.t0 / 2
  expr: LengthFwd = Spreadsheet007.t0
FEATURE [Part::FeaturePython] Clone005  label="Extrude019"  # Draft clone (typed FeaturePython)
  AttacherType = Attacher::AttachEngine3D
  Fuse = false
  Objects = -> [Extrude049]
  Placement = pos=(-4411.28,9,0) rot=(0,1,0;3.14159rad)
  Scale = (1,1,1)
  expr: .Placement.Base.x = -Spreadsheet007.L0
  expr: .Placement.Base.y = Spreadsheet007.t0 / 2 + Spreadsheet007.dia / 2
FEATURE [Part::Compound] Compound030
  Links = -> [Cylinder002,Extrude049,Cut027,Cylinder003,Clone005]
  Placement = pos=(0,0,0) rot=(1,0,0;1.5708rad)
FEATURE [App::Part] Part020  label="Part"
  Group = -> [Extrude046,Extrude047,Clone005,Cylinder002,Revolve014,Sketch067,Sketch068,Sketch069,Cut026,Cut027,Cut025,Sketch070,Sketch071,Extrude048,Extrude049,Cylinder003,Compound030]
  Origin = -> Origin024
  Placement = pos=(0,0,0) rot=(0,0,1;4.00401rad)
  expr: .Placement.Rotation.Angle = 180 ° + Spreadsheet007.sita
FEATURE [Part::Mirroring] Mirror020  label="Part (mirrored)"
  Base = (-100,0,0)
  Normal = (0,0,1)
  Placement = pos=(0,3350,30) rot=(0,0,-1;1.72483rad)
  Source = -> Part020
  expr: .Placement.Base.y = Spreadsheet007.l0
  expr: .Placement.Base.z = Spreadsheet007.t0 * 2 + Spreadsheet007.dia + 6
  expr: .Placement.Rotation.Angle = Spreadsheet007.sita * 2
FEATURE [Sketcher::SketchObject] Sketch072
  FullyConstrained = true
  expr: Constraints[10] = Spreadsheet008.l0
  expr: Constraints[9] = Spreadsheet008.w0
  sketch-geometry (5):
    g0: LineSegment StartX=0 StartY=0 StartZ=0 EndX=2600 EndY=0 EndZ=0
    g1: LineSegment StartX=2600 StartY=0 StartZ=0 EndX=2600 EndY=3350 EndZ=0
    g2: LineSegment StartX=2600 StartY=3350 StartZ=0 EndX=0 EndY=3350 EndZ=0
    g3: LineSegment StartX=0 StartY=3350 StartZ=0 EndX=0 EndY=0 EndZ=0
    g4: LineSegment StartX=0 StartY=0 StartZ=0 EndX=2600 EndY=3350 EndZ=0
  constraints (14):
    c: Coincident(g0,g1)
    c: Coincident(g1,g2)
    c: Coincident(g2,g3)
    c: Coincident(g3,g0)
    c: Horizontal(g0)
    c: Horizontal(g2)
    c: Vertical(g1)
    c: Vertical(g3)
    c: Coincident(g0,g-1)
    c: Distance(g2) = 2600
    c: Distance(g1) = 3350
    c: Coincident(g4,g0)
    c: Coincident(g4,g1)
    c: Angle(g0,g4) = 0.910787
FEATURE [Spreadsheet::Sheet] Spreadsheet008
  cells = A2='rodDia dia; B2(dia)=12; C2='thickness; D2(t0)=6; E2='w0; F2(w0)=2600; G2='sita; H2(sita)==atan(l0 / w0); A3='length L0; B3(L0)==(w0 ^ 2 + l0 ^ 2) ^ 0.5; C3='l1; D3(l1)==L0 - (dia * 5 + 500); E3='l0; F3(l0)=3350; B4='l; C4='l1; D4='a; E4='b; F4='c; G4='e; H4='f; I4='g; J4='h; K4='i; L4='r; A5='forkEndR; B5=80; D5=25; E5=10; F5=14; G5=16; H5=13; I5=40; J5=5; K5=13; L5=15; A6='turnBackle; B6=100; C6=20; D6=30; E6=16; F6=22; A7='forkEndL; B7=60; D7=25; E7=10; F7=13; G7=16; H7=13; I7=20; L7=15; A8=1; B8=2; C8=3; D8=4; E8=5; F8=6; G8=7; H8=8; I8=9; J8=10; K8=11; L8=12; A9='turnBackle; A10='d; B10='l; C10='l1; D10='a; E10='b; F10='c; G10='t0; A11=10; B11=75; C11=15; D11=24; E11=13; F11=17; G11=6; A12=12; B12=100; C12=20; D12=30; E12=16; F12=22; G12=6; A13=16; B13=125; C13=24; D13=36; E13=20; F13=27; G13=9; A14=20; B14=150; C14=28; D14=42; E14=23; F14=33; G14=9; A15=22; B15=175; C15=33; D15=48; E15=27; F15=37; G15=9; A16=24; B16=200; C16=38; D16=54; E16=30; F16=42; G16=12; A17=30; B17=250; C17=47; D17=66; E17=37; F17=52; G17=12; A18='forkEnd_L; A19='d; B19='l; C19='a; D19='b; E19='c; F19='e; G19='f; H19='g; I19='r; A20=10; B20=50; C20=20; D20=7; E20=10; F20=12; G20=10; H20=15; I20=12; A21=12; B21=60; C21=25; D21=10; E21=13; F21=16; G21=13; H21=20; I21=15; A22=16; B22=75; C22=30; D22=13; E22=16; F22=20; G22=16; H22=25; I22=19; A23=20; B23=90; C23=40; D23=16; E23=20; F23=24; G23=20; H23=30; I23=23; A24=22; B24=100; C24=45; D24=20; E24=23; F24=28; G24=23; H24=35; I24=27; A25=24; B25=115; C25=50; D25=23; E25=26; F25=32; G25=26; H25=40; I25=30; A26=30; B26=140; C26=65; D26=30; E26=33; F26=40; G26=33; H26=50; I26=38; A27='forkEnd_R; A28='d; B28='l; C28='a; D28='b; E28='c; F28='r; +82 more cells
FEATURE [Sketcher::SketchObject] Sketch073
  FullyConstrained = true
  Placement = pos=(0,0,0) rot=(1,0,0;1.5708rad)
  expr: Constraints[11] = Spreadsheet008.I5 + Spreadsheet008.dia * 2
  expr: Constraints[1] = Spreadsheet008.F5 / 2
  expr: Constraints[3] = Spreadsheet008.L5
  sketch-geometry (5):
    g0: Circle CenterX=0 CenterY=0 CenterZ=0 NormalX=0 NormalY=0 NormalZ=1 AngleXU=0 Radius=7
    g1: ArcOfCircle CenterX=0 CenterY=0 CenterZ=0 NormalX=0 NormalY=0 NormalZ=1 AngleXU=0 Radius=15 StartAngle=4.71239 EndAngle=7.85398
    g2: LineSegment StartX=-4.87e-14 StartY=15 StartZ=0 EndX=-64 EndY=15 EndZ=0
    g3: LineSegment StartX=-64 StartY=15 StartZ=0 EndX=-64 EndY=-15 EndZ=0
    g4: LineSegment StartX=-64 StartY=-15 StartZ=0 EndX=0 EndY=-15 EndZ=0
  constraints (12):
    c: Coincident(g0,g-1)
    c: Radius(g0) = 7
    c: Coincident(g1,g0)
    c: Radius(g1) = 15
    c: Horizontal(g2)
    c: Coincident(g2,g3)
    c: Vertical(g3)
    c: Coincident(g3,g4)
    c: Horizontal(g4)
    c: Tangent(g1,g2) = -1.5708
    c: Tangent(g1,g4) = -1.5708
    c: Distance(g2) = 64
FEATURE [Part::Cylinder] Cylinder004  label="円柱002"
  Angle = 360
  AttacherType = Attacher::AttachEngine3D
  FirstAngle = 0
  Height = 500
  Placement = pos=(-24,0,0) rot=(0,-1,0;1.5708rad)
  Radius = 6
  SecondAngle = 0
  expr: .Placement.Base.x = -Spreadsheet008.dia * 2
  expr: Radius = Spreadsheet008.dia / 2
FEATURE [Sketcher::SketchObject] Sketch074
  FullyConstrained = true
  Placement = pos=(0,0,0) rot=(1,0,0;1.5708rad)
  expr: Constraints[10] = Spreadsheet008.C6
  expr: Constraints[11] = Spreadsheet008.B6
  expr: Constraints[12] = Spreadsheet008.D6 / 2
  expr: Constraints[13] = Spreadsheet008.F6 / 2
  expr: Constraints[14] = Spreadsheet008.B6 / 2
  expr: Constraints[17] = Spreadsheet008.C6
  sketch-geometry (6):
    g0: LineSegment StartX=-50 StartY=0 StartZ=0 EndX=-50 EndY=11 EndZ=0
    g1: LineSegment StartX=-50 StartY=11 StartZ=0 EndX=-30 EndY=15 EndZ=0
    g2: LineSegment StartX=-30 StartY=15 StartZ=0 EndX=30 EndY=15 EndZ=0
    g3: LineSegment StartX=30 StartY=15 StartZ=0 EndX=50 EndY=11 EndZ=0
    g4: LineSegment StartX=50 StartY=11 StartZ=0 EndX=50 EndY=0 EndZ=0
    g5: LineSegment StartX=50 StartY=0 StartZ=0 EndX=-50 EndY=0 EndZ=0
  constraints (18):
    c: PointOnObject(g0,g-1)
    c: Vertical(g0)
    c: Coincident(g0,g1)
    c: Coincident(g1,g2)
    c: Horizontal(g2)
    c: Coincident(g2,g3)
    c: Coincident(g3,g4)
    c: PointOnObject(g4,g-1)
    c: Vertical(g4)
    c: Coincident(g4,g5)
    c: DistanceX(g2,g3) = 20
    c: DistanceX(g0,g3) = 100
    c: Distance(g1,g5) = 15
    c: Distance(g4) = 11
    c: DistanceX(g-1,g4) = 50
    c: Horizontal(g0,g3)
    c: Coincident(g5,g0)
    c: DistanceX(g0,g1) = 20
FEATURE [Part::Revolution] Revolve015
  Angle = 360
  Axis = (-1,0,0)
  AxisLink = -> Sketch074 [Edge6]
  Base = (-50,0,0)
  FaceMakerClass = Part::FaceMakerBullseye
  Solid = true
  Source = -> Sketch074
  Symmetric = false
FEATURE [Sketcher::SketchObject] Sketch075
  FullyConstrained = false
  Placement = pos=(0,0,0) rot=(0.57735,0.57735,0.57735;2.0944rad)
  expr: Constraints[16] = Spreadsheet008.F6
  expr: Constraints[17] = Spreadsheet008.F6 / 2
  sketch-geometry (8):
    g0: LineSegment StartX=-11 StartY=39.685 StartZ=0 EndX=-26 EndY=39.685 EndZ=0
    g1: LineSegment StartX=-26 StartY=39.685 StartZ=0 EndX=-26 EndY=-39.3666 EndZ=0
    g2: LineSegment StartX=-26 StartY=-39.3666 StartZ=0 EndX=-11 EndY=-39.3666 EndZ=0
    g3: LineSegment StartX=-11 StartY=-39.3666 StartZ=0 EndX=-11 EndY=39.685 EndZ=0
    g4: LineSegment StartX=11 StartY=39.685 StartZ=0 EndX=26 EndY=39.685 EndZ=0
    g5: LineSegment StartX=26 StartY=39.685 StartZ=0 EndX=26 EndY=-40.315 EndZ=0
    g6: LineSegment StartX=26 StartY=-40.315 StartZ=0 EndX=11 EndY=-40.315 EndZ=0
    g7: LineSegment StartX=11 StartY=-40.315 StartZ=0 EndX=11 EndY=39.685 EndZ=0
  constraints (22):
    c: Coincident(g0,g1)
    c: Coincident(g1,g2)
    c: Coincident(g2,g3)
    c: Coincident(g3,g0)
    c: Horizontal(g0)
    c: Horizontal(g2)
    c: Vertical(g1)
    c: Vertical(g3)
    c: Coincident(g4,g5)
    c: Coincident(g5,g6)
    c: Coincident(g6,g7)
    c: Coincident(g7,g4)
    c: Horizontal(g4)
    c: Horizontal(g6)
    c: Vertical(g5)
    c: Vertical(g7)
    c: DistanceX(g0,g4) = 22
    c: Distance(g-1,g7) = 11
    c: Distance(g5) = 80
    c: Distance(g4) = 15
    c: Distance(g0) = 15
    c: Horizontal(g0,g4)
FEATURE [Part::Extrusion] Extrude050  label="Extrude020"
  Base = -> Sketch075
  Dir = (1,0,0)
  DirMode = 2
  FaceMakerClass = Part::FaceMakerBullseye
  LengthFwd = 300
  LengthRev = 0
  Solid = true
  Symmetric = true
FEATURE [Part::Cut] Cut028  label="Cut012"
  Base = -> Revolve015
  Tool = -> Extrude050
FEATURE [Sketcher::SketchObject] Sketch076
  FullyConstrained = true
  Placement = pos=(0,0,0) rot=(1,0,0;1.5708rad)
  expr: Constraints[17] = Spreadsheet008.E6
  expr: Constraints[18] = Spreadsheet008.B6 - 2 * Spreadsheet008.C6
  expr: Constraints[19] = (Spreadsheet008.B6 - 2 * Spreadsheet008.C6) / 2
  expr: Constraints[20] = Spreadsheet008.E6 / 2
  sketch-geometry (9):
    g0: LineSegment StartX=30 StartY=3 StartZ=0 EndX=30 EndY=-3 EndZ=0
    g1: LineSegment StartX=25 StartY=-8 StartZ=0 EndX=-25 EndY=-8 EndZ=0
    g2: LineSegment StartX=-30 StartY=-3 StartZ=0 EndX=-30 EndY=3 EndZ=0
    g3: LineSegment StartX=-25 StartY=8 StartZ=0 EndX=25 EndY=8 EndZ=0
    g4: GeomPoint X=0 Y=0 Z=0
    g5: ArcOfCircle CenterX=-25 CenterY=3 CenterZ=0 NormalX=0 NormalY=0 NormalZ=1 AngleXU=0 Radius=5 StartAngle=1.5708 EndAngle=3.14159
    g6: ArcOfCircle CenterX=-25 CenterY=-3 CenterZ=0 NormalX=0 NormalY=0 NormalZ=1 AngleXU=0 Radius=5 StartAngle=3.14159 EndAngle=4.71239
    g7: ArcOfCircle CenterX=25 CenterY=-3 CenterZ=0 NormalX=0 NormalY=0 NormalZ=1 AngleXU=0 Radius=5 StartAngle=4.71239 EndAngle=6.28319
    g8: ArcOfCircle CenterX=25 CenterY=3 CenterZ=0 NormalX=0 NormalY=0 NormalZ=1 AngleXU=0 Radius=5 StartAngle=-4.09e-14 EndAngle=1.5708
  constraints (21):
    c: Horizontal(g1)
    c: Horizontal(g3)
    c: Vertical(g0)
    c: Vertical(g2)
    c: Coincident(g4,g-1)
    c: Tangent(g3,g5) = 1.5708
    c: Tangent(g2,g5) = 1.5708
    c: Tangent(g1,g6) = 1.5708
    c: Tangent(g2,g6) = 1.5708
    c: Tangent(g1,g7) = 1.5708
    c: Tangent(g0,g7) = 1.5708
    c: Tangent(g0,g8) = 1.5708
    c: Tangent(g3,g8) = 1.5708
    c: Radius(g8) = 5
    c: Equal(g8,g7)
    c: Equal(g7,g6)
    c: Equal(g6,g5)
    c: DistanceY(g1,g3) = 16
    c: DistanceX(g2,g0) = 60
    c: Distance(g4,g2) = 30
    c: Distance(g4,g1) = 8
FEATURE [Part::Extrusion] Extrude051
  Base = -> Sketch076
  Dir = (0,-1,2e-16)
  DirMode = 2
  FaceMakerClass = Part::FaceMakerBullseye
  LengthFwd = 60
  LengthRev = 0
  Solid = true
  Symmetric = true
FEATURE [Part::Cut] Cut029
  Base = -> Cut028
  Tool = -> Extrude051
FEATURE [Sketcher::SketchObject] Sketch077
  FullyConstrained = true
  Placement = pos=(0,0,0) rot=(0.57735,0.57735,0.57735;2.0944rad)
  expr: Constraints[1] = Spreadsheet008.dia / 2
  sketch-geometry (1):
    g0: Circle CenterX=0 CenterY=0 CenterZ=0 NormalX=0 NormalY=0 NormalZ=1 AngleXU=0 Radius=6
  constraints (2):
    c: Coincident(g0,g-1)
    c: Radius(g0) = 6
FEATURE [Part::Extrusion] Extrude052
  Base = -> Sketch077
  Dir = (1,0,0)
  DirMode = 2
  FaceMakerClass = Part::FaceMakerBullseye
  LengthFwd = 300
  LengthRev = 0
  Solid = true
  Symmetric = true
FEATURE [Part::Cut] Cut030  label="turnBackle003"
  Base = -> Cut029
  Placement = pos=(-530,0,0) rot=(0,0,1;0rad)
  Tool = -> Extrude052
  expr: .Placement.Base.x = -(Spreadsheet008.dia * 2.5 + 500)
FEATURE [Part::Cylinder] Cylinder005  label="rod002"
  Angle = 360
  AttacherType = Attacher::AttachEngine3D
  FirstAngle = 0
  Height = 3680.58
  Placement = pos=(-536,0,-1.37e-13) rot=(0,-1,0;1.5708rad)
  Radius = 6
  SecondAngle = 0
  expr: .Placement.Base.x = -(Spreadsheet008.dia * 3 + 500)
  expr: Height = Spreadsheet008.l1
  expr: Radius = Spreadsheet008.dia / 2
FEATURE [Part::Extrusion] Extrude053
  Base = -> Sketch073
  Dir = (0,-1,2e-16)
  DirMode = 2
  FaceMakerClass = Part::FaceMakerBullseye
  LengthFwd = 6
  LengthRev = 0
  Placement = pos=(0,9,0) rot=(0,0,1;0rad)
  Solid = true
  Symmetric = true
  expr: .Placement.Base.y = Spreadsheet008.dia / 2 + Spreadsheet008.t0 / 2
  expr: LengthFwd = Spreadsheet008.t0
FEATURE [Part::FeaturePython] Clone006  label="Extrude054"  # Draft clone (typed FeaturePython)
  AttacherType = Attacher::AttachEngine3D
  Fuse = false
  Objects = -> [Extrude053]
  Placement = pos=(-4240.58,9,0) rot=(0,1,0;3.14159rad)
  Scale = (1,1,1)
  expr: .Placement.Base.x = -Spreadsheet008.L0
  expr: .Placement.Base.y = Spreadsheet008.t0 / 2 + Spreadsheet008.dia / 2
FEATURE [Part::Compound] Compound031  label="Compound009"
  Links = -> [Cylinder004,Extrude053,Cut030,Cylinder005,Clone006]
  Placement = pos=(0,0,0) rot=(1,0,0;1.5708rad)
FEATURE [App::Part] Part022  label="Part008"
  Group = -> [Extrude050,Extrude051,Clone006,Cylinder004,Revolve015,Sketch073,Sketch074,Sketch075,Cut029,Cut030,Cut028,Sketch076,Sketch077,Extrude052,Extrude053,Cylinder005,Compound031]
  Origin = -> Origin026
  Placement = pos=(0,0,0) rot=(0,0,1;4.05238rad)
  expr: .Placement.Rotation.Angle = 180 ° + Spreadsheet008.sita
FEATURE [Part::Mirroring] Mirror021  label="Part (mirrored)001"
  Base = (-100,0,0)
  Normal = (0,0,1)
  Placement = pos=(0,3350,30) rot=(0,0,-1;1.82157rad)
  Source = -> Part022
  expr: .Placement.Base.y = Spreadsheet008.l0
  expr: .Placement.Base.z = Spreadsheet008.t0 * 2 + Spreadsheet008.dia + 6
  expr: .Placement.Rotation.Angle = Spreadsheet008.sita * 2
FEATURE [Part::Compound] Compound032  label="Compound010"
  Links = -> [Mirror020,Part020]
FEATURE [App::Part] Part019  label="TurnBackleC"
  Group = -> [Spreadsheet007,Sketch066,Part020,Mirror020,Compound032]
  Origin = -> Origin023
  Placement = pos=(1768.77,-1672.49,1181.14) rot=(0,0,1;0rad)
FEATURE [Part::Compound] Compound011
  Links = -> [Mirror021,Part022]
FEATURE [App::Part] Part021  label="TurnBackleC001"
  Group = -> [Spreadsheet008,Sketch072,Part022,Mirror021,Compound011]
  Origin = -> Origin025
  Placement = pos=(4756.67,-1672.28,1180.95) rot=(0,0,1;0rad)
FEATURE [Part::FeaturePython] Flange001  # WARN: FeaturePython — macro-defined, semantics opaque (R4)
  Placement = pos=(7806.41,7.94e-13,1860) rot=(0.57735,0.57735,0.57735;2.0944rad)
  dia = 6
  fittings = 00_Flange
  material = 0
  standard = 1
FEATURE [Part::FeaturePython] Ring  # WARN: FeaturePython — macro-defined, semantics opaque (R4)
  D = 360
  Placement = pos=(0,0,0) rot=(0,1,0;1.5708rad)
  d = 315
  sface = 0
FEATURE [Part::Extrusion] Extrude054  label="Extrude055"
  Base = -> Ring
  Dir = (1,0,2e-16)
  DirMode = 2
  FaceMakerClass = Part::FaceMakerBullseye
  LengthFwd = 100
  LengthRev = 0
  Placement = pos=(7830.41,7.94e-13,1860) rot=(0,0,1;0rad)
  Reversed = true
  Solid = true
  Symmetric = false
FEATURE [App::Part] Part023  label="brg01"
  Origin = -> Origin027
  Placement = pos=(6135,-1.1983e-12,0) rot=(0,0,1;0rad)
  expr: .Placement.Base.x = Spreadsheet009.L0 - Spreadsheet009.l1
FEATURE [Part::FeaturePython] Straight_tube  # WARN: FeaturePython — macro-defined, semantics opaque (R4)
  L = 6315
  Placement = pos=(-180,0,0) rot=(0,0,1;0rad)
  dia = 16
  fittings = 05_Straight pipe
  material = 1
  standard = 1
  expr: .Placement.Base.x = -Spreadsheet009.l1
  expr: L = Spreadsheet009.L0
FEATURE [Sketcher::SketchObject] Sketch078
  FullyConstrained = true
  Placement = pos=(0,0,0) rot=(1,0,0;1.5708rad)
  expr: Constraints[35] = Spreadsheet009.L0 - (Spreadsheet009.l1 + 100)
  sketch-geometry (12):
    g0: LineSegment StartX=6015 StartY=159.25 StartZ=0 EndX=6035 EndY=159.25 EndZ=0
    g1: LineSegment StartX=6035 StartY=159.25 StartZ=0 EndX=6035 EndY=164.25 EndZ=0
    g2: LineSegment StartX=6035 StartY=164.25 StartZ=0 EndX=6015 EndY=164.25 EndZ=0
    g3: LineSegment StartX=6015 StartY=164.25 StartZ=0 EndX=6015 EndY=159.25 EndZ=0
    g4: LineSegment StartX=0 StartY=159.25 StartZ=0 EndX=0 EndY=169.25 EndZ=0
    g5: LineSegment StartX=0 StartY=169.25 StartZ=0 EndX=19 EndY=169.25 EndZ=0
    g6: LineSegment StartX=19 StartY=169.25 StartZ=0 EndX=19 EndY=164.25 EndZ=0
    g7: LineSegment StartX=19 StartY=164.25 StartZ=0 EndX=31 EndY=164.25 EndZ=0
    g8: LineSegment StartX=31 StartY=164.25 StartZ=0 EndX=31 EndY=169.25 EndZ=0
    g9: LineSegment StartX=31 StartY=169.25 StartZ=0 EndX=50 EndY=169.25 EndZ=0
    g10: LineSegment StartX=50 StartY=169.25 StartZ=0 EndX=50 EndY=159.25 EndZ=0
    g11: LineSegment StartX=50 StartY=159.25 StartZ=0 EndX=0 EndY=159.25 EndZ=0
  constraints (36):
    c: Coincident(g0,g1)
    c: Coincident(g1,g2)
    c: Coincident(g2,g3)
    c: Coincident(g3,g0)
    c: Horizontal(g0)
    c: Horizontal(g2)
    c: Vertical(g1)
    c: Vertical(g3)
    c: DistanceY(g-1,g0) = 159.25
    c: DistanceY(g1,g1) = 5
    c: DistanceX(g2,g2) = 20
    c: Vertical(g4)
    c: Coincident(g4,g5)
    c: Horizontal(g5)
    c: Coincident(g5,g6)
    c: Vertical(g6)
    c: Coincident(g6,g7)
    c: Coincident(g7,g8)
    c: Coincident(g8,g9)
    c: Coincident(g9,g10)
    c: Coincident(g10,g11)
    c: Coincident(g11,g4)
    c: Horizontal(g11)
    c: Vertical(g10)
    c: Horizontal(g7)
    c: Horizontal(g9)
    c: Vertical(g8)
    c: DistanceY(g10,g10) = 10
    c: DistanceY(g7,g8) = 5
    c: Horizontal(g8,g5)
    c: DistanceX(g11,g11) = 50
    c: DistanceX(g7,g7) = 12
    c: DistanceX(g5,g5) = 19
    c: DistanceY(g-1,g4) = 159.25
    c: Vertical(g-1,g4)
    c: DistanceX(g-1,g0) = 6035
FEATURE [Part::Revolution] Revolve016  label="Revolve005"
  Angle = 360
  Axis = (1,0,0)
  Base = (0,0,0)
  FaceMakerClass = Part::FaceMakerBullseye
  Solid = true
  Source = -> Sketch078
  Symmetric = false
FEATURE [Spreadsheet::Sheet] Spreadsheet009  label="Spreadsheet_pipeSkimmer"
  cells = A2='tankDia  D0; B2(D0)=15500; A3='fullLength L0; B3(L0)=6315; A4='length       l1; B4(l1)=180; A5='n0; B5(n0)=5; A6='l3; B6(l3)=1134; A7='開閉台  h2; B7(h2)=1500
FEATURE [Sketcher::SketchObject] Sketch079
  FullyConstrained = false
  Placement = pos=(0,0,0) rot=(0.57735,0.57735,0.57735;2.0944rad)
  sketch-geometry (3):
    g0: LineSegment StartX=0 StartY=0 StartZ=0 EndX=114.659 EndY=220.257 EndZ=0
    g1: LineSegment StartX=0 StartY=0 StartZ=0 EndX=-114.659 EndY=220.257 EndZ=0
    g2: ArcOfCircle CenterX=0 CenterY=0 CenterZ=0 NormalX=0 NormalY=0 NormalZ=1 AngleXU=0 Radius=248.314 StartAngle=1.09083 EndAngle=2.05076
  constraints (7):
    c: Coincident(g-1,g0)
    c: Coincident(g1,g0)
    c: Coincident(g2,g0)
    c: Coincident(g2,g1)
    c: Coincident(g2,g0)
    c: Angle(g0,g-2) = 0.479966
    c: Angle(g0,g1) = 0.959931
FEATURE [Part::Extrusion] Extrude055  label="Extrude056"
  Base = -> Sketch079
  Dir = (1,0,0)
  DirMode = 2
  FaceMakerClass = Part::FaceMakerBullseye
  LengthFwd = 1100
  LengthRev = 0
  Placement = pos=(100,0,0) rot=(0,0,1;0rad)
  Solid = true
  Symmetric = false
FEATURE [Part::FeaturePython] Array026  # Draft array (typed FeaturePython)
  AlwaysSyncPlacement = false
  Angle = 360
  ArrayType = 0
  Axis = (0,0,1)
  Base = -> Extrude055
  Center = (0,0,0)
  Count = 5
  ExpandArray = false
  Fuse = false
  IntervalAxis = (0,0,0)
  IntervalX = (1200,0,0)
  IntervalY = (0,100,0)
  IntervalZ = (0,0,100)
  NumberCircles = 3
  NumberPolar = 5
  NumberX = 5
  NumberY = 1
  NumberZ = 1
  PlacementList = 5 placements: arithmetic series from (100,0,0) step (1200,0,0) to (4900,0,0)
  RadialDistance = 50
  ScaleList = (5) [(1,1,1),(1,1,1),(1,1,1),(1,1,1),(1,1,1)]
  Symmetry = 1
  TangentialDistance = 25
  expr: NumberX = Spreadsheet009.n0
FEATURE [Part::Cut] Cut031  label="Cut015"
  Base = -> Straight_tube
  Tool = -> Array026
FEATURE [Sketcher::SketchObject] Sketch080
  FullyConstrained = false
  Placement = pos=(0,0,0) rot=(0.57735,0.57735,0.57735;2.0944rad)
  sketch-geometry (3):
    g0: LineSegment StartX=0 StartY=0 StartZ=0 EndX=-124.513 EndY=239.188 EndZ=0
    g1: LineSegment StartX=0 StartY=0 StartZ=0 EndX=124.513 EndY=239.188 EndZ=0
    g2: ArcOfCircle CenterX=0 CenterY=0 CenterZ=0 NormalX=0 NormalY=0 NormalZ=1 AngleXU=0 Radius=269.656 StartAngle=1.09083 EndAngle=2.05076
  constraints (7):
    c: Coincident(g0,g-1)
    c: Coincident(g1,g0)
    c: Coincident(g2,g1)
    c: Coincident(g2,g0)
    c: Coincident(g2,g0)
    c: Angle(g1,g0) = 0.959931
    c: Angle(g1,g-2) = 0.479966
FEATURE [Part::Extrusion] Extrude056  label="Extrude057"
  Base = -> Sketch080
  Dir = (1,0,0)
  DirMode = 2
  FaceMakerClass = Part::FaceMakerBullseye
  LengthFwd = 130
  LengthRev = 0
  Placement = pos=(-25,0,0) rot=(0,0,1;0rad)
  Reversed = true
  Solid = true
  Symmetric = false
  expr: LengthFwd = Spreadsheet009.l1 - 50
FEATURE [Part::Cut] Cut032
  Base = -> Cut031
  Tool = -> Extrude056
FEATURE [Sketcher::SketchObject] Sketch081
  FullyConstrained = true
  Placement = pos=(0,0,0) rot=(0.57735,0.57735,0.57735;2.0944rad)
  sketch-geometry (6):
    g0: LineSegment StartX=0 StartY=0 StartZ=0 EndX=247.487 EndY=247.487 EndZ=0
    g1: Circle CenterX=247.487 CenterY=247.487 CenterZ=0 NormalX=0 NormalY=0 NormalZ=1 AngleXU=0 Radius=7.5
    g2: ArcOfCircle CenterX=247.487 CenterY=247.487 CenterZ=0 NormalX=0 NormalY=0 NormalZ=1 AngleXU=0 Radius=20 StartAngle=5.62869 EndAngle=8.50848
    g3: LineSegment StartX=235.312 StartY=263.354 StartZ=0 EndX=74.8903 EndY=140.258 EndZ=0
    g4: LineSegment StartX=263.354 StartY=235.312 StartZ=0 EndX=140.258 EndY=74.8903 EndZ=0
    g5: ArcOfCircle CenterX=0 CenterY=0 CenterZ=0 NormalX=0 NormalY=0 NormalZ=1 AngleXU=0 Radius=159 StartAngle=0.490434 EndAngle=1.08036
  constraints (15):
    c: Coincident(g0,g-1)
    c: Angle(g-1,g0) = 0.785398
    c: Coincident(g1,g0)
    c: Radius(g1) = 7.5
    c: Coincident(g2,g1)
    c: Coincident(g5,g3)
    c: Coincident(g5,g4)
    c: Coincident(g5,g0)
    c: Tangent(g2,g3) = -1.5708
    c: Tangent(g2,g4) = 1.5708
    c: Equal(g4,g3)
    c: Radius(g5) = 159
    c: Angle(g3,g4) = 0.261799
    c: Distance(g5,g1) = 350
    c: Radius(g2) = 20
FEATURE [Part::Extrusion] Extrude057  label="Extrude058"
  Base = -> Sketch081
  Dir = (1,0,0)
  DirMode = 2
  FaceMakerClass = Part::FaceMakerBullseye
  LengthFwd = 6
  LengthRev = 0
  Placement = pos=(-217,0,0) rot=(0,0,1;0rad)
  Solid = true
  Symmetric = true
FEATURE [App::Part] Part026  label="arm"
  Group = -> [Sketch081,Extrude057]
  Origin = -> Origin030
  Placement = pos=(5815,0,0) rot=(1,0,0;1.8326rad)
  expr: .Placement.Base.x = Spreadsheet009.L0 - 500
FEATURE [Sketcher::SketchObject] Sketch082
  ExternalGeometry = -> [Cut032]
  FullyConstrained = true
  MapMode = 5
  Placement = pos=(-180,0,0) rot=(0.57735,-0.57735,-0.57735;2.0944rad)
  Support = -> [Cut032]
  sketch-geometry (1):
    g0: Circle CenterX=0 CenterY=0 CenterZ=0 NormalX=0 NormalY=0 NormalZ=1 AngleXU=0 Radius=159.25
  constraints (2):
    c: Coincident(g0,g-1)
    c: Equal(g0,g-3)
FEATURE [Part::Extrusion] Extrude058  label="Extrude059"
  Base = -> Sketch082
  Dir = (-1,0,0)
  DirMode = 2
  FaceMakerClass = Part::FaceMakerBullseye
  LengthFwd = 6
  LengthRev = 0
  Solid = true
  Symmetric = false
FEATURE [App::Part] Part024  label="pipe"
  Group = -> [Sketch078,Revolve016,Cut031,Cut032,Sketch080,Sketch079,Straight_tube,Array026,Extrude056,Extrude055,Sketch082,Extrude058,Part026]
  Origin = -> Origin028
  Placement = pos=(1510.97,0,1853.54) rot=(0,0,1;0rad)
FEATURE [Part::Feature] Part__Feature010  label="電動トップハンドル_LTKD-01 v5"
  Placement = pos=(0,-389.711,-5.7e-14) rot=(1,0,0;1.5708rad)
  shape: bbox 555.2 x 557.2 x 1150 mm, 73 faces (baked)
FEATURE [App::Part] Part027  label="開閉台"
  Group = -> [Part__Feature010]
  Origin = -> Origin031
  Placement = pos=(0,-400,1500) rot=(0,0,1;3.14159rad)
FEATURE [Sketcher::SketchObject] Sketch083
  FullyConstrained = false
  Placement = pos=(0,0,0) rot=(0.57735,0.57735,0.57735;2.0944rad)
  sketch-geometry (5):
    g0: Circle CenterX=0 CenterY=0 CenterZ=0 NormalX=0 NormalY=0 NormalZ=1 AngleXU=0 Radius=7.5
    g1: ArcOfCircle CenterX=0 CenterY=0 CenterZ=0 NormalX=0 NormalY=0 NormalZ=1 AngleXU=0 Radius=20 StartAngle=3.14159 EndAngle=6.28319
    g2: LineSegment StartX=-20 StartY=9.32106e-06 StartZ=0 EndX=-20 EndY=80 EndZ=0
    g3: LineSegment StartX=-20 StartY=80 StartZ=0 EndX=20 EndY=80 EndZ=0
    g4: LineSegment StartX=20 StartY=80 StartZ=0 EndX=20 EndY=3.56439e-05 EndZ=0
  constraints (13):
    c: Coincident(g0,g-1)
    c: Coincident(g1,g0)
    c: Radius(g1) = 20
    c: Radius(g0) = 7.5
    c: Vertical(g2)
    c: Coincident(g2,g3)
    c: Horizontal(g3)
    c: Coincident(g3,g4)
    c: Vertical(g4)
    c: Coincident(g1,g4)
    c: Coincident(g1,g2)
    c: DistanceY(g-1,g3) = 80
    c: DistanceX(g3,g3) = 40
FEATURE [Part::Extrusion] Extrude059  label="Extrude060"
  Base = -> Sketch083
  Dir = (1,0,0)
  DirMode = 2
  FaceMakerClass = Part::FaceMakerBullseye
  LengthFwd = 40
  LengthRev = 0
  Solid = true
  Symmetric = true
FEATURE [Sketcher::SketchObject] Sketch084
  ExternalGeometry = -> [Extrude059]
  FullyConstrained = false
  MapMode = 5
  Placement = pos=(0,-20,0) rot=(1,0,0;1.5708rad)
  Support = -> [Extrude059]
  sketch-geometry (4):
    g0: LineSegment StartX=-5 StartY=-25.0355 StartZ=0 EndX=5 EndY=-25.0355 EndZ=0
    g1: LineSegment StartX=5 StartY=-25.0355 StartZ=0 EndX=5 EndY=60 EndZ=0
    g2: LineSegment StartX=5 StartY=60 StartZ=0 EndX=-5 EndY=60 EndZ=0
    g3: LineSegment StartX=-5 StartY=60 StartZ=0 EndX=-5 EndY=-25.0355 EndZ=0
  constraints (11):
    c: Coincident(g0,g1)
    c: Coincident(g1,g2)
    c: Coincident(g2,g3)
    c: Coincident(g3,g0)
    c: Horizontal(g0)
    c: Horizontal(g2)
    c: Vertical(g1)
    c: Vertical(g3)
    c: Distance(g1,g-3) = 20
    c: DistanceX(g0,g0) = 10
    c: DistanceX(g0,g-1) = 5
FEATURE [Part::Extrusion] Extrude060  label="Extrude061"
  Base = -> Sketch084
  Dir = (0,-1,2e-16)
  DirMode = 2
  FaceMakerClass = Part::FaceMakerBullseye
  LengthFwd = 50
  LengthRev = 0
  Reversed = true
  Solid = true
  Symmetric = false
FEATURE [Part::Cut] Cut033
  Base = -> Extrude059
  Tool = -> Extrude060
FEATURE [Sketcher::SketchObject] Sketch085
  FullyConstrained = true
  MapMode = 5
  Placement = pos=(0,0,80) rot=(0,0,1;0rad)
  Support = -> [Cut033]
  sketch-geometry (1):
    g0: Circle CenterX=0 CenterY=0 CenterZ=0 NormalX=0 NormalY=0 NormalZ=1 AngleXU=0 Radius=15
  constraints (2):
    c: Coincident(g0,g-1)
    c: Radius(g0) = 15
FEATURE [Part::Extrusion] Extrude061  label="Extrude062"
  Base = -> Sketch085
  Dir = (0,0,1)
  DirMode = 2
  FaceMakerClass = Part::FaceMakerBullseye
  LengthFwd = 300
  LengthRev = 0
  Solid = true
  Symmetric = false
FEATURE [Part::FeaturePython] Clone007  label="Cut018"  # Draft clone (typed FeaturePython)
  AttacherType = Attacher::AttachEngine3D
  Fuse = false
  Objects = -> [Cut033]
  Placement = pos=(-1.83e-13,0,458.657) rot=(0,1,0;3.14159rad)
  Scale = (1,1,1)
FEATURE [App::Part] Part028  label="rod003"
  Group = -> [Cut033,Clone007,Sketch084,Sketch083,Sketch085,Extrude059,Extrude060,Extrude061]
  Origin = -> Origin032
  Placement = pos=(7112.9,-302.975,2028.5) rot=(0,0,1;0rad)
FEATURE [Sketcher::SketchObject] Sketch086
  FullyConstrained = false
  Placement = pos=(0,0,0) rot=(0.57735,0.57735,0.57735;2.0944rad)
  sketch-geometry (5):
    g0: Circle CenterX=0 CenterY=0 CenterZ=0 NormalX=0 NormalY=0 NormalZ=1 AngleXU=0 Radius=7.5
    g1: ArcOfCircle CenterX=0 CenterY=0 CenterZ=0 NormalX=0 NormalY=0 NormalZ=1 AngleXU=0 Radius=20 StartAngle=3.14864 EndAngle=6.2925
    g2: LineSegment StartX=-19.9995 StartY=-0.141043 StartZ=0 EndX=-19.9995 EndY=80 EndZ=0
    g3: LineSegment StartX=-19.9995 StartY=80 StartZ=0 EndX=19.9991 EndY=80 EndZ=0
    g4: LineSegment StartX=19.9991 StartY=80 StartZ=0 EndX=19.9991 EndY=0.186233 EndZ=0
  constraints (12):
    c: Coincident(g0,g-1)
    c: Coincident(g1,g0)
    c: Vertical(g2)
    c: Coincident(g2,g3)
    c: Horizontal(g3)
    c: Coincident(g3,g4)
    c: Vertical(g4)
    c: Coincident(g1,g4)
    c: Coincident(g1,g2)
    c: Radius(g0) = 7.5
    c: Radius(g1) = 20
    c: DistanceY(g-1,g3) = 80
FEATURE [Part::Extrusion] Extrude062  label="Extrude063"
  Base = -> Sketch086
  Dir = (1,0,0)
  DirMode = 2
  FaceMakerClass = Part::FaceMakerBullseye
  LengthFwd = 9
  LengthRev = 0
  Solid = true
  Symmetric = true
FEATURE [Part::Cylinder] Cylinder006  label="円柱003"
  Angle = 360
  AttacherType = Attacher::AttachEngine3D
  FirstAngle = 0
  Height = 1000
  Placement = pos=(0,0,30) rot=(0,0,1;0rad)
  Radius = 15
  SecondAngle = 0
FEATURE [App::Part] Part029  label="rod004"
  Group = -> [Sketch086,Cylinder006,Extrude062]
  Origin = -> Origin033
FEATURE [Part::Compound] Compound033  label="rod005"
  Links = -> [Part029]
  Placement = pos=(7510,-330.291,2884.57) rot=(0.999848,0.015695,0.007617;2e-06rad)
FEATURE [Part::Compound] Compound034  label="開閉台001"
  Links = -> [Part027]
  Placement = pos=(7500.5,-320.001,1610.35) rot=(0.999847,0.015695,0;2e-06rad)
FEATURE [App::FeaturePython] axisCoincident_001_mirror001  label="axisCoincident_001__Compound014"  # a2plus constraint (typed FeaturePython)
  Object1 = Compound014
  Object2 = Compound012
  SubElement1 = Edge18
  SubElement2 = Edge786
  Suppressed = false
  Type = axial
  directionConstraint = 1
  lockRotation = false
FEATURE [App::FeaturePython] circularEdge_005  label="circularEdge_002__pipe001"  # a2plus constraint (typed FeaturePython)
  Object1 = Extrude023
  Object2 = Compound012
  ParentTreeObject = -> Extrude023
  SubElement1 = Edge3
  SubElement2 = Edge16
  Suppressed = false
  Type = circularEdge
  directionConstraint = 1
  lockRotation = false
  offset = 0
FEATURE [App::FeaturePython] circularEdge_002_mirror001  label="circularEdge_002__Extrude025"  # a2plus constraint (typed FeaturePython)
  Object1 = Extrude023
  Object2 = Compound012
  SubElement1 = Edge3
  SubElement2 = Edge16
  Suppressed = false
  Type = circularEdge
  directionConstraint = 0
  lockRotation = false
  offset = 0
FEATURE [App::FeaturePython] circularEdge_006  label="circularEdge_003__Extrude025"  # a2plus constraint (typed FeaturePython)
  Object1 = Flange
  Object2 = Extrude023
  ParentTreeObject = -> Flange
  SubElement1 = Edge29
  SubElement2 = Edge2
  Suppressed = false
  Type = circularEdge
  directionConstraint = 1
  lockRotation = false
  offset = 0
FEATURE [App::FeaturePython] circularEdge_003_mirror001  label="circularEdge_003__Flange"  # a2plus constraint (typed FeaturePython)
  Object1 = Flange
  Object2 = Extrude023
  ParentTreeObject = -> Extrude023
  SubElement1 = Edge29
  SubElement2 = Edge2
  Suppressed = false
  Type = circularEdge
  directionConstraint = 0
  lockRotation = false
  offset = 0
FEATURE [App::Part] Part025  label="pipeSkimmer"
  Group = -> [Part023,Spreadsheet009,circularEdge_003_mirror001,circularEdge_005,circularEdge_006]
  Origin = -> Origin029
  Placement = pos=(4.415,0,0) rot=(0,0,1;0rad)
FEATURE [App::FeaturePython] circularEdge_007  label="circularEdge_004__Compound014"  # a2plus constraint (typed FeaturePython)
  Object1 = Compound013
  Object2 = Compound014
  ParentTreeObject = -> Compound013
  SubElement1 = Edge18
  SubElement2 = Edge56
  Suppressed = false
  Type = circularEdge
  directionConstraint = 0
  lockRotation = false
  offset = 0
FEATURE [App::FeaturePython] circularEdge_004_mirror001  label="circularEdge_004__rod004"  # a2plus constraint (typed FeaturePython)
  Object1 = Compound013
  Object2 = Compound014
  ParentTreeObject = -> Compound014
  SubElement1 = Edge18
  SubElement2 = Edge56
  Suppressed = false
  Type = circularEdge
  directionConstraint = 0
  lockRotation = false
  offset = 0
FEATURE [App::FeaturePython] axisCoincident_002_mirror001  label="axisCoincident_002__開閉台001"  # a2plus constraint (typed FeaturePython)
  Object1 = Compound003
  Object2 = Compound013
  ParentTreeObject = -> Compound013
  SubElement1 = Face69
  SubElement2 = Face1
  Suppressed = false
  Type = axial
  directionConstraint = 0
  lockRotation = false
FEATURE [Part::Compound] Compound036
  Links = -> [Flange001,Extrude054]
  Placement = pos=(-184.66,0,0) rot=(0,0,1;0rad)
FEATURE [Part::Compound] Compound037
  Links = -> [Compound033,Compound034]
  Placement = pos=(-400.78,27,-397.2) rot=(0,0,1;0rad)
FEATURE [Part::FeaturePython] Single_flange_straight_pipe  # WARN: FeaturePython — macro-defined, semantics opaque (R4)
  L = 500
  Placement = pos=(7647.67,0.5,4835) rot=(0,0,1;0rad)
  dia = 15
  fittings = 06_Single_flange_straight_pipe
  material = 0
  standard = 0
  standard2 = 1
FEATURE [Sketcher::SketchObject] Sketch087
  FullyConstrained = true
  sketch-geometry (5):
    g0: LineSegment StartX=-680 StartY=-750 StartZ=0 EndX=-680 EndY=750 EndZ=0
    g1: LineSegment StartX=-680 StartY=750 StartZ=0 EndX=680 EndY=750 EndZ=0
    g2: LineSegment StartX=680 StartY=750 StartZ=0 EndX=680 EndY=-750 EndZ=0
    g3: LineSegment StartX=680 StartY=-750 StartZ=0 EndX=-680 EndY=-750 EndZ=0
    g4: GeomPoint X=0 Y=0 Z=0
  constraints (12):
    c: Coincident(g0,g1)
    c: Coincident(g1,g2)
    c: Coincident(g2,g3)
    c: Coincident(g3,g0)
    c: Horizontal(g1)
    c: Horizontal(g3)
    c: Vertical(g0)
    c: Vertical(g2)
    c: Symmetric(g1,g0,g4)
    c: Coincident(g4,g-1)
    c: DistanceY(g2,g2) = 1500
    c: DistanceX(g1,g1) = 1360
FEATURE [Part::FeaturePython] HShapeSteel  # WARN: FeaturePython — macro-defined, semantics opaque (R4)
  B = 150
  H = 150
  L = 1000
  Placement = pos=(530,0,-150) rot=(0,0,1;0rad)
  Solid = false
  g0 = 7.85
  mass = 0
  size = 2
  standard = SS_Wide
  t1 = 7
  t2 = 10
FEATURE [Part::Sweep] Sweep003
  Frenet = true
  Sections = -> [HShapeSteel]
  Solid = true
  Spine = -> Sketch087 [Edge3,Edge2,Edge1,Edge4]
  Transition = 1
FEATURE [Part::FeaturePython] HShapeSteel001  # WARN: FeaturePython — macro-defined, semantics opaque (R4)
  B = 150
  H = 150
  L = 1000
  Placement = pos=(607.98,425,-75) rot=(0.57735,0.57735,0.57735;2.0944rad)
  Solid = true
  g0 = 7.85
  mass = 31.5089
  size = 2
  standard = SS_Wide
  t1 = 7
  t2 = 10
FEATURE [Part::FeaturePython] Clone008  label="HShapeSteel002"  # Draft clone (typed FeaturePython)
  AttacherType = Attacher::AttachEngine3D
  Fuse = false
  Objects = -> [HShapeSteel001]
  Placement = pos=(607.98,-425,-75) rot=(0.57735,0.57735,0.57735;2.0944rad)
  Scale = (1,1,1)
FEATURE [Part::FeaturePython] HShapeSteel002  label="HShapeSteel003"  # WARN: FeaturePython — macro-defined, semantics opaque (R4)
  B = 150
  H = 150
  L = 1000
  Placement = pos=(1607.98,-500,-150) rot=(0,0,1;1.5708rad)
  Solid = false
  g0 = 7.85
  mass = 0
  size = 2
  standard = SS_Wide
  t1 = 7
  t2 = 10
FEATURE [Part::FeaturePython] HShapeSteel003  label="HShapeSteel004"  # WARN: FeaturePython — macro-defined, semantics opaque (R4)
  B = 150
  H = 194
  L = 1000
  Placement = pos=(1900,-500,-194) rot=(0,0,1;1.5708rad)
  Solid = false
  g0 = 7.85
  mass = 0
  size = 1
  standard = SS_Medium
  t1 = 6
  t2 = 9
FEATURE [Part::Loft] Loft
  Closed = false
  MaxDegree = 5
  Ruled = false
  Sections = -> [HShapeSteel002,HShapeSteel003]
  Solid = true
FEATURE [Part::Extrusion] Extrude063  label="Extrude064"
  Base = -> HShapeSteel003
  Dir = (-1,-2e-16,0)
  DirMode = 2
  FaceMakerClass = Part::FaceMakerBullseye
  LengthFwd = 6250
  LengthRev = 0
  Reversed = true
  Solid = true
  Symmetric = false
  expr: LengthFwd = Spreadsheet010.L0
FEATURE [Part::MultiFuse] Fusion004
  Shapes = -> [HShapeSteel001,Clone008]
FEATURE [Part::MultiFuse] Fusion005  label="Fusion002"
  Shapes = -> [Extrude063,Loft]
FEATURE [Part::FeaturePython] Clone009  label="Fusion003"  # Draft clone (typed FeaturePython)
  AttacherType = Attacher::AttachEngine3D
  Fuse = false
  Objects = -> [Fusion005]
  Placement = pos=(-9.09e-13,850,6.6e-14) rot=(0,0,1;0rad)
  Scale = (1,1,1)
FEATURE [Part::Mirroring] Mirror024  label="Fusion (mirrored)001"
  Base = (0,0,0)
  Normal = (1,0,0)
  Source = -> Fusion004
FEATURE [Part::MultiFuse] Fusion006
  Refine = true
  Shapes = -> [Sweep003,Fusion004,Mirror024]
FEATURE [Spreadsheet::Sheet] Spreadsheet010
  cells = A2='tankdia   dia; B2(dia)=15500; A3='L0; B3(L0)==dia / 2 + 400 - 1900; A4='n; B4(n)==L0 / 700
FEATURE [Sketcher::SketchObject] Sketch088
  ExternalGeometry = -> [Fusion006]
  FullyConstrained = true
  sketch-geometry (4):
    g0: LineSegment StartX=-1150 StartY=-1150 StartZ=0 EndX=-1150 EndY=1150 EndZ=0
    g1: LineSegment StartX=-1150 StartY=1150 StartZ=0 EndX=1150 EndY=1150 EndZ=0
    g2: LineSegment StartX=1150 StartY=1150 StartZ=0 EndX=1150 EndY=-1150 EndZ=0
    g3: LineSegment StartX=-1150 StartY=-1150 StartZ=0 EndX=1150 EndY=-1150 EndZ=0
  constraints (12):
    c: Vertical(g0)
    c: Coincident(g0,g1)
    c: Horizontal(g1)
    c: Coincident(g1,g2)
    c: Vertical(g2)
    c: DistanceX(g1,g1) = 2300
    c: DistanceX(g-2,g1) = 1150
    c: Coincident(g3,g0)
    c: Coincident(g3,g2)
    c: Horizontal(g3)
    c: DistanceY(g2,g2) = 2300
    c: DistanceY(g-1,g1) = 1150
FEATURE [Part::FeaturePython] ChannelSteel005  # WARN: FeaturePython — macro-defined, semantics opaque (R4)
  B = 75
  H = 150
  L = 1000
  Placement = pos=(-1150,855.871,-150) rot=(0,0,1;0rad)
  Solid = false
  g0 = 7.85
  mass = 0
  size = 3
  standard = SS
  t1 = 6.5
  t2 = 10
FEATURE [Part::Sweep] Sweep004
  Frenet = true
  Sections = -> [ChannelSteel005]
  Solid = true
  Spine = -> Sketch088 [Edge2,Edge3,Edge4,Edge1]
  Transition = 1
FEATURE [Part::MultiFuse] Fusion007  label="Fusion005"
  Refine = true
  Shapes = -> [Fusion006,Sweep004]
FEATURE [Part::FeaturePython] AngleSteel018  label="AngleSteel020"  # WARN: FeaturePython — macro-defined, semantics opaque (R4)
  A = 75
  B = 75
  L = 700
  Placement = pos=(1800,350,-37.5) rot=(1,0,0;1.5708rad)
  Solid = true
  g0 = 7.85
  mass = 4.79514
  size = 10
  standard = SS_Equal
  t = 6
FEATURE [Part::FeaturePython] Array027  # Draft array (typed FeaturePython)
  AlwaysSyncPlacement = false
  Angle = 360
  ArrayType = 0
  Axis = (0,0,1)
  Base = -> AngleSteel018
  Center = (0,0,0)
  Count = 9
  ExpandArray = false
  Fuse = false
  IntervalAxis = (0,0,0)
  IntervalX = (700,0,0)
  IntervalY = (0,100,0)
  IntervalZ = (0,0,100)
  NumberCircles = 3
  NumberPolar = 5
  NumberX = 9
  NumberY = 1
  NumberZ = 1
  PlacementList = 9 placements: arithmetic series from (1800,350,-37.5) step (700,0,0) to (7400,350,-37.5)
  RadialDistance = 50
  ScaleList = (9) [(1,1,1),(1,1,1),(1,1,1),(1,1,1),(1,1,1),(1,1,1),(1,1,1),(1,1,1),(1,1,1)]
  Symmetry = 1
  TangentialDistance = 25
  expr: NumberX = Spreadsheet010.n
FEATURE [Part::Compound] Compound038
  Links = -> [Fusion005,Clone009]
FEATURE [Part::Compound] Compound039  label="Compound001"
  Links = -> [Compound038,Array027]
FEATURE [Part::FeaturePython] AngleSteel019  label="AngleSteel021"  # WARN: FeaturePython — macro-defined, semantics opaque (R4)
  A = 75
  B = 75
  L = 325
  Placement = pos=(-642.5,-750,-37.5) rot=(1,0,0;1.5708rad)
  Solid = true
  g0 = 7.85
  mass = 2.22632
  size = 10
  standard = SS_Equal
  t = 6
FEATURE [Part::Mirroring] Mirror025  label="AngleSteel001 (mirrored)001"
  Base = (0,0,0)
  Normal = (-1,0,0)
  Source = -> AngleSteel019
FEATURE [Part::Mirroring] Mirror002  label="AngleSteel001 (mirrored)002"
  Base = (0,0,0)
  Normal = (0,1,0)
  Source = -> AngleSteel019
FEATURE [Part::Mirroring] Mirror003  label="AngleSteel001 (mirrored) (mirrored)"
  Base = (0,0,0)
  Normal = (0,1,0)
  Source = -> Mirror025
FEATURE [Part::FeaturePython] HShapeSteel004  label="HShapeSteel005"  # WARN: FeaturePython — macro-defined, semantics opaque (R4)
  B = 150
  H = 194
  L = 850
  Placement = pos=(8075,425,-97) rot=(1,0,0;1.5708rad)
  Solid = true
  g0 = 7.85
  mass = 26.0299
  size = 1
  standard = SS_Medium
  t1 = 6
  t2 = 9
FEATURE [Part::MultiFuse] Fusion008
  Shapes = -> [Compound039]
FEATURE [Part::MultiFuse] Fusion009  label="Fusion007"
  Refine = true
  Shapes = -> [Fusion008,HShapeSteel004]
FEATURE [Part::Mirroring] Mirror026  label="Fusion007 (mirrored)"
  Base = (0,-500,0)
  Normal = (1,0,0)
  Source = -> Fusion009
FEATURE [Sketcher::SketchObject] Sketch089
  ExternalGeometry = -> [Sketch088,Fusion009,Fusion007]
  FullyConstrained = true
  MapMode = 5
  Placement = pos=(0,0,1.92e-13) rot=(0,0,1;0rad)
  Support = -> [Mirror026]
  sketch-geometry (12):
    g0: LineSegment StartX=0 StartY=1150 StartZ=0 EndX=1150 EndY=1150 EndZ=0
    g1: LineSegment StartX=1150 StartY=1150 StartZ=0 EndX=1150 EndY=500 EndZ=0
    g2: LineSegment StartX=1150 StartY=500 StartZ=0 EndX=8150 EndY=500 EndZ=0
    g3: LineSegment StartX=8150 StartY=500 StartZ=0 EndX=8150 EndY=-500 EndZ=0
    g4: LineSegment StartX=8150 StartY=-500 StartZ=0 EndX=1150 EndY=-500 EndZ=0
    g5: LineSegment StartX=1150 StartY=-500 StartZ=0 EndX=1150 EndY=-1150 EndZ=0
    g6: LineSegment StartX=1150 StartY=-1150 StartZ=0 EndX=0 EndY=-1150 EndZ=0
    g7: LineSegment StartX=0 StartY=-1150 StartZ=0 EndX=0 EndY=-675 EndZ=0
    g8: LineSegment StartX=0 StartY=675 StartZ=0 EndX=605 EndY=675 EndZ=0
    g9: LineSegment StartX=605 StartY=675 StartZ=0 EndX=605 EndY=-675 EndZ=0
    g10: LineSegment StartX=605 StartY=-675 StartZ=0 EndX=0 EndY=-675 EndZ=0
    g11: LineSegment StartX=0 StartY=675 StartZ=0 EndX=0 EndY=1150 EndZ=0
  constraints (32):
    c: Horizontal(g0)
    c: Coincident(g0,g1)
    c: Vertical(g1)
    c: Coincident(g1,g2)
    c: Horizontal(g2)
    c: Coincident(g2,g3)
    c: Coincident(g3,g4)
    c: Horizontal(g4)
    c: Coincident(g4,g5)
    c: Coincident(g5,g6)
    c: PointOnObject(g6,g-2)
    c: Horizontal(g6)
    c: Coincident(g6,g7)
    c: Coincident(g11,g0)
    c: Vertical(g7)
    c: Coincident(g-3,g0)
    c: Coincident(g5,g-3)
    c: Coincident(g3,g-4)
    c: Coincident(g2,g-4)
    c: Vertical(g5)
    c: Horizontal(g8)
    c: Coincident(g8,g9)
    c: Vertical(g9)
    c: Coincident(g9,g10)
    c: Horizontal(g10)
    c: Coincident(g7,g10)
    c: Coincident(g11,g8)
    c: Distance(g8,g-5) = 75
    c: Distance(g7,g-6) = 75
    c: DistanceX(g-6,g9) = 75
    c: PointOnObject(g8,g-2)
    c: Vertical(g11)
FEATURE [Part::Extrusion] Extrude064  label="Extrude065"
  Base = -> Sketch089
  Dir = (0,-1e-16,1)
  DirMode = 2
  FaceMakerClass = Part::FaceMakerBullseye
  LengthFwd = 4.5
  LengthRev = 0
  Solid = true
  Symmetric = false
FEATURE [Part::Mirroring] Mirror027  label="Extrude001 (mirrored)"
  Base = (0,2000,0)
  Normal = (1,0,0)
  Source = -> Extrude064
FEATURE [Part::FeaturePython] Channel  label="handrail"  # WARN: FeaturePython — macro-defined, semantics opaque (R4)
  Placement = pos=(0,-1124.19,0) rot=(0,0,1;0rad)
  Reverse = false
  g0 = 7.85
  h = 1100
  k = 90
  l1 = 1125
  l2 = 300
  mass = 31.5207
  p = 1000
  spec = 0
  type = 6
FEATURE [Part::FeaturePython] handrail_001  # a2plus imported part (geometry in sourceFile) (typed FeaturePython)
  Placement = pos=(0,-0.68,0) rot=(0,0,1;0rad)
  a2p_Version = 0.4.60n
  fixedPosition = true
  localSourceObject = Channel
  objectType = a2pPart
  sourceFile = converted
  subassemblyImport = false
  timeLastImport = 1.7091e+09
  updateColors = true
FEATURE [App::FeaturePython] circularEdge_001  label="circularEdge_001__Corner"  # a2plus constraint (typed FeaturePython)
  Object1 = handrail_001
  Object2 = Corner
  SubElement1 = Edge96
  SubElement2 = Edge44
  Suppressed = false
  Type = circularEdge
  directionConstraint = 0
  lockRotation = false
  offset = 0
FEATURE [App::FeaturePython] circularEdge_001_mirror  label="circularEdge_001__handrail_001"  # a2plus constraint (typed FeaturePython)
  Object1 = handrail_001
  Object2 = Corner
  SubElement1 = Edge96
  SubElement2 = Edge44
  Suppressed = false
  Type = circularEdge
  directionConstraint = 0
  lockRotation = false
  offset = 0
FEATURE [Part::Mirroring] Mirror028  label="handrail_001 (mirrored)"
  Base = (0,0,4.5)
  Normal = (0,-1,0)
  Source = -> handrail_001
FEATURE [App::Part] Part031  label="handrail001"
  Group = -> [Channel,handrail_001,circularEdge_001_mirror,circularEdge_001,Mirror028]
  Origin = -> Origin035
FEATURE [Part::FeaturePython] Circle  # WARN: FeaturePython — macro-defined, semantics opaque (R4)
  D = 216
  Placement = pos=(8784.27,2.368e-13,1066.48) rot=(0,0,1;0rad)
  sface = 2
FEATURE [Part::Sweep] Sweep005
  Frenet = false
  Sections = -> [Circle]
  Solid = true
  Spine = -> Sketch044 [Edge2,Edge1]
  Transition = 1
FEATURE [Part::FeaturePython] Circle001  # WARN: FeaturePython — macro-defined, semantics opaque (R4)
  D = 200
  Placement = pos=(8784.27,2.368e-13,1066.48) rot=(0,0,1;0rad)
  sface = 2
FEATURE [Part::Sweep] Sweep006
  Frenet = false
  Sections = -> [Circle001]
  Solid = true
  Spine = -> Sketch044 [Edge2,Edge1]
  Transition = 1
FEATURE [Part::Cut] Cut034
  Base = -> Sweep005
  Tool = -> Sweep006
FEATURE [Part::Cut] Cut035
  Base = -> Cut034
  Tool = -> Revolve007
FEATURE [App::Part] Part012  label="sludgePipe"
  Group = -> [Flange,Revolve007,Sketch044,Sketch046,Circle,Circle001,Cut034,Sweep005,Sweep006,Cut035]
  Origin = -> Origin016
  Placement = pos=(0,0,0) rot=(0,0,-1;-3.14159rad)
FEATURE [Sketcher::SketchObject] Sketch090
  FullyConstrained = true
  MapMode = 5
  Placement = pos=(0,0,850) rot=(0,0,1;0rad)
  Support = -> [Extrude006]
  sketch-geometry (1):
    g0: Circle CenterX=0 CenterY=0 CenterZ=0 NormalX=0 NormalY=0 NormalZ=1 AngleXU=0 Radius=285
  constraints (2):
    c: Coincident(g0,g-1)
    c: Radius(g0) = 285
FEATURE [Part::Extrusion] Extrude065  label="Extrude066"
  Base = -> Sketch090
  Dir = (0,0,1)
  DirMode = 2
  FaceMakerClass = Part::FaceMakerBullseye
  LengthFwd = 50
  LengthRev = 0
  Reversed = true
  Solid = true
  Symmetric = false
FEATURE [Part::Cut] Cut036
  Base = -> Extrude006
  Tool = -> Extrude065
FEATURE [App::Part] ________________1500_v16  label="body_15.5m"
  Group = -> [Part__Feature,Part__Feature001,Single_flange_straight_pipe,Extrude006,Sketch012,Extrude065,Sketch090,Cut036,Sketch,Revolve]
  Origin = -> Origin
FEATURE [Sketcher::SketchObject] Sketch091
  ExternalGeometry = -> [Fusion009]
  FullyConstrained = true
  MapMode = 5
  Placement = pos=(0,0,1.92e-13) rot=(0,0,1;0rad)
  Support = -> [Fusion009]
  sketch-geometry (3):
    g0: LineSegment StartX=8150 StartY=-428 StartZ=0 EndX=8150 EndY=-928 EndZ=0
    g1: LineSegment StartX=8150 StartY=-928 StartZ=0 EndX=6450 EndY=-928 EndZ=0
    g2: LineSegment StartX=6450 StartY=-928 StartZ=0 EndX=6450 EndY=-428 EndZ=0
  constraints (9):
    c: Vertical(g0)
    c: Coincident(g0,g1)
    c: Horizontal(g1)
    c: Coincident(g1,g2)
    c: Vertical(g2)
    c: DistanceY(g0,g0) = 500
    c: DistanceX(g1,g1) = 1700
    c: Coincident(g0,g-3)
    c: PointOnObject(g2,g-3)
FEATURE [Part::FeaturePython] ChannelSteel006  # WARN: FeaturePython — macro-defined, semantics opaque (R4)
  B = 75
  H = 150
  L = 1000
  Placement = pos=(8075,-713.419,-150) rot=(0,0,1;0rad)
  Solid = false
  g0 = 7.85
  mass = 0
  size = 3
  standard = SS
  t1 = 6.5
  t2 = 10
FEATURE [Part::Sweep] Sweep007
  Frenet = false
  Sections = -> [ChannelSteel006]
  Solid = true
  Spine = -> Sketch091 [Edge1,Edge2,Edge3]
  Transition = 1
FEATURE [Part::MultiFuse] Fusion010
  Refine = true
  Shapes = -> [Fusion009,Sweep007]
FEATURE [Sketcher::SketchObject] Sketch092
  ExternalGeometry = -> [Fusion010]
  FullyConstrained = true
  MapMode = 5
  Placement = pos=(0,0,2.13e-13) rot=(0,0,1;0rad)
  Support = -> [Fusion010]
  sketch-geometry (4):
    g0: LineSegment StartX=6450 StartY=-928 StartZ=0 EndX=8150 EndY=-928 EndZ=0
    g1: LineSegment StartX=8150 StartY=-928 StartZ=0 EndX=8150 EndY=-500 EndZ=0
    g2: LineSegment StartX=8150 StartY=-500 StartZ=0 EndX=6450 EndY=-500 EndZ=0
    g3: LineSegment StartX=6450 StartY=-500 StartZ=0 EndX=6450 EndY=-928 EndZ=0
  constraints (10):
    c: Coincident(g0,g1)
    c: Coincident(g1,g2)
    c: Coincident(g2,g3)
    c: Coincident(g3,g0)
    c: Horizontal(g0)
    c: Horizontal(g2)
    c: Vertical(g1)
    c: Vertical(g3)
    c: Coincident(g2,g-4)
    c: Coincident(g0,g-3)
FEATURE [Part::Extrusion] Extrude066  label="Extrude067"
  Base = -> Sketch092
  Dir = (0,-1e-16,1)
  DirMode = 2
  FaceMakerClass = Part::FaceMakerBullseye
  LengthFwd = 4.5
  LengthRev = 0
  Solid = true
  Symmetric = false
FEATURE [Part::FeaturePython] Corner  # WARN: FeaturePython — macro-defined, semantics opaque (R4)
  Placement = pos=(1125,-824.87,0) rot=(0,0,-1;4.71239rad)
  Reverse = false
  g0 = 7.85
  h = 1100
  k = -90
  l1 = 350
  l2 = 5000
  mass = 64.5905
  p = 500
  spec = 0
  type = 2
FEATURE [Part::FeaturePython] Channel001  # WARN: FeaturePython — macro-defined, semantics opaque (R4)
  Placement = pos=(7298.77,-897.91,0) rot=(0,0,1;0rad)
  Reverse = false
  g0 = 7.85
  h = 1100
  k = 90
  l1 = 830
  l2 = 200
  mass = 22.1547
  p = 500
  spec = 0
  type = 6
FEATURE [Part::FeaturePython] Corner001  # WARN: FeaturePython — macro-defined, semantics opaque (R4)
  Placement = pos=(6125,-474.87,0) rot=(0,0,1;0rad)
  Reverse = false
  g0 = 7.85
  h = 1100
  k = -90
  l1 = 345
  l2 = 220
  mass = 4.51427
  p = 1000
  spec = 0
  type = 2
FEATURE [Part::FeaturePython] Corner002  # WARN: FeaturePython — macro-defined, semantics opaque (R4)
  Placement = pos=(1125,824.87,0) rot=(0,0,1;4.71239rad)
  Reverse = true
  g0 = 7.85
  h = 1100
  k = 90
  l1 = 350
  l2 = 7000
  mass = 80.3333
  p = 1000
  spec = 0
  type = 2
FEATURE [Part::Mirroring] Mirror029  label="Corner002 (mirrored)"
  Base = (0,0,0)
  Normal = (1,0,0)
  Source = -> Corner002
FEATURE [Part::Mirroring] Mirror030  label="Corner002 (mirrored) (mirrored)"
  Base = (200,0,0)
  Normal = (0,1,0)
  Source = -> Mirror029
FEATURE [Sketcher::SketchObject] Sketch093
  FullyConstrained = false
  sketch-geometry (4):
    g0: LineSegment StartX=-549.934 StartY=-626.883 StartZ=0 EndX=550.066 EndY=-626.883 EndZ=0
    g1: LineSegment StartX=550.066 StartY=-626.883 StartZ=0 EndX=550.066 EndY=623.117 EndZ=0
    g2: LineSegment StartX=550.066 StartY=623.117 StartZ=0 EndX=-549.934 EndY=623.117 EndZ=0
    g3: LineSegment StartX=-549.934 StartY=623.117 StartZ=0 EndX=-549.934 EndY=-626.883 EndZ=0
  constraints (10):
    c: Coincident(g0,g1)
    c: Coincident(g1,g2)
    c: Coincident(g2,g3)
    c: Coincident(g3,g0)
    c: Horizontal(g0)
    c: Horizontal(g2)
    c: Vertical(g1)
    c: Vertical(g3)
    c: DistanceX(g2,g2) = 1100
    c: DistanceY(g3,g3) = 1250
FEATURE [Part::FeaturePython] AngleSteel020  label="AngleSteel022"  # WARN: FeaturePython — macro-defined, semantics opaque (R4)
  A = 50
  B = 50
  L = 1000
  Placement = pos=(530.113,0,5689.78) rot=(0,0,1;0rad)
  Solid = false
  g0 = 7.85
  mass = 0
  size = 7
  standard = SS_Equal
  t = 6
FEATURE [Part::Sweep] Sweep008
  Frenet = false
  Sections = -> [AngleSteel020]
  Solid = true
  Spine = -> Sketch093 [Edge2,Edge3,Edge4,Edge1]
  Transition = 1
FEATURE [Sketcher::SketchObject] Sketch094
  ExternalGeometry = -> [Sweep008]
  FullyConstrained = false
  Placement = pos=(0,0,0) rot=(1,0,0;1.5708rad)
  sketch-geometry (6):
    g0: LineSegment StartX=-529.981 StartY=5694.78 StartZ=0 EndX=-529.981 EndY=6089.78 EndZ=0
    g1: LineSegment StartX=-529.981 StartY=6089.78 StartZ=0 EndX=-266.336 EndY=6439.78 EndZ=0
    g2: LineSegment StartX=-266.336 StartY=6439.78 StartZ=0 EndX=266.468 EndY=6439.78 EndZ=0
    g3: LineSegment StartX=266.468 StartY=6439.78 StartZ=0 EndX=530.113 EndY=6089.78 EndZ=0
    g4: LineSegment StartX=530.113 StartY=6089.78 StartZ=0 EndX=530.113 EndY=5694.78 EndZ=0
    g5: LineSegment StartX=530.113 StartY=5694.78 StartZ=0 EndX=-529.981 EndY=5694.78 EndZ=0
  constraints (17):
    c: Vertical(g0)
    c: Coincident(g0,g1)
    c: Coincident(g1,g2)
    c: Horizontal(g2)
    c: Coincident(g2,g3)
    c: Coincident(g3,g4)
    c: Coincident(g4,g5)
    c: Horizontal(g5)
    c: Coincident(g0,g5)
    c: Vertical(g4)
    c: DistanceY(g-4,g0) = 5
    c: PointOnObject(g0,g-4)
    c: PointOnObject(g4,g-3)
    c: DistanceY(g-4,g1) = 750
    c: DistanceY(g-4,g0) = 400
    c: Horizontal(g0,g3)
    c: Equal(g1,g3)
FEATURE [Part::Extrusion] Extrude067  label="Extrude068"
  Base = -> Sketch094
  Dir = (0,-1,-3e-16)
  DirMode = 2
  FaceMakerClass = Part::FaceMakerBullseye
  LengthFwd = 1214
  LengthRev = 0
  Solid = true
  Symmetric = true
FEATURE [Part::Thickness] Thickness
  Faces = -> Extrude067 [Face6]
  Intersection = false
  Join = 0
  Mode = 0
  SelfIntersection = false
  Value = 4
FEATURE [App::Part] Part033  label="reducerCover"
  Group = -> [AngleSteel020,Sketch093,Sweep008,Sketch094,Extrude067,Thickness]
  Origin = -> Origin037
FEATURE [Part::FeaturePython] BasePlate  # WARN: FeaturePython — macro-defined, semantics opaque (R4)
  B = 150
  D = 20
  H = 150
  b1 = 30
  h1 = 45
  sface = 0
FEATURE [Part::Extrusion] Extrude068  label="Extrude069"
  Base = -> BasePlate
  Dir = (0,0,1)
  DirMode = 2
  FaceMakerClass = Part::FaceMakerBullseye
  LengthFwd = 10
  LengthRev = 0
  Solid = true
  Symmetric = false
FEATURE [Part::FeaturePython] H_Shape  # WARN: FeaturePython — macro-defined, semantics opaque (R4)
  B = 125
  H = 125
  L = 70
  Solid = true
  g0 = 7.85
  mass = 1.66572
  size = 1
  standard = SS_Wide
FEATURE [Part::MultiFuse] Fusion011  label="PostH"
  Placement = pos=(-8074.76,-424.956,-265) rot=(0,0,1;0rad)
  Shapes = -> [Extrude068,H_Shape]
FEATURE [Part::FeaturePython] Array028  # Draft array (typed FeaturePython)
  AlwaysSyncPlacement = false
  Angle = 360
  ArrayType = 0
  Axis = (0,0,1)
  Base = -> Fusion011
  Center = (0,0,0)
  Count = 4
  ExpandArray = false
  Fuse = false
  IntervalAxis = (0,0,0)
  IntervalX = (16150,0,0)
  IntervalY = (0,850,0)
  IntervalZ = (0,0,100)
  NumberCircles = 3
  NumberPolar = 5
  NumberX = 2
  NumberY = 2
  NumberZ = 1
  PlacementList = 4 placements: [(-8074.76,-424.956,-265),(-8074.76,425.044,-265),(8075.24,-424.956,-265),(8075.24,425.044,-265)]
  RadialDistance = 50
  ScaleList = (4) [(1,1,1),(1,1,1),(1,1,1),(1,1,1)]
  Symmetry = 1
  TangentialDistance = 25
FEATURE [App::Part] Part030  label="bridge001"
  Group = -> [Mirror025,Mirror002,AngleSteel019,Mirror003,Fusion011,Extrude068,H_Shape,BasePlate,Array028]
  Origin = -> Origin034
FEATURE [App::Part] Part032  label="bridge"
  Group = -> [Part031,Part030,Spreadsheet010,Loft,Sketch088,Sketch087,Sketch089,Mirror027,Mirror024,Mirror026,Sketch091,Extrude063,Extrude064,Sweep004,Sweep003,Fusion006,Fusion004,Fusion005,Fusion007,Fusion008,Fusion009,HShapeSteel001,HShapeSteel,AngleSteel018,HShapeSteel002,HShapeSteel003,Clone009,ChannelSteel005,Compound038,Array027,Compound039,Clone008,HShapeSteel004,ChannelSteel006,Sweep007,Fusion010,+8 more]
  Origin = -> Origin036
  Placement = pos=(0,0,5689.73) rot=(0,0,1;0rad)
FEATURE [Part::Compound] Compound040
  Links = -> [Flange_Reducer,F90Elbow,K_Short_tube_No_1th,K_5Elbow,K_Straight_tube,Single_Flange_Length_Tube]
FEATURE [App::Part] Part011  label="inFlowPipe"
  Group = -> [Flange_Reducer,F90Elbow,K_Short_tube_No_1th,K_5Elbow,K_Straight_tube,Single_Flange_Length_Tube,Compound040]
  Origin = -> Origin015
FEATURE [Part::Mirroring] Mirror031  label="Array025 (mirrored)"
  Base = (0,-3000,0)
  Normal = (1,0,0)
  Source = -> Array025
FEATURE [Part::Mirroring] Mirror032  label="TurnBackleC (mirrored)"
  Base = (0,-3000,0)
  Normal = (1,0,0)
  Source = -> Part019
FEATURE [Part::Mirroring] Mirror033  label="TurnBackleC001 (mirrored)"
  Base = (0,-3000,0)
  Normal = (1,0,0)
  Source = -> Part021
FEATURE [App::Part] Part018  label="feedWell"
  Group = -> [Part016,Part015,Part014,Compound026,Spreadsheet005,Spreadsheet006,Mirror016,Mirror004,Mirror018,AngleSteel017,Compound028,Extrude045,Sketch065,Mirror017,ChannelSteel004,Array025,Part019,Part021,Part025,Part028,Part029,Compound033,circularEdge_007,circularEdge_004_mirror001,Compound034,Part027,axisCoincident_002_mirror001,Flange001,Ring,Compound036,Extrude054,Part024,axisCoincident_001_mirror001,+5 more]
  Origin = -> Origin022
  Placement = pos=(0,0,2977.83) rot=(0,0,1;0rad)
FEATURE [Part::FeaturePython] SquarePipe  # WARN: FeaturePython — macro-defined, semantics opaque (R4)
  A = 125
  B = 125
  L = 5980
  Placement = pos=(0,0,0) rot=(0,-1,0;1.5708rad)
  Solid = true
  g0 = 7.85
  mass = 109.641
  size = 39
  standard = SS
  t = 1
  expr: L = Spreadsheet011.L0
FEATURE [Sketcher::SketchObject] Sketch095
  ExternalGeometry = -> [SquarePipe]
  FullyConstrained = true
  MapMode = 5
  Placement = pos=(-5980,6.639e-13,1.3278e-12) rot=(0,-1,0;1.5708rad)
  Support = -> [SquarePipe]
  sketch-geometry (4):
    g0: LineSegment StartX=-62.5 StartY=-62.5 StartZ=0 EndX=62.5 EndY=-62.5 EndZ=0
    g1: LineSegment StartX=62.5 StartY=-62.5 StartZ=0 EndX=62.5 EndY=62.5 EndZ=0
    g2: LineSegment StartX=62.5 StartY=62.5 StartZ=0 EndX=-62.5 EndY=62.5 EndZ=0
    g3: LineSegment StartX=-62.5 StartY=62.5 StartZ=0 EndX=-62.5 EndY=-62.5 EndZ=0
  constraints (11):
    c: Coincident(g0,g1)
    c: Coincident(g1,g2)
    c: Coincident(g2,g3)
    c: Coincident(g3,g0)
    c: Horizontal(g0)
    c: Horizontal(g2)
    c: Vertical(g3)
    c: DistanceX(g2,g2) = 125
    c: Equal(g1,g0)
    c: PointOnObject(g-4,g2)
    c: Tangent(g-3,g1) = -1.5708
FEATURE [Part::Extrusion] Extrude069  label="Extrude070"
  Base = -> Sketch095
  Dir = (-1,1e-16,2e-16)
  DirMode = 2
  FaceMakerClass = Part::FaceMakerBullseye
  LengthFwd = 6
  LengthRev = 0
  Solid = true
  Symmetric = false
FEATURE [Part::FeaturePython] Clone010  label="Extrude071"  # Draft clone (typed FeaturePython)
  AttacherType = Attacher::AttachEngine3D
  Fuse = false
  Objects = -> [Extrude069]
  Placement = pos=(5986,0,0) rot=(0,0,1;0rad)
  Scale = (1,1,1)
  expr: .Placement.Base.x = Spreadsheet011.L0 + 6
FEATURE [Spreadsheet::Sheet] Spreadsheet011
  cells = A1='tankDia   D0; B1(D0)=15500; A2='L; B2(L0)=5980; A3='bradeWidth W0; B3(W0)==D0 / 4 + 300; A4='brade      n0; B4(n0)=5; A5='brade     w1; B5(w1)==W0 / 5
FEATURE [Sketcher::SketchObject] Sketch096  label="skimmerBrade"
  ExternalGeometry = -> [Clone010]
  FullyConstrained = true
  Placement = pos=(0,0,0) rot=(1,0,0;1.5708rad)
  sketch-geometry (7):
    g0: LineSegment StartX=6 StartY=62.5 StartZ=0 EndX=36 EndY=62.5 EndZ=0
    g1: LineSegment StartX=36 StartY=62.5 StartZ=0 EndX=100.694 EndY=26.1551 EndZ=0
    g2: ArcOfCircle CenterX=86 CenterY=0 CenterZ=0 NormalX=0 NormalY=0 NormalZ=1 AngleXU=0 Radius=30 StartAngle=5.22424 EndAngle=7.34213
    g3: LineSegment StartX=100.694 StartY=-26.1551 StartZ=0 EndX=36 EndY=-62.5 EndZ=0
    g4: LineSegment StartX=36 StartY=-62.5 StartZ=0 EndX=6 EndY=-62.5 EndZ=0
    g5: LineSegment StartX=6 StartY=-62.5 StartZ=0 EndX=6 EndY=62.5 EndZ=0
    g6: Circle CenterX=86 CenterY=0 CenterZ=0 NormalX=0 NormalY=0 NormalZ=1 AngleXU=0 Radius=13
  constraints (17):
    c: Horizontal(g0)
    c: Coincident(g0,g1)
    c: Tangent(g1,g2) = 1.5708
    c: Coincident(g3,g4)
    c: Coincident(g4,g5)
    c: Coincident(g5,g0)
    c: PointOnObject(g6,g-1)
    c: Coincident(g0,g-3)
    c: Coincident(g4,g-3)
    c: Horizontal(g4)
    c: DistanceX(g0,g0) = 30
    c: Equal(g0,g4)
    c: Coincident(g2,g6)
    c: DistanceX(g4,g2) = 80
    c: Diameter(g6) = 26
    c: Radius(g2) = 30
    c: Tangent(g2,g3) = 1.5708
FEATURE [Part::Extrusion] Extrude070  label="Extrude072"
  Base = -> Sketch096
  Dir = (0,-1,2e-16)
  DirMode = 2
  FaceMakerClass = Part::FaceMakerBullseye
  LengthFwd = 10
  LengthRev = 0
  Solid = true
  Symmetric = true
FEATURE [Sketcher::SketchObject] Sketch097
  FullyConstrained = false
  Placement = pos=(0,0,0) rot=(1,0,0;1.5708rad)
  sketch-geometry (7):
    g0: ArcOfCircle CenterX=81.7032 CenterY=0 CenterZ=0 NormalX=0 NormalY=0 NormalZ=1 AngleXU=0 Radius=30 StartAngle=2.05435 EndAngle=4.1734
    g1: LineSegment StartX=67.7553 StartY=26.5604 StartZ=0 EndX=131.703 EndY=60.1419 EndZ=0
    g2: LineSegment StartX=131.703 StartY=60.1419 StartZ=0 EndX=161.703 EndY=60.1419 EndZ=0
    g3: LineSegment StartX=161.703 StartY=60.1419 StartZ=0 EndX=161.703 EndY=-64.8581 EndZ=0
    g4: LineSegment StartX=161.703 StartY=-64.8581 StartZ=0 EndX=131.703 EndY=-64.8581 EndZ=0
    g5: LineSegment StartX=131.703 StartY=-64.8581 StartZ=0 EndX=66.3053 EndY=-25.7469 EndZ=0
    g6: Circle CenterX=81.7032 CenterY=0 CenterZ=0 NormalX=0 NormalY=0 NormalZ=1 AngleXU=0 Radius=13
  constraints (17):
    c: PointOnObject(g0,g-1)
    c: Coincident(g1,g2)
    c: Horizontal(g2)
    c: Coincident(g2,g3)
    c: Coincident(g3,g4)
    c: Coincident(g4,g5)
    c: Tangent(g0,g5) = 1.5708
    c: Tangent(g0,g1) = 1.5708
    c: Vertical(g3)
    c: Distance(g0,g3) = 80
    c: Horizontal(g4)
    c: DistanceX(g2,g2) = 30
    c: Equal(g2,g4)
    c: Radius(g0) = 30
    c: Coincident(g6,g0)
    c: Diameter(g6) = 26
    c: DistanceY(g3,g3) = 125
FEATURE [Part::Extrusion] Extrude071  label="Extrude073"
  Base = -> Sketch097
  Dir = (0,-1,2e-16)
  DirMode = 2
  FaceMakerClass = Part::FaceMakerBullseye
  LengthFwd = 6
  LengthRev = 0
  Placement = pos=(0,9,0) rot=(0,0,1;0rad)
  Solid = true
  Symmetric = true
FEATURE [Sketcher::SketchObject] Sketch098
  ExternalGeometry = -> [Extrude071]
  FullyConstrained = false
  MapMode = 5
  Placement = pos=(161.703,9,0) rot=(0.57735,0.57735,0.57735;2.0944rad)
  Support = -> [Extrude071]
  sketch-geometry (4):
    g0: LineSegment StartX=-59 StartY=-64.8581 StartZ=0 EndX=41 EndY=-64.8581 EndZ=0
    g1: LineSegment StartX=41 StartY=-64.8581 StartZ=0 EndX=41 EndY=60.1419 EndZ=0
    g2: LineSegment StartX=41 StartY=60.1419 StartZ=0 EndX=-59 EndY=60.1419 EndZ=0
    g3: LineSegment StartX=-59 StartY=60.1419 StartZ=0 EndX=-59 EndY=-64.8581 EndZ=0
  constraints (8):
    c: Coincident(g0,g3)
    c: Coincident(g2,g3)
    c: Coincident(g0,g1)
    c: Coincident(g1,g2)
    c: DistanceY(g1,g1) = 125
    c: Horizontal(g2)
    c: Horizontal(g0)
    c: PointOnObject(g-3,g2)
FEATURE [Part::Extrusion] Extrude072  label="Extrude074"
  Base = -> Sketch098
  Dir = (1,0,0)
  DirMode = 2
  FaceMakerClass = Part::FaceMakerBullseye
  LengthFwd = 10
  LengthRev = 0
  Solid = true
  Symmetric = false
FEATURE [Part::Feature] Part__Feature011  label="CNROK75-U_b"
  shape: bbox 47.01 x 65.51 x 70.01 mm, 58 faces (baked)
FEATURE [Part::Feature] Part__Feature012  label="CNROK75-U_w"
  shape: bbox 41.3 x 78.6 x 78.6 mm, 86 faces (baked)
FEATURE [App::Part] CNROK75_U  label="CNROK75-U"
  Group = -> [Part__Feature011,Part__Feature012]
  Origin = -> Origin041
  Placement = pos=(-5937,2.9e-14,-118.52) rot=(1,0,0;1.5708rad)
FEATURE [Part::FeaturePython] Clone011  label="Extrude075"  # Draft clone (typed FeaturePython)
  AttacherType = Attacher::AttachEngine3D
  Fuse = false
  Objects = -> [Extrude071]
  Placement = pos=(0,-9,0) rot=(0,0,1;0rad)
  Scale = (1,1,1)
FEATURE [App::Part] Part035  label="gusset002"
  Group = -> [Sketch097,Sketch098,Extrude071,Extrude072,Clone011]
  Origin = -> Origin039
  Placement = pos=(4,0,0) rot=(0,0,1;0rad)
FEATURE [App::FeaturePython] axisCoincident_001_mirror  label="axisCoincident_001__gusset001"  # a2plus constraint (typed FeaturePython)
  Object1 = Compound001
  Object2 = Compound_001
  SubElement1 = Edge54
  SubElement2 = Edge93
  Suppressed = false
  Type = axial
  directionConstraint = 0
  lockRotation = false
FEATURE [Part::Feature] Part__Feature013  label="HNS3L_1"
  shape: bbox 64 x 7.5 x 21.75 mm, 15 faces (baked)
FEATURE [Part::Feature] Part__Feature014  label="HNS3L_2"
  shape: bbox 64 x 7.5 x 21.75 mm, 12 faces (baked)
FEATURE [App::Part] HNS3L
  Group = -> [Part__Feature013,Part__Feature014]
  Origin = -> Origin042
  Placement = pos=(-367.5,-8,115) rot=(1,0,0;3.14159rad)
  expr: .Placement.Base.x = -Spreadsheet011.w1 / 2 + 50
FEATURE [Sketcher::SketchObject] Sketch099
  FullyConstrained = true
  Placement = pos=(0,0,0) rot=(1,0,0;1.5708rad)
  expr: Constraints[10] = Spreadsheet011.w1
  sketch-geometry (5):
    g0: LineSegment StartX=-417.5 StartY=-107.5 StartZ=0 EndX=-417.5 EndY=107.5 EndZ=0
    g1: LineSegment StartX=-417.5 StartY=107.5 StartZ=0 EndX=417.5 EndY=107.5 EndZ=0
    g2: LineSegment StartX=417.5 StartY=107.5 StartZ=0 EndX=417.5 EndY=-107.5 EndZ=0
    g3: LineSegment StartX=417.5 StartY=-107.5 StartZ=0 EndX=-417.5 EndY=-107.5 EndZ=0
    g4: GeomPoint X=0 Y=0 Z=0
  constraints (12):
    c: Coincident(g0,g1)
    c: Coincident(g1,g2)
    c: Coincident(g2,g3)
    c: Coincident(g3,g0)
    c: Horizontal(g1)
    c: Horizontal(g3)
    c: Vertical(g0)
    c: Vertical(g2)
    c: Symmetric(g1,g0,g4)
    c: Coincident(g4,g-1)
    c: Distance(g1) = 835
    c: DistanceY(g2,g2) = 215
FEATURE [Part::Extrusion] Extrude073  label="Extrude076"
  Base = -> Sketch099
  Dir = (0,-1,2e-16)
  DirMode = 2
  FaceMakerClass = Part::FaceMakerBullseye
  LengthFwd = 5
  LengthRev = 0
  Placement = pos=(0,-4.5,-12) rot=(0,0,1;0rad)
  Solid = true
  Symmetric = false
FEATURE [Part::FeaturePython] Clone012  label="HNS3L001"  # Draft clone (typed FeaturePython)
  AttacherType = Attacher::AttachEngine3D
  Fuse = false
  Objects = -> [HNS3L]
  Placement = pos=(303.5,-8,115) rot=(1,0,0;3.14159rad)
  Scale = (1,1,1)
  expr: .Placement.Base.x = Spreadsheet011.w1 / 2 - 114
FEATURE [Sketcher::SketchObject] Sketch100
  FullyConstrained = true
  Placement = pos=(0,0,0) rot=(1,0,0;1.5708rad)
  expr: Constraints[11] = Spreadsheet011.w1
  sketch-geometry (5):
    g0: LineSegment StartX=-417.5 StartY=-37.5 StartZ=0 EndX=-417.5 EndY=37.5 EndZ=0
    g1: LineSegment StartX=-417.5 StartY=37.5 StartZ=0 EndX=417.5 EndY=37.5 EndZ=0
    g2: LineSegment StartX=417.5 StartY=37.5 StartZ=0 EndX=417.5 EndY=-37.5 EndZ=0
    g3: LineSegment StartX=417.5 StartY=-37.5 StartZ=0 EndX=-417.5 EndY=-37.5 EndZ=0
    g4: GeomPoint X=0 Y=0 Z=0
  constraints (12):
    c: Coincident(g0,g1)
    c: Coincident(g1,g2)
    c: Coincident(g2,g3)
    c: Coincident(g3,g0)
    c: Horizontal(g1)
    c: Horizontal(g3)
    c: Vertical(g0)
    c: Vertical(g2)
    c: Symmetric(g1,g0,g4)
    c: Coincident(g4,g-1)
    c: DistanceY(g2,g2) = 75
    c: DistanceX(g3,g3) = 835
FEATURE [Part::Extrusion] Extrude074  label="Extrude077"
  Base = -> Sketch100
  Dir = (0,-1,2e-16)
  DirMode = 2
  FaceMakerClass = Part::FaceMakerBullseye
  LengthFwd = 3
  LengthRev = 0
  Placement = pos=(0,-9.5,70) rot=(0,0,1;0rad)
  Solid = true
  Symmetric = false
FEATURE [Sketcher::SketchObject] Sketch101
  ExternalGeometry = -> [Extrude073,Extrude074]
  FullyConstrained = true
  MapMode = 5
  Placement = pos=(-417.5,-4.5,-12) rot=(0.57735,-0.57735,-0.57735;2.0944rad)
  Support = -> [Extrude073]
  sketch-geometry (4):
    g0: LineSegment StartX=2.4e-14 StartY=107.5 StartZ=0 EndX=-3 EndY=107.5 EndZ=0
    g1: LineSegment StartX=-3 StartY=107.5 StartZ=0 EndX=-3 EndY=44.5 EndZ=0
    g2: LineSegment StartX=-3 StartY=44.5 StartZ=0 EndX=2.4e-14 EndY=44.5 EndZ=0
    g3: LineSegment StartX=2.4e-14 StartY=44.5 StartZ=0 EndX=2.4e-14 EndY=107.5 EndZ=0
  constraints (11):
    c: Coincident(g0,g1)
    c: Coincident(g1,g2)
    c: Coincident(g2,g3)
    c: Coincident(g3,g0)
    c: Horizontal(g0)
    c: Horizontal(g2)
    c: Vertical(g1)
    c: Vertical(g3)
    c: DistanceX(g0,g0) = 3
    c: Coincident(g0,g-3)
    c: Horizontal(g1,g-4)
FEATURE [Part::Extrusion] Extrude075  label="Extrude078"
  Base = -> Sketch101
  Dir = (-1,0,0)
  DirMode = 2
  FaceMakerClass = Part::FaceMakerBullseye
  LengthFwd = 835
  LengthRev = 0
  Reversed = true
  Solid = true
  Symmetric = false
  expr: LengthFwd = Spreadsheet011.w1
FEATURE [Sketcher::SketchObject] Sketch102
  FullyConstrained = false
  MapMode = 5
  Placement = pos=(-417.5,-4.5,-12) rot=(0.57735,-0.57735,-0.57735;2.0944rad)
  Support = -> [Extrude073]
  sketch-geometry (8):
    g0: LineSegment StartX=-104.645 StartY=156.908 StartZ=0 EndX=-4.64507 EndY=156.908 EndZ=0
    g1: LineSegment StartX=3.35493 StartY=148.908 StartZ=0 EndX=3.35493 EndY=130.908 EndZ=0
    g2: LineSegment StartX=3.35493 StartY=130.908 StartZ=0 EndX=0.354931 EndY=130.908 EndZ=0
    g3: LineSegment StartX=0.354931 StartY=130.908 StartZ=0 EndX=0.354931 EndY=148.908 EndZ=0
    g4: LineSegment StartX=-4.64507 StartY=153.908 StartZ=0 EndX=-104.645 EndY=153.908 EndZ=0
    g5: LineSegment StartX=-104.645 StartY=153.908 StartZ=0 EndX=-104.645 EndY=156.908 EndZ=0
    g6: ArcOfCircle CenterX=-4.64507 CenterY=148.908 CenterZ=0 NormalX=0 NormalY=0 NormalZ=1 AngleXU=0 Radius=5 StartAngle=3.3e-15 EndAngle=1.5708
    g7: ArcOfCircle CenterX=-4.64507 CenterY=148.908 CenterZ=0 NormalX=0 NormalY=0 NormalZ=1 AngleXU=0 Radius=8 StartAngle=-1.8e-15 EndAngle=1.5708
  constraints (19):
    c: Horizontal(g0)
    c: Vertical(g1)
    c: Coincident(g1,g2)
    c: Horizontal(g2)
    c: Coincident(g2,g3)
    c: Vertical(g3)
    c: Horizontal(g4)
    c: Coincident(g4,g5)
    c: Coincident(g5,g0)
    c: Vertical(g5)
    c: DistanceX(g2,g2) = 3
    c: Tangent(g3,g6) = -1.5708
    c: Tangent(g4,g6) = -1.5708
    c: Tangent(g1,g7) = 1.5708
    c: Tangent(g0,g7) = 1.5708
    c: Coincident(g6,g7)
    c: DistanceX(g4,g4) = 100
    c: DistanceY(g3,g3) = 18
    c: Radius(g6) = 5
FEATURE [Part::Extrusion] Extrude076  label="Extrude079"
  Base = -> Sketch102
  Dir = (-1,0,0)
  DirMode = 2
  FaceMakerClass = Part::FaceMakerBullseye
  LengthFwd = 80
  LengthRev = 0
  Placement = pos=(34,0,0) rot=(0,0,1;0rad)
  Reversed = true
  Solid = true
  Symmetric = false
FEATURE [Part::FeaturePython] Clone013  label="Extrude080"  # Draft clone (typed FeaturePython)
  AttacherType = Attacher::AttachEngine3D
  Fuse = false
  Objects = -> [Extrude076]
  Placement = pos=(705,0,0) rot=(0,0,1;0rad)
  Scale = (1,1,1)
  expr: .Placement.Base.x = Spreadsheet011.w1 - (50 + 46 + 34)
FEATURE [App::Part] Part037  label="brade001"
  Group = -> [Sketch099,Extrude073,Clone012,HNS3L,Sketch100,Extrude074,Sketch101,Extrude075,Sketch102,Extrude076,Clone013]
  Origin = -> Origin043
  Placement = pos=(-5437.87,-100,-207.547) rot=(0,0,1;0rad)
FEATURE [Part::FeaturePython] Array029  label="brade002"  # Draft array (typed FeaturePython)
  AlwaysSyncPlacement = false
  Angle = 360
  ArrayType = 0
  Axis = (0,0,1)
  Base = -> Part037
  Center = (0,0,0)
  Count = 5
  ExpandArray = false
  Fuse = false
  IntervalAxis = (0,0,0)
  IntervalX = (835,0,0)
  IntervalY = (0,100,0)
  IntervalZ = (0,0,100)
  NumberCircles = 3
  NumberPolar = 5
  NumberX = 5
  NumberY = 1
  NumberZ = 1
  PlacementList = 5 placements: arithmetic series from (-5437.87,-100,-207.547) step (835,0,0) to (-2097.87,-100,-207.547)
  RadialDistance = 50
  ScaleList = (5) [(1,1,1),(1,1,1),(1,1,1),(1,1,1),(1,1,1)]
  Symmetry = 1
  TangentialDistance = 25
  expr: .IntervalX.x = Spreadsheet011.w1
FEATURE [Part::FeaturePython] ChannelSteel007  # WARN: FeaturePython — macro-defined, semantics opaque (R4)
  B = 75
  H = 150
  L = 1000
  Placement = pos=(176,0,-75) rot=(0,0,1;0rad)
  Solid = false
  g0 = 7.85
  mass = 0
  size = 3
  standard = SS
  t1 = 6.5
  t2 = 10
FEATURE [Part::Extrusion] Extrude077  label="Extrude081"
  Base = -> ChannelSteel007
  Dir = (0,1,0)
  DirMode = 2
  FaceMakerClass = Part::FaceMakerBullseye
  LengthFwd = 1620
  LengthRev = 0
  Solid = false
  Symmetric = true
FEATURE [Sketcher::SketchObject] Sketch103
  FullyConstrained = true
  MapMode = 5
  Placement = pos=(0,0,62.5) rot=(0,0,1;0rad)
  sketch-geometry (6):
    g0: LineSegment StartX=-2985 StartY=62.5 StartZ=0 EndX=-2985 EndY=112.5 EndZ=0
    g1: ArcOfCircle CenterX=-3000 CenterY=112.5 CenterZ=0 NormalX=0 NormalY=0 NormalZ=1 AngleXU=0 Radius=15 StartAngle=0 EndAngle=1.98689
    g2: LineSegment StartX=-3006.06 StartY=126.22 StartZ=0 EndX=-3105 EndY=82.5 EndZ=0
    g3: LineSegment StartX=-3105 StartY=82.5 StartZ=0 EndX=-3105 EndY=62.5 EndZ=0
    g4: LineSegment StartX=-3105 StartY=62.5 StartZ=0 EndX=-2985 EndY=62.5 EndZ=0
    g5: Circle CenterX=-3000 CenterY=112.5 CenterZ=0 NormalX=0 NormalY=0 NormalZ=1 AngleXU=0 Radius=7.5
  constraints (16):
    c: Tangent(g0,g1) = -1.5708
    c: Coincident(g2,g3)
    c: Vertical(g3)
    c: Coincident(g3,g4)
    c: Coincident(g4,g0)
    c: Coincident(g5,g1)
    c: Diameter(g5) = 15
    c: Radius(g1) = 15
    c: Vertical(g0)
    c: Tangent(g1,g2) = -1.5708
    c: Horizontal(g4)
    c: DistanceY(g3,g3) = 20
    c: DistanceX(g4,g4) = 120
    c: DistanceY(g0,g1) = 50
    c: DistanceY(g-1,g0) = 62.5
    c: DistanceX(g-2,g1) = -3000
FEATURE [Part::Extrusion] Extrude078  label="Extrude082"
  Base = -> Sketch103
  Dir = (0,0,1)
  DirMode = 2
  FaceMakerClass = Part::FaceMakerBullseye
  LengthFwd = 6
  LengthRev = 0
  Placement = pos=(0,0,-62.5) rot=(0,0,1;0rad)
  Solid = true
  Symmetric = true
FEATURE [Part::Mirroring] Mirror034  label="Extrude020 (mirrored)"
  Base = (-3100,0,0)
  Normal = (0,-1,0)
  Source = -> Extrude078
FEATURE [App::Part] Part034  label="hontai"
  Group = -> [Sketch096,Clone010,SquarePipe,Sketch095,Extrude069,Extrude070,Sketch103,Extrude078,Mirror034]
  Origin = -> Origin038
FEATURE [Part::Compound] Compound041  label="hontai001"
  Links = -> [Part034]
FEATURE [Sketcher::SketchObject] Sketch104
  ExternalGeometry = -> [Extrude077]
  FullyConstrained = false
  MapMode = 5
  Placement = pos=(0,0,75) rot=(0,0,1;0rad)
  Support = -> [Extrude077]
  sketch-geometry (7):
    g0: LineSegment StartX=176 StartY=810 StartZ=0 EndX=156 EndY=810 EndZ=0
    g1: LineSegment StartX=156 StartY=810 StartZ=0 EndX=118.097 EndY=782.842 EndZ=0
    g2: ArcOfCircle CenterX=126 CenterY=771.812 CenterZ=0 NormalX=0 NormalY=0 NormalZ=1 AngleXU=0 Radius=13.569 StartAngle=2.19251 EndAngle=4.2132
    g3: LineSegment StartX=119.504 StartY=759.899 StartZ=0 EndX=156 EndY=740 EndZ=0
    g4: LineSegment StartX=156 StartY=740 StartZ=0 EndX=176 EndY=740 EndZ=0
    g5: LineSegment StartX=176 StartY=740 StartZ=0 EndX=176 EndY=810 EndZ=0
    g6: Circle CenterX=126 CenterY=771.812 CenterZ=0 NormalX=0 NormalY=0 NormalZ=1 AngleXU=0 Radius=7.5
  constraints (16):
    c: Horizontal(g0)
    c: Coincident(g0,g1)
    c: Tangent(g1,g2) = -1.5708
    c: Coincident(g3,g4)
    c: Horizontal(g4)
    c: Coincident(g4,g5)
    c: Coincident(g5,g0)
    c: Vertical(g5)
    c: Coincident(g6,g2)
    c: Diameter(g6) = 15
    c: Coincident(g0,g-3)
    c: DistanceY(g5,g5) = 70
    c: Tangent(g2,g3) = -1.5708
    c: Vertical(g0,g3)
    c: DistanceX(g0,g0) = 20
    c: Distance(g2,g5) = 50
FEATURE [Part::Extrusion] Extrude079  label="Extrude083"
  Base = -> Sketch104
  Dir = (0,0,1)
  DirMode = 2
  FaceMakerClass = Part::FaceMakerBullseye
  LengthFwd = 6
  LengthRev = 0
  Placement = pos=(0,0,-75) rot=(0,0,1;0rad)
  Solid = true
  Symmetric = true
FEATURE [Part::Mirroring] Mirror035  label="Extrude021 (mirrored)"
  Base = (1000,0,0)
  Normal = (0,-1,0)
  Source = -> Extrude079
FEATURE [Spreadsheet::Sheet] Spreadsheet012
  cells = A2='rodDia dia; B2(dia)=12; C2='thickness; D2(t0)=6; A3='length L0; B3(L0)=3195; C3='l1; D3(l1)==L0 - (dia * 5 + 500); B4='l; C4='l1; D4='a; E4='b; F4='c; G4='e; H4='f; I4='g; J4='h; K4='i; L4='r; A5='forkEndR; B5=80; D5=25; E5=10; F5=14; G5=16; H5=13; I5=40; J5=5; K5=13; L5=15; A6='turnBackle; B6=100; C6=20; D6=30; E6=16; F6=22; A7='forkEndL; B7=60; D7=25; E7=10; F7=13; G7=16; H7=13; I7=20; L7=15; A8=1; B8=2; C8=3; D8=4; E8=5; F8=6; G8=7; H8=8; I8=9; J8=10; K8=11; L8=12; A9='turnBackle; A10='d; B10='l; C10='l1; D10='a; E10='b; F10='c; G10='t0; A11=10; B11=75; C11=15; D11=24; E11=13; F11=17; G11=6; A12=12; B12=100; C12=20; D12=30; E12=16; F12=22; G12=6; A13=16; B13=125; C13=24; D13=36; E13=20; F13=27; G13=9; A14=20; B14=150; C14=28; D14=42; E14=23; F14=33; G14=9; A15=22; B15=175; C15=33; D15=48; E15=27; F15=37; G15=9; A16=24; B16=200; C16=38; D16=54; E16=30; F16=42; G16=12; A17=30; B17=250; C17=47; D17=66; E17=37; F17=52; G17=12; A18='forkEnd_L; A19='d; B19='l; C19='a; D19='b; E19='c; F19='e; G19='f; H19='g; I19='r; A20=10; B20=50; C20=20; D20=7; E20=10; F20=12; G20=10; H20=15; I20=12; A21=12; B21=60; C21=25; D21=10; E21=13; F21=16; G21=13; H21=20; I21=15; A22=16; B22=75; C22=30; D22=13; E22=16; F22=20; G22=16; H22=25; I22=19; A23=20; B23=90; C23=40; D23=16; E23=20; F23=24; G23=20; H23=30; I23=23; A24=22; B24=100; C24=45; D24=20; E24=23; F24=28; G24=23; H24=35; I24=27; A25=24; B25=115; C25=50; D25=23; E25=26; F25=32; G25=26; H25=40; I25=30; A26=30; B26=140; C26=65; D26=30; E26=33; F26=40; G26=33; H26=50; I26=38; A27='forkEnd_R; A28='d; B28='l; C28='a; D28='b; E28='c; F28='r; G28='e; H28='f; I28='g; J28='h; K28='i; A29=10; +76 more cells
FEATURE [Sketcher::SketchObject] Sketch105
  FullyConstrained = true
  Placement = pos=(0,0,0) rot=(1,0,0;1.5708rad)
  expr: Constraints[11] = Spreadsheet012.I5 + Spreadsheet012.dia * 2
  expr: Constraints[1] = Spreadsheet012.F5 / 2
  expr: Constraints[3] = Spreadsheet012.L5
  sketch-geometry (5):
    g0: Circle CenterX=0 CenterY=0 CenterZ=0 NormalX=0 NormalY=0 NormalZ=1 AngleXU=0 Radius=7
    g1: ArcOfCircle CenterX=0 CenterY=0 CenterZ=0 NormalX=0 NormalY=0 NormalZ=1 AngleXU=0 Radius=15 StartAngle=4.71239 EndAngle=7.85398
    g2: LineSegment StartX=-4.87e-14 StartY=15 StartZ=0 EndX=-64 EndY=15 EndZ=0
    g3: LineSegment StartX=-64 StartY=15 StartZ=0 EndX=-64 EndY=-15 EndZ=0
    g4: LineSegment StartX=-64 StartY=-15 StartZ=0 EndX=0 EndY=-15 EndZ=0
  constraints (12):
    c: Coincident(g0,g-1)
    c: Radius(g0) = 7
    c: Coincident(g1,g0)
    c: Radius(g1) = 15
    c: Horizontal(g2)
    c: Coincident(g2,g3)
    c: Vertical(g3)
    c: Coincident(g3,g4)
    c: Horizontal(g4)
    c: Tangent(g1,g2) = -1.5708
    c: Tangent(g1,g4) = -1.5708
    c: Distance(g2) = 64
FEATURE [Part::Cylinder] Cylinder007  label="円柱004"
  Angle = 360
  AttacherType = Attacher::AttachEngine3D
  FirstAngle = 0
  Height = 500
  Placement = pos=(-24,0,0) rot=(0,-1,0;1.5708rad)
  Radius = 6
  SecondAngle = 0
  expr: .Placement.Base.x = -Spreadsheet012.dia * 2
  expr: Radius = Spreadsheet012.dia / 2
FEATURE [Sketcher::SketchObject] Sketch106
  FullyConstrained = true
  Placement = pos=(0,0,0) rot=(1,0,0;1.5708rad)
  expr: Constraints[10] = Spreadsheet012.C6
  expr: Constraints[11] = Spreadsheet012.B6
  expr: Constraints[12] = Spreadsheet012.D6 / 2
  expr: Constraints[13] = Spreadsheet012.F6 / 2
  expr: Constraints[14] = Spreadsheet012.B6 / 2
  expr: Constraints[17] = Spreadsheet012.C6
  sketch-geometry (6):
    g0: LineSegment StartX=-50 StartY=0 StartZ=0 EndX=-50 EndY=11 EndZ=0
    g1: LineSegment StartX=-50 StartY=11 StartZ=0 EndX=-30 EndY=15 EndZ=0
    g2: LineSegment StartX=-30 StartY=15 StartZ=0 EndX=30 EndY=15 EndZ=0
    g3: LineSegment StartX=30 StartY=15 StartZ=0 EndX=50 EndY=11 EndZ=0
    g4: LineSegment StartX=50 StartY=11 StartZ=0 EndX=50 EndY=0 EndZ=0
    g5: LineSegment StartX=50 StartY=0 StartZ=0 EndX=-50 EndY=0 EndZ=0
  constraints (18):
    c: PointOnObject(g0,g-1)
    c: Vertical(g0)
    c: Coincident(g0,g1)
    c: Coincident(g1,g2)
    c: Horizontal(g2)
    c: Coincident(g2,g3)
    c: Coincident(g3,g4)
    c: PointOnObject(g4,g-1)
    c: Vertical(g4)
    c: Coincident(g4,g5)
    c: DistanceX(g2,g3) = 20
    c: DistanceX(g0,g3) = 100
    c: Distance(g1,g5) = 15
    c: Distance(g4) = 11
    c: DistanceX(g-1,g4) = 50
    c: Horizontal(g0,g3)
    c: Coincident(g5,g0)
    c: DistanceX(g0,g1) = 20
FEATURE [Part::Revolution] Revolve017
  Angle = 360
  Axis = (-1,0,0)
  AxisLink = -> Sketch106 [Edge6]
  Base = (-50,0,0)
  FaceMakerClass = Part::FaceMakerBullseye
  Solid = true
  Source = -> Sketch106
  Symmetric = false
FEATURE [Sketcher::SketchObject] Sketch107
  FullyConstrained = false
  Placement = pos=(0,0,0) rot=(0.57735,0.57735,0.57735;2.0944rad)
  expr: Constraints[16] = Spreadsheet012.F6
  expr: Constraints[17] = Spreadsheet012.F6 / 2
  sketch-geometry (8):
    g0: LineSegment StartX=-11 StartY=39.685 StartZ=0 EndX=-26 EndY=39.685 EndZ=0
    g1: LineSegment StartX=-26 StartY=39.685 StartZ=0 EndX=-26 EndY=-39.3666 EndZ=0
    g2: LineSegment StartX=-26 StartY=-39.3666 StartZ=0 EndX=-11 EndY=-39.3666 EndZ=0
    g3: LineSegment StartX=-11 StartY=-39.3666 StartZ=0 EndX=-11 EndY=39.685 EndZ=0
    g4: LineSegment StartX=11 StartY=39.685 StartZ=0 EndX=26 EndY=39.685 EndZ=0
    g5: LineSegment StartX=26 StartY=39.685 StartZ=0 EndX=26 EndY=-40.315 EndZ=0
    g6: LineSegment StartX=26 StartY=-40.315 StartZ=0 EndX=11 EndY=-40.315 EndZ=0
    g7: LineSegment StartX=11 StartY=-40.315 StartZ=0 EndX=11 EndY=39.685 EndZ=0
  constraints (22):
    c: Coincident(g0,g1)
    c: Coincident(g1,g2)
    c: Coincident(g2,g3)
    c: Coincident(g3,g0)
    c: Horizontal(g0)
    c: Horizontal(g2)
    c: Vertical(g1)
    c: Vertical(g3)
    c: Coincident(g4,g5)
    c: Coincident(g5,g6)
    c: Coincident(g6,g7)
    c: Coincident(g7,g4)
    c: Horizontal(g4)
    c: Horizontal(g6)
    c: Vertical(g5)
    c: Vertical(g7)
    c: DistanceX(g0,g4) = 22
    c: Distance(g-1,g7) = 11
    c: Distance(g5) = 80
    c: Distance(g4) = 15
    c: Distance(g0) = 15
    c: Horizontal(g0,g4)
FEATURE [Part::Extrusion] Extrude080  label="Extrude084"
  Base = -> Sketch107
  Dir = (1,0,0)
  DirMode = 2
  FaceMakerClass = Part::FaceMakerBullseye
  LengthFwd = 300
  LengthRev = 0
  Solid = true
  Symmetric = true
FEATURE [Part::Cut] Cut037
  Base = -> Revolve017
  Tool = -> Extrude080
FEATURE [Sketcher::SketchObject] Sketch108
  FullyConstrained = true
  Placement = pos=(0,0,0) rot=(1,0,0;1.5708rad)
  expr: Constraints[17] = Spreadsheet012.E6
  expr: Constraints[18] = Spreadsheet012.B6 - 2 * Spreadsheet012.C6
  expr: Constraints[19] = (Spreadsheet012.B6 - 2 * Spreadsheet012.C6) / 2
  expr: Constraints[20] = Spreadsheet012.E6 / 2
  sketch-geometry (9):
    g0: LineSegment StartX=30 StartY=3 StartZ=0 EndX=30 EndY=-3 EndZ=0
    g1: LineSegment StartX=25 StartY=-8 StartZ=0 EndX=-25 EndY=-8 EndZ=0
    g2: LineSegment StartX=-30 StartY=-3 StartZ=0 EndX=-30 EndY=3 EndZ=0
    g3: LineSegment StartX=-25 StartY=8 StartZ=0 EndX=25 EndY=8 EndZ=0
    g4: GeomPoint X=0 Y=0 Z=0
    g5: ArcOfCircle CenterX=-25 CenterY=3 CenterZ=0 NormalX=0 NormalY=0 NormalZ=1 AngleXU=0 Radius=5 StartAngle=1.5708 EndAngle=3.14159
    g6: ArcOfCircle CenterX=-25 CenterY=-3 CenterZ=0 NormalX=0 NormalY=0 NormalZ=1 AngleXU=0 Radius=5 StartAngle=3.14159 EndAngle=4.71239
    g7: ArcOfCircle CenterX=25 CenterY=-3 CenterZ=0 NormalX=0 NormalY=0 NormalZ=1 AngleXU=0 Radius=5 StartAngle=4.71239 EndAngle=6.28319
    g8: ArcOfCircle CenterX=25 CenterY=3 CenterZ=0 NormalX=0 NormalY=0 NormalZ=1 AngleXU=0 Radius=5 StartAngle=-4.09e-14 EndAngle=1.5708
  constraints (21):
    c: Horizontal(g1)
    c: Horizontal(g3)
    c: Vertical(g0)
    c: Vertical(g2)
    c: Coincident(g4,g-1)
    c: Tangent(g3,g5) = 1.5708
    c: Tangent(g2,g5) = 1.5708
    c: Tangent(g1,g6) = 1.5708
    c: Tangent(g2,g6) = 1.5708
    c: Tangent(g1,g7) = 1.5708
    c: Tangent(g0,g7) = 1.5708
    c: Tangent(g0,g8) = 1.5708
    c: Tangent(g3,g8) = 1.5708
    c: Radius(g8) = 5
    c: Equal(g8,g7)
    c: Equal(g7,g6)
    c: Equal(g6,g5)
    c: DistanceY(g1,g3) = 16
    c: DistanceX(g2,g0) = 60
    c: Distance(g4,g2) = 30
    c: Distance(g4,g1) = 8
FEATURE [Part::Extrusion] Extrude081  label="Extrude085"
  Base = -> Sketch108
  Dir = (0,-1,2e-16)
  DirMode = 2
  FaceMakerClass = Part::FaceMakerBullseye
  LengthFwd = 60
  LengthRev = 0
  Solid = true
  Symmetric = true
FEATURE [Part::Cut] Cut038
  Base = -> Cut037
  Tool = -> Extrude081
FEATURE [Sketcher::SketchObject] Sketch109
  FullyConstrained = true
  Placement = pos=(0,0,0) rot=(0.57735,0.57735,0.57735;2.0944rad)
  expr: Constraints[1] = Spreadsheet012.dia / 2
  sketch-geometry (1):
    g0: Circle CenterX=0 CenterY=0 CenterZ=0 NormalX=0 NormalY=0 NormalZ=1 AngleXU=0 Radius=6
  constraints (2):
    c: Coincident(g0,g-1)
    c: Radius(g0) = 6
FEATURE [Part::Extrusion] Extrude082  label="Extrude086"
  Base = -> Sketch109
  Dir = (1,0,0)
  DirMode = 2
  FaceMakerClass = Part::FaceMakerBullseye
  LengthFwd = 300
  LengthRev = 0
  Solid = true
  Symmetric = true
FEATURE [Part::Cut] Cut039  label="turnBackle004"
  Base = -> Cut038
  Placement = pos=(-530,0,0) rot=(0,0,1;0rad)
  Tool = -> Extrude082
  expr: .Placement.Base.x = -(Spreadsheet012.dia * 2.5 + 500)
FEATURE [Part::Cylinder] Cylinder008  label="rod006"
  Angle = 360
  AttacherType = Attacher::AttachEngine3D
  FirstAngle = 0
  Height = 2635
  Placement = pos=(-536,0,-1.37e-13) rot=(0,-1,0;1.5708rad)
  Radius = 6
  SecondAngle = 0
  expr: .Placement.Base.x = -(Spreadsheet012.dia * 3 + 500)
  expr: Height = Spreadsheet012.l1
  expr: Radius = Spreadsheet012.dia / 2
FEATURE [Part::Extrusion] Extrude083  label="Extrude087"
  Base = -> Sketch105
  Dir = (0,-1,2e-16)
  DirMode = 2
  FaceMakerClass = Part::FaceMakerBullseye
  LengthFwd = 6
  LengthRev = 0
  Placement = pos=(0,9,0) rot=(0,0,1;0rad)
  Solid = true
  Symmetric = true
  expr: .Placement.Base.y = Spreadsheet012.dia / 2 + Spreadsheet012.t0 / 2
  expr: LengthFwd = Spreadsheet012.t0
FEATURE [Part::FeaturePython] Clone014  label="Extrude088"  # Draft clone (typed FeaturePython)
  AttacherType = Attacher::AttachEngine3D
  Fuse = false
  Objects = -> [Extrude083]
  Placement = pos=(-3195,9,0) rot=(0,1,0;3.14159rad)
  Scale = (1,1,1)
  expr: .Placement.Base.x = -Spreadsheet012.L0
  expr: .Placement.Base.y = Spreadsheet012.t0 / 2 + Spreadsheet012.dia / 2
FEATURE [App::Part] Part038  label="TurnBackleB"
  Group = -> [Spreadsheet012,Sketch105,Cylinder007,Extrude083,Revolve017,Sketch107,Cut038,Cut037,Extrude080,Extrude081,Extrude082,Sketch108,Sketch106,Sketch109,Cut039,Cylinder008,Clone014]
  Origin = -> Origin044
  Placement = pos=(-1778.27,238.926,0) rot=(1,0,0;4.71239rad)
FEATURE [Part::Compound] Compound042  label="trunBackle"
  Links = -> [Part038]
  Placement = pos=(-4690.78,487.977,0) rot=(0,0,1;2.9339rad)
FEATURE [Part::Mirroring] Mirror036  label="trunBackle (mirrored)"
  Base = (1000,0,0)
  Normal = (0,-1,0)
  Source = -> Compound042
FEATURE [App::Part] Part036  label="skimmerBrade001"
  Group = -> [Part035,Part034,CNROK75_U,Compound041,Spreadsheet011,Part037,Array029,axisCoincident_001_mirror,ChannelSteel007,Extrude077,Sketch104,Extrude079,Mirror035,Part038,Compound042,Mirror036]
  Origin = -> Origin040
  Placement = pos=(-1076.22,0,5237.31) rot=(0,0,1;0rad)
FEATURE [App::Part] Part010  label="movingPart"
  Group = -> [Part006,Array019,Part004,Part036]
  Origin = -> Origin014
FEATURE [App::Part] Part001  label="Assy_15.5m"
  Group = -> [________________1500_v16,Part010,Part011,Part012,Part013,Part018,Part032,Part003,Part033]
  Origin = -> Origin002
